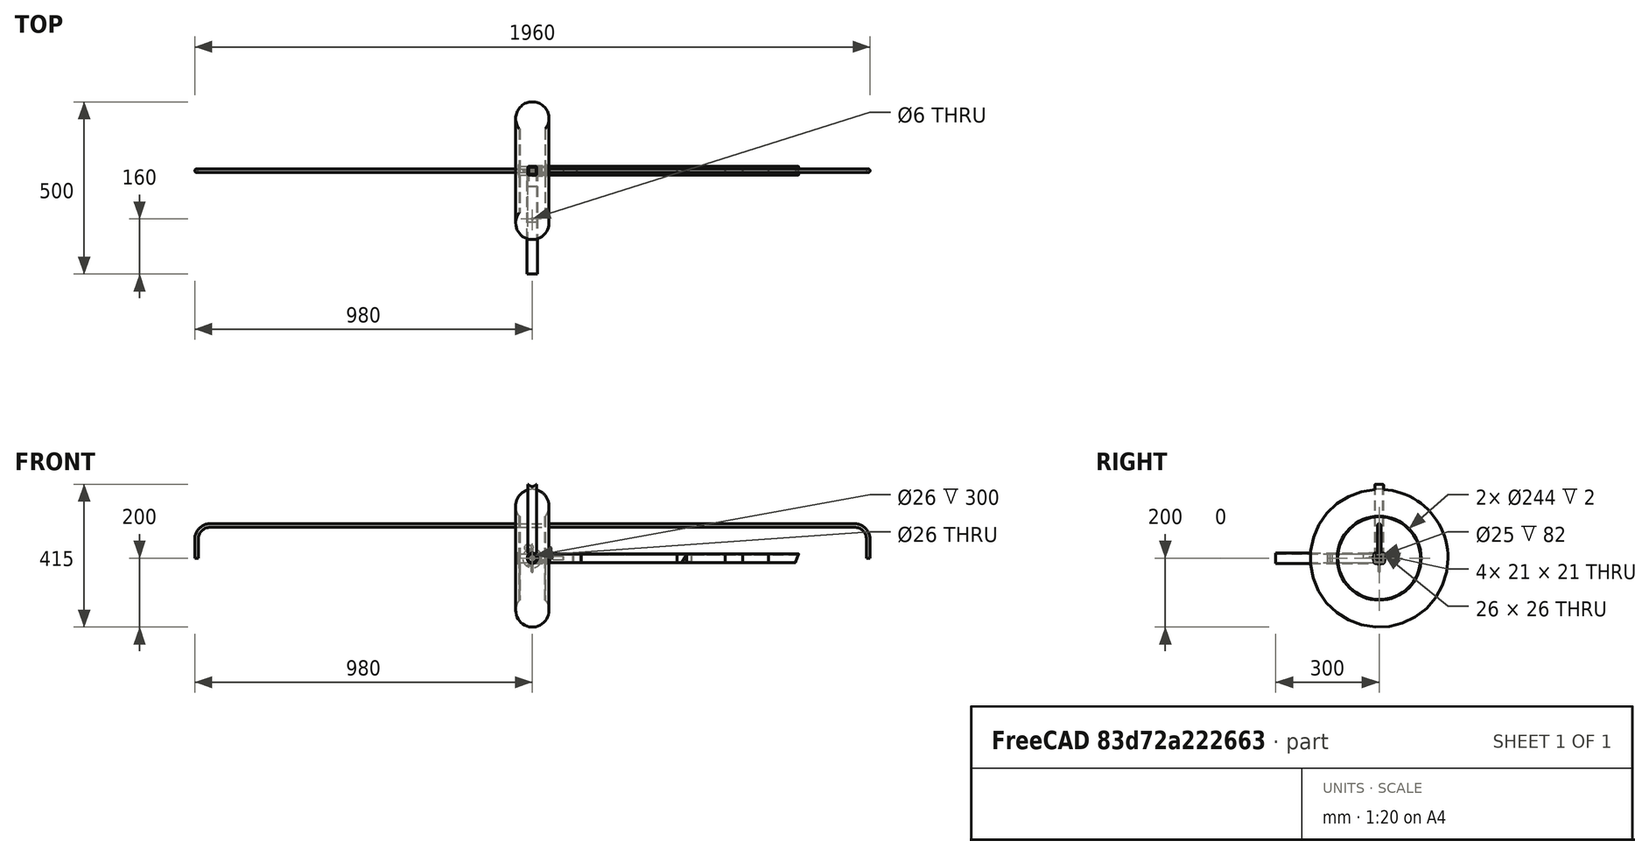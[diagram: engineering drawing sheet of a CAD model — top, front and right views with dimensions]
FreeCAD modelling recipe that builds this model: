
FCSTD DOCUMENT  (FreeCAD 1.0R39109 (Git))
Label: brouetteas4
License: Creative Commons Attribution-NonCommercial-ShareAlike
LicenseURL: http://creativecommons.org/licenses/by-nc-sa/4.0/
objects: PartDesign::CoordinateSystem×62, App::Link×60, Sketcher::SketchObject×37, TechDraw::DrawViewDimension×27, App::Part×25, PartDesign::Body×24, TechDraw::DrawViewBalloon×23, PartDesign::Pad×20, TechDraw::DrawProjGroupItem×15, PartDesign::Groove×8, TechDraw::DrawSVGTemplate×7, TechDraw::DrawPage×7, PartDesign::Plane×6, TechDraw::DrawProjGroup×3, TechDraw::DrawViewDimExtent×3, App::DocumentObjectGroup×2, PartDesign::AdditivePipe×2, Spreadsheet::Sheet×2, PartDesign::Revolution×2, App::FeaturePython×1, +5 more types
note: 320 computed .brp shape members not serialized (recipe doc carries the construction recipe); baked Part::Feature solids carry a one-line shape summary decoded from their .brp

FEATURE [PartDesign::CoordinateSystem] LCS_Origin
  AttacherType = Attacher::AttachEngine3D
  AttachmentSupport = -> [X_Axis]
  MapMode = 2
FEATURE [App::DocumentObjectGroup] Constraints
FEATURE [App::FeaturePython] Variables  # WARN: FeaturePython — macro-defined, semantics opaque (R4)
FEATURE [Sketcher::SketchObject] Sketch
  ArcFitTolerance = 0
  FullyConstrained = true
  MakeInternals = false
  MapMode = 5
  Placement = pos=(0,0,0) rot=(0.57735,0.57735,0.57735;2.0944rad)
  expr: Constraints[15] = .Constraints.hauteur * 0.1
  expr: Constraints[27] = .Constraints.epaisseur
  sketch-geometry (12):
    g0: LineSegment StartX=-10 StartY=12.5 StartZ=0 EndX=10 EndY=12.5 EndZ=0
    g1: LineSegment StartX=12.5 StartY=10 StartZ=0 EndX=12.5 EndY=-10 EndZ=0
    g2: LineSegment StartX=10 StartY=-12.5 StartZ=0 EndX=-10 EndY=-12.5 EndZ=0
    g3: LineSegment StartX=-12.5 StartY=-10 StartZ=0 EndX=-12.5 EndY=10 EndZ=0
    g4: ArcOfCircle CenterX=-10 CenterY=10 CenterZ=0 NormalX=0 NormalY=0 NormalZ=1 AngleXU=0 Radius=2.5 StartAngle=1.5708 EndAngle=3.14159
    g5: ArcOfCircle CenterX=10 CenterY=10 CenterZ=0 NormalX=0 NormalY=0 NormalZ=1 AngleXU=0 Radius=2.5 StartAngle=2e-16 EndAngle=1.5708
    g6: ArcOfCircle CenterX=10 CenterY=-10 CenterZ=0 NormalX=0 NormalY=0 NormalZ=1 AngleXU=0 Radius=2.5 StartAngle=4.71239 EndAngle=6.28319
    g7: ArcOfCircle CenterX=-10 CenterY=-10 CenterZ=0 NormalX=0 NormalY=0 NormalZ=1 AngleXU=0 Radius=2.5 StartAngle=3.14159 EndAngle=4.71239
    g8: LineSegment StartX=-10.5 StartY=10.5 StartZ=0 EndX=10.5 EndY=10.5 EndZ=0
    g9: LineSegment StartX=10.5 StartY=10.5 StartZ=0 EndX=10.5 EndY=-10.5 EndZ=0
    g10: LineSegment StartX=10.5 StartY=-10.5 StartZ=0 EndX=-10.5 EndY=-10.5 EndZ=0
    g11: LineSegment StartX=-10.5 StartY=-10.5 StartZ=0 EndX=-10.5 EndY=10.5 EndZ=0
  constraints (28):
    c: Horizontal(g2)
    c: Vertical(g3)
    c: Tangent(g0,g4) = 1.5708
    c: Tangent(g3,g4) = 1.5708
    c: Tangent(g0,g5) = 1.5708
    c: Tangent(g1,g5) = 1.5708
    c: Tangent(g1,g6) = 1.5708
    c: Tangent(g2,g6) = 1.5708
    c: Tangent(g2,g7) = 1.5708
    c: Tangent(g3,g7) = 1.5708
    c: Equal(g4,g5)
    c: DistanceY(g2,g0) = 25  'hauteur'
    c: DistanceX(g3,g1) = 25  'largeur'
    c: Equal(g5,g6)
    c: Equal(g6,g7)
    c: Radius(g7) = 2.5
    c: Symmetric(g1,g1,g-1)
    c: Symmetric(g0,g0,g-2)
    c: Coincident(g8,g9)
    c: Coincident(g9,g10)
    c: Coincident(g10,g11)
    c: Coincident(g11,g8)
    c: Horizontal(g10)
    c: Vertical(g11)
    c: Symmetric(g8,g9,g-1)
    c: Symmetric(g8,g8,g-2)
    c: DistanceX(g3,g8) = 2  'epaisseur'
    c: DistanceY(g2,g9) = 2
FEATURE [PartDesign::Pad] Pad
  Direction = (1,1e-16,-1e-16)
  Length = 2285
  Length2 = 100
  Placement = pos=(0,0,0) rot=(0.57735,0.57735,0.57735;2.0944rad)
  Profile = -> Sketch
  Suppressed = false
  Type = 0
  expr: Length = Spreadsheet.B4 - Spreadsheet.B2 + 300
FEATURE [PartDesign::CoordinateSystem] LCS_0  label="cote1"
  AttacherType = Attacher::AttachEngine3D
  AttachmentSupport = -> [X_Axis002]
  MapMode = 2
FEATURE [PartDesign::CoordinateSystem] LCS_0001  label="cote1A2"
  AttacherType = Attacher::AttachEngine3D
  AttachmentSupport = -> [X_Axis003]
  MapMode = 2
FEATURE [Sketcher::SketchObject] Sketch001
  ArcFitTolerance = 0
  FullyConstrained = true
  MakeInternals = false
  MapMode = 5
  Placement = pos=(0,0,0) rot=(0.57735,0.57735,0.57735;2.0944rad)
  expr: Constraints[15] = .Constraints.hauteur * 0.1
  expr: Constraints[27] = .Constraints.epaisseur
  sketch-geometry (12):
    g0: LineSegment StartX=-10 StartY=12.5 StartZ=0 EndX=10 EndY=12.5 EndZ=0
    g1: LineSegment StartX=12.5 StartY=10 StartZ=0 EndX=12.5 EndY=-10 EndZ=0
    g2: LineSegment StartX=10 StartY=-12.5 StartZ=0 EndX=-10 EndY=-12.5 EndZ=0
    g3: LineSegment StartX=-12.5 StartY=-10 StartZ=0 EndX=-12.5 EndY=10 EndZ=0
    g4: ArcOfCircle CenterX=-10 CenterY=10 CenterZ=0 NormalX=0 NormalY=0 NormalZ=1 AngleXU=0 Radius=2.5 StartAngle=1.5708 EndAngle=3.14159
    g5: ArcOfCircle CenterX=10 CenterY=10 CenterZ=0 NormalX=0 NormalY=0 NormalZ=1 AngleXU=0 Radius=2.5 StartAngle=2e-16 EndAngle=1.5708
    g6: ArcOfCircle CenterX=10 CenterY=-10 CenterZ=0 NormalX=0 NormalY=0 NormalZ=1 AngleXU=0 Radius=2.5 StartAngle=4.71239 EndAngle=6.28319
    g7: ArcOfCircle CenterX=-10 CenterY=-10 CenterZ=0 NormalX=0 NormalY=0 NormalZ=1 AngleXU=0 Radius=2.5 StartAngle=3.14159 EndAngle=4.71239
    g8: LineSegment StartX=-10.5 StartY=10.5 StartZ=0 EndX=10.5 EndY=10.5 EndZ=0
    g9: LineSegment StartX=10.5 StartY=10.5 StartZ=0 EndX=10.5 EndY=-10.5 EndZ=0
    g10: LineSegment StartX=10.5 StartY=-10.5 StartZ=0 EndX=-10.5 EndY=-10.5 EndZ=0
    g11: LineSegment StartX=-10.5 StartY=-10.5 StartZ=0 EndX=-10.5 EndY=10.5 EndZ=0
  constraints (28):
    c: Horizontal(g2)
    c: Vertical(g3)
    c: Tangent(g0,g4) = 1.5708
    c: Tangent(g3,g4) = 1.5708
    c: Tangent(g0,g5) = 1.5708
    c: Tangent(g1,g5) = 1.5708
    c: Tangent(g1,g6) = 1.5708
    c: Tangent(g2,g6) = 1.5708
    c: Tangent(g2,g7) = 1.5708
    c: Tangent(g3,g7) = 1.5708
    c: Equal(g4,g5)
    c: DistanceY(g2,g0) = 25  'hauteur'
    c: DistanceX(g3,g1) = 25  'largeur'
    c: Equal(g5,g6)
    c: Equal(g6,g7)
    c: Radius(g7) = 2.5
    c: Symmetric(g1,g1,g-1)
    c: Symmetric(g0,g0,g-2)
    c: Coincident(g8,g9)
    c: Coincident(g9,g10)
    c: Coincident(g10,g11)
    c: Coincident(g11,g8)
    c: Horizontal(g10)
    c: Vertical(g11)
    c: Symmetric(g8,g9,g-1)
    c: Symmetric(g8,g8,g-2)
    c: DistanceX(g3,g8) = 2  'epaisseur'
    c: DistanceY(g2,g9) = 2
FEATURE [PartDesign::Body] Body001
  AllowCompound = false
  Origin = -> Origin004
FEATURE [PartDesign::Pad] Pad001
  Direction = (1,1e-16,-1e-16)
  Length = 610
  Length2 = 100
  Placement = pos=(0,0,0) rot=(0.57735,0.57735,0.57735;2.0944rad)
  Profile = -> Sketch001
  Suppressed = false
  Type = 0
FEATURE [PartDesign::CoordinateSystem] LCS_0002
  AttacherType = Attacher::AttachEngine3D
  AttachmentOffset = pos=(0,5,0) rot=(0,0,1;0rad)
  AttachmentSupport = -> [X_Axis005]
  MapMode = 2
  Placement = pos=(0,5,0) rot=(0,0,1;0rad)
FEATURE [PartDesign::CoordinateSystem] LCS_0003
  AttacherType = Attacher::AttachEngine3D
  AttachmentOffset = pos=(0,5,0) rot=(0,0,1;0rad)
  AttachmentSupport = -> [X_Axis006]
  MapMode = 2
  Placement = pos=(0,5,0) rot=(0,0,1;0rad)
FEATURE [Sketcher::SketchObject] Sketch002
  ArcFitTolerance = 0
  AttachmentSupport = -> [XZ_Plane007]
  FullyConstrained = true
  MakeInternals = false
  MapMode = 5
  Placement = pos=(0,0,0) rot=(1,0,0;1.5708rad)
  expr: .Constraints.longueur = Spreadsheet.B4 - Spreadsheet.B2 * 2 - 10
  expr: Constraints[4] = Spreadsheet.B2
  sketch-geometry (7):
    g0: LineSegment StartX=-975 StartY=0 StartZ=0 EndX=-975 EndY=25 EndZ=0
    g1: LineSegment StartX=975 StartY=8e-16 StartZ=0 EndX=975 EndY=25 EndZ=0
    g2: LineSegment StartX=-975 StartY=25 StartZ=0 EndX=-975 EndY=55 EndZ=0
    g3: LineSegment StartX=-935 StartY=95 StartZ=0 EndX=935 EndY=95 EndZ=0
    g4: LineSegment StartX=975 StartY=55 StartZ=0 EndX=975 EndY=25 EndZ=0
    g5: ArcOfCircle CenterX=935 CenterY=55 CenterZ=0 NormalX=0 NormalY=0 NormalZ=1 AngleXU=0 Radius=40 StartAngle=0 EndAngle=1.5708
    g6: ArcOfCircle CenterX=-935 CenterY=55 CenterZ=0 NormalX=0 NormalY=0 NormalZ=1 AngleXU=0 Radius=40 StartAngle=1.5708 EndAngle=3.14159
  constraints (19):
    c: PointOnObject(g0,g-1)
    c: Vertical(g0)
    c: Vertical(g1)
    c: Symmetric(g0,g1,g-2)
    c: DistanceY(g0,g0) = 25
    c: DistanceX(g0,g1) = 1950  'longueur'
    c: Equal(g1,g0)
    c: Coincident(g0,g2)
    c: Vertical(g2)
    c: Horizontal(g3)
    c: Coincident(g4,g1)
    c: Vertical(g4)
    c: Tangent(g3,g5) = 1.5708
    c: Tangent(g4,g5) = 1.5708
    c: Tangent(g2,g6) = 1.5708
    c: Tangent(g3,g6) = 1.5708
    c: Equal(g6,g5)
    c: DistanceY(g0,g3) = 70
    c: Radius(g6) = 40
FEATURE [Sketcher::SketchObject] Sketch003
  ArcFitTolerance = 0
  AttachmentSupport = -> [XY_Plane007]
  ExternalGeometry = -> [Sketch002]
  FullyConstrained = true
  MakeInternals = false
  MapMode = 5
  sketch-geometry (1):
    g0: Circle CenterX=-975 CenterY=0 CenterZ=0 NormalX=0 NormalY=0 NormalZ=1 AngleXU=0 Radius=5
  constraints (2):
    c: Coincident(g0,g-3)
    c: Diameter(g0) = 10
FEATURE [PartDesign::AdditivePipe] AdditivePipe
  AuxilleryCurvelinear = true
  AuxillerySpineTangent = false
  Binormal = (0,0,0)
  Mode = 0
  Profile = -> Sketch003
  Spine = -> Sketch002
  SpineTangent = false
  Suppressed = false
  Transformation = 0
  Transition = 0
FEATURE [PartDesign::Body] Body002
  AllowCompound = false
  Group = -> [Sketch002,Sketch003,AdditivePipe]
  Origin = -> Origin007
  Tip = -> AdditivePipe
FEATURE [App::Part] A3
  Group = -> [LCS_0002,Body002]
  Nom_de_la_piece = A3
  Origin = -> Origin005
  Reference_AP = fer rond Ø10
  longueur = 2140
FEATURE [Sketcher::SketchObject] Sketch004
  ArcFitTolerance = 0
  AttachmentSupport = -> [YZ_Plane008]
  FullyConstrained = true
  MakeInternals = false
  MapMode = 5
  Placement = pos=(0,0,0) rot=(0.57735,0.57735,0.57735;2.0944rad)
  sketch-geometry (1):
    g0: Circle CenterX=0 CenterY=0 CenterZ=0 NormalX=0 NormalY=0 NormalZ=1 AngleXU=0 Radius=5
  constraints (2):
    c: Coincident(g0,g-1)
    c: Diameter(g0) = 10  'diametre'
FEATURE [PartDesign::Pad] Pad002
  Direction = (1,0,0)
  Length = 90
  Length2 = 100
  Placement = pos=(0,0,0) rot=(0.57735,0.57735,0.57735;2.0944rad)
  Profile = -> Sketch004
  Suppressed = false
  Type = 0
FEATURE [PartDesign::Body] Body003
  AllowCompound = false
  Group = -> [Sketch004,Pad002]
  Origin = -> Origin008
  Tip = -> Pad002
FEATURE [App::Part] A4
  Group = -> [LCS_0003,Body003]
  Nom_de_la_piece = 'A4
  Origin = -> Origin006
  Reference_AP = fer rond Ø10
  longueur = 90
FEATURE [PartDesign::CoordinateSystem] cote2A2
  AttacherType = Attacher::AttachEngine3D
  AttachmentSupport = -> [Pad001]
  MapMode = 5
  Placement = pos=(610,2.684e-13,0) rot=(0.57735,0.57735,0.57735;2.0944rad)
FEATURE [Spreadsheet::Sheet] Spreadsheet
  cells = A1='profile; A2='tube carré; B2=25; C2='mm; A4='taille utile du plateau; B4=2010; C4='X; D4=610; A5='hauteur plateau; B5=500; A6='hauteur de la roue; B6=400; A7='axe; B7=25; A8='epaisseur upn axe; B8=4; A9='espace des roues; B9=95; A10='ecart au sol; B10=75; A11='hauteur des mains; B11==D11 * 0.45; C11='taille de la personne; D11=1700; A12='hauteur du panneau finale; B12=610; A13='tube poigné; B13=30
FEATURE [PartDesign::CoordinateSystem] face1A2
  AttacherType = Attacher::AttachEngine3D
  AttachmentOffset = pos=(0,12.5,0) rot=(0,0,1;0rad)
  AttachmentSupport = -> [Pad001]
  MapMode = 5
  Placement = pos=(12.5,12.5,2.1e-15) rot=(0.57735,0.57735,0.57735;4.18879rad)
  expr: .AttachmentOffset.Base.y = Spreadsheet.B2 / 2
FEATURE [PartDesign::CoordinateSystem] face4A2
  AttacherType = Attacher::AttachEngine3D
  AttachmentOffset = pos=(0,597.5,0) rot=(0,0,1;0rad)
  AttachmentSupport = -> [Pad001]
  MapMode = 5
  Placement = pos=(597.5,12.5,2.1e-15) rot=(0.57735,0.57735,0.57735;4.18879rad)
  expr: .AttachmentOffset.Base.y = Spreadsheet.D4 - Spreadsheet.B2 / 2
FEATURE [PartDesign::CoordinateSystem] face2  label="face2A2"
  AttacherType = Attacher::AttachEngine3D
  AttachmentOffset = pos=(0,207.5,0) rot=(0,0,1;0rad)
  AttachmentSupport = -> [Pad001]
  MapMode = 5
  Placement = pos=(207.5,12.5,2.1e-15) rot=(0.57735,0.57735,0.57735;4.18879rad)
  expr: .AttachmentOffset.Base.y = (Spreadsheet.D4 - Spreadsheet.B2) * 1 / 3 + Spreadsheet.B2 / 2
FEATURE [PartDesign::CoordinateSystem] face3A2
  AttacherType = Attacher::AttachEngine3D
  AttachmentOffset = pos=(0,402.5,0) rot=(0,0,1;0rad)
  AttachmentSupport = -> [Pad001]
  MapMode = 5
  Placement = pos=(402.5,12.5,2.1e-15) rot=(0.57735,0.57735,0.57735;4.18879rad)
  expr: .AttachmentOffset.Base.y = (Spreadsheet.D4 - Spreadsheet.B2) * 2 / 3 + Spreadsheet.B2 / 2
FEATURE [PartDesign::CoordinateSystem] attach
  AttacherType = Attacher::AttachEngine3D
  AttachmentOffset = pos=(0,305,0) rot=(0,0,1;0rad)
  AttachmentSupport = -> [Pad001]
  MapMode = 5
  Placement = pos=(305,-12.5,-2.1e-15) rot=(0.57735,0.57735,-0.57735;2.0944rad)
  expr: .AttachmentOffset.Base.y = Spreadsheet.D4 / 2
FEATURE [App::Link] A2001
  AssemblyType = Asm4EE
  AttachedBy = #attach
  AttachedTo = Parent Assembly#LCS_Origin
  AttachmentOffset = pos=(0,0,0) rot=(0,-1,0;1.5708rad)
  LinkPlacement = pos=(12.5,-305,-2.84e-14) rot=(-0.707107,-0.707107,0;3.14159rad)
  LinkedObject = -> A2
  Placement = pos=(12.5,-305,-2.84e-14) rot=(-0.707107,-0.707107,0;3.14159rad)
  expr: Placement = LCS_Origin.Placement * AttachmentOffset * attach.Placement ^ -1
FEATURE [App::Link] A1001
  AssemblyType = Asm4EE
  AttachedBy = #LCS_0
  AttachedTo = A2001#face1A2
  AttachmentOffset = pos=(0,0,0) rot=(0,-1,0;1.5708rad)
  LinkPlacement = pos=(25,-292.5,-3.05e-14) rot=(0,0,1;0rad)
  LinkedObject = -> A1
  Placement = pos=(25,-292.5,-3.05e-14) rot=(0,0,1;0rad)
  expr: Placement = A2001.Placement * face1A2.Placement * AttachmentOffset * LCS_0.Placement ^ -1
FEATURE [App::Link] A1004
  AssemblyType = Asm4EE
  AttachedBy = #LCS_0
  AttachedTo = A2001#face4A2
  AttachmentOffset = pos=(0,0,0) rot=(0,-1,0;1.5708rad)
  LinkPlacement = pos=(25,292.5,1.54e-14) rot=(0,0,1;0rad)
  LinkedObject = -> A1
  Placement = pos=(25,292.5,1.54e-14) rot=(0,0,1;0rad)
  expr: Placement = A2001.Placement * face4A2.Placement * AttachmentOffset * LCS_0.Placement ^ -1
FEATURE [App::Link] A3001
  AssemblyType = Asm4EE
  AttachedBy = #LCS_0002
  AttachedTo = A1001#faceA1
  AttachmentOffset = pos=(0,0,0) rot=(0.57735,0.57735,-0.57735;4.18879rad)
  LinkPlacement = pos=(1005,-310,-12.5) rot=(0,0,1;0rad)
  LinkedObject = -> A3
  Placement = pos=(1005,-310,-12.5) rot=(0,0,1;0rad)
  expr: Placement = A1001.Placement * faceA1.Placement * AttachmentOffset * LCS_0002.Placement ^ -1
FEATURE [App::Link] A3002
  AssemblyType = Asm4EE
  AttachedBy = #LCS_0002
  AttachedTo = A1004#face2A1
  AttachmentOffset = pos=(0,0,0) rot=(-0.57735,0.57735,-0.57735;2.0944rad)
  LinkPlacement = pos=(1005,310,-12.5) rot=(0,0,1;3.14159rad)
  LinkedObject = -> A3
  Placement = pos=(1005,310,-12.5) rot=(0,0,1;3.14159rad)
  expr: Placement = A1004.Placement * face2A1.Placement * AttachmentOffset * LCS_0002.Placement ^ -1
FEATURE [App::Link] A4001
  AssemblyType = Asm4EE
  AttachedBy = #LCS_0003
  AttachedTo = A1001#faceA1
  AttachmentOffset = pos=(0,0,0) rot=(0,-0.707107,0.707107;3.14159rad)
  LinkPlacement = pos=(1005,-310,-12.5) rot=(0,-1,0;1.5708rad)
  LinkedObject = -> A4
  Placement = pos=(1005,-310,-12.5) rot=(0,-1,0;1.5708rad)
  expr: Placement = A1001.Placement * faceA1.Placement * AttachmentOffset * LCS_0003.Placement ^ -1
FEATURE [App::Link] A4002
  AssemblyType = Asm4EE
  AttachedBy = #LCS_0003
  AttachedTo = A1004#face2A1
  AttachmentOffset = pos=(0,0,0) rot=(1,0,0;4.71239rad)
  LinkPlacement = pos=(1005,310,-12.5) rot=(-0.707107,0,-0.707107;3.14159rad)
  LinkedObject = -> A4
  Placement = pos=(1005,310,-12.5) rot=(-0.707107,0,-0.707107;3.14159rad)
  expr: Placement = A1004.Placement * face2A1.Placement * AttachmentOffset * LCS_0003.Placement ^ -1
FEATURE [PartDesign::CoordinateSystem] basbord
  AttacherType = Attacher::AttachEngine3D
  AttachmentOffset = pos=(0,-12.5,0) rot=(0,0,1;0rad)
  AttachmentSupport = -> [Pad001]
  MapMode = 5
  Placement = pos=(610,2.684e-13,-12.5) rot=(0.57735,0.57735,0.57735;2.0944rad)
  expr: .AttachmentOffset.Base.y = -Spreadsheet.B2 / 2
FEATURE [App::Link] A2003
  AssemblyType = Asm4EE
  AttachedBy = #basbord
  AttachedTo = A1004#face2A1
  AttachmentOffset = pos=(0,0,0) rot=(0,0,1;1.5708rad)
  LinkPlacement = pos=(1005,-305,-25) rot=(0.707107,0.707107,0;3.14159rad)
  LinkedObject = -> A2
  Placement = pos=(1005,-305,-25) rot=(0.707107,0.707107,0;3.14159rad)
  expr: Placement = A1004.Placement * face2A1.Placement * AttachmentOffset * basbord.Placement ^ -1
FEATURE [PartDesign::CoordinateSystem] LCS_0004
  AttacherType = Attacher::AttachEngine3D
  AttachmentOffset = pos=(100,-12.5,0) rot=(0,0,1;0rad)
  AttachmentSupport = -> [X_Axis009]
  MapMode = 2
  Placement = pos=(100,-12.5,0) rot=(0,0,1;0rad)
FEATURE [Sketcher::SketchObject] Sketch005
  ArcFitTolerance = 0
  AttachmentSupport = -> [XY_Plane010]
  FullyConstrained = true
  MakeInternals = false
  MapMode = 5
  sketch-geometry (16):
    g0: LineSegment StartX=-41 StartY=12.5 StartZ=0 EndX=41 EndY=12.5 EndZ=0
    g1: LineSegment StartX=-41 StartY=12.5 StartZ=0 EndX=-41 EndY=17.5 EndZ=0
    g2: LineSegment StartX=-41 StartY=17.5 StartZ=0 EndX=-38 EndY=17.5 EndZ=0
    g3: LineSegment StartX=-38 StartY=17.5 StartZ=0 EndX=-38 EndY=120 EndZ=0
    g4: LineSegment StartX=-38 StartY=120 StartZ=0 EndX=-36 EndY=120 EndZ=0
    g5: LineSegment StartX=-36 StartY=120 StartZ=0 EndX=-36 EndY=122 EndZ=0
    g6: LineSegment StartX=-36 StartY=122 StartZ=0 EndX=-38 EndY=122 EndZ=0
    g7: LineSegment StartX=41 StartY=12.5 StartZ=0 EndX=41 EndY=17.5 EndZ=0
    g8: LineSegment StartX=41 StartY=17.5 StartZ=0 EndX=38 EndY=17.5 EndZ=0
    g9: LineSegment StartX=38 StartY=17.5 StartZ=0 EndX=38 EndY=120 EndZ=0
    g10: LineSegment StartX=38 StartY=120 StartZ=0 EndX=36 EndY=120 EndZ=0
    g11: LineSegment StartX=36 StartY=120 StartZ=0 EndX=36 EndY=122 EndZ=0
    g12: LineSegment StartX=36 StartY=122 StartZ=0 EndX=38 EndY=122 EndZ=0
    g13: GeomPoint [constr] X=-1e-15 Y=151.744 Z=0
    g14: GeomPoint [constr] X=0 Y=200 Z=0
    g15: ArcOfCircle CenterX=-1e-15 CenterY=151.744 CenterZ=0 NormalX=0 NormalY=0 NormalZ=1 AngleXU=0 Radius=48.2564 StartAngle=5.61907 EndAngle=10.0889
  constraints (42):
    c: Symmetric(g0,g0,g-2)
    c: Coincident(g0,g1)
    c: Vertical(g1)
    c: Coincident(g1,g2)
    c: Horizontal(g2)
    c: Coincident(g2,g3)
    c: Vertical(g3)
    c: Coincident(g3,g4)
    c: Horizontal(g4)
    c: Coincident(g4,g5)
    c: Coincident(g5,g6)
    c: Horizontal(g6)
    c: Vertical(g5)
    c: PointOnObject(g6,g3)
    c: DistanceX(g2,g2) = 3
    c: DistanceX(g4,g4) = 2
    c: DistanceY(g5,g5) = 2
    c: Vertical(g7)
    c: Coincident(g7,g8)
    c: Horizontal(g8)
    c: Coincident(g8,g9)
    c: Coincident(g9,g10)
    c: Horizontal(g10)
    c: Coincident(g10,g11)
    c: Coincident(g11,g12)
    c: Horizontal(g12)
    c: Vertical(g11)
    c: PointOnObject(g12,g9)
    c: Symmetric(g9,g3,g-2)
    c: Symmetric(g5,g11,g-2)
    c: DistanceX(g2,g8) = 76
    c: Coincident(g0,g7)
    c: DistanceY(g-1,g0) = 12.5
    c: DistanceY(g7,g7) = 5
    c: Symmetric(g2,g8,g-2)
    c: PointOnObject(g14,g-2)
    c: DistanceY(g-1,g9) = 120
    c: DistanceY(g-1,g14) = 200
    c: Coincident(g15,g13)
    c: Coincident(g15,g6)
    c: Coincident(g15,g12)
    c: PointOnObject(g14,g15)
FEATURE [PartDesign::Revolution] Revolution
  Angle = 360
  Angle2 = 60
  Axis = (1,0,0)
  Base = (0,0,0)
  Profile = -> Sketch005
  ReferenceAxis = -> Sketch005 [H_Axis]
  Suppressed = false
  Type = 0
FEATURE [PartDesign::Body] Body004
  AllowCompound = false
  Group = -> [Sketch005,Revolution]
  Origin = -> Origin010
  Tip = -> Revolution
FEATURE [App::Part] Roue_increvable___389___axe25_L_82
  Group = -> [LCS_0004,Body004]
  Nom_de_la_piece = roue
  Origin = -> Origin009
  Reference_AP = Roue increvable Ø389 Øaxe25 L 82
FEATURE [PartDesign::CoordinateSystem] LCS_0005
  AttacherType = Attacher::AttachEngine3D
  AttachmentSupport = -> [X_Axis011]
  MapMode = 2
FEATURE [PartDesign::Body] Body005
  AllowCompound = false
  Origin = -> Origin012
FEATURE [Sketcher::SketchObject] Sketch007
  ArcFitTolerance = 0
  FullyConstrained = true
  MakeInternals = false
  MapMode = 2
  Placement = pos=(0,0,0) rot=(0.57735,0.57735,0.57735;2.0944rad)
  expr: Constraints[15] = .Constraints.hauteur * 0.1
  expr: Constraints[27] = .Constraints.epaisseur
  sketch-geometry (12):
    g0: LineSegment StartX=-10 StartY=12.5 StartZ=0 EndX=10 EndY=12.5 EndZ=0
    g1: LineSegment StartX=12.5 StartY=10 StartZ=0 EndX=12.5 EndY=-10 EndZ=0
    g2: LineSegment StartX=10 StartY=-12.5 StartZ=0 EndX=-10 EndY=-12.5 EndZ=0
    g3: LineSegment StartX=-12.5 StartY=-10 StartZ=0 EndX=-12.5 EndY=10 EndZ=0
    g4: ArcOfCircle CenterX=-10 CenterY=10 CenterZ=0 NormalX=0 NormalY=0 NormalZ=1 AngleXU=0 Radius=2.5 StartAngle=1.5708 EndAngle=3.14159
    g5: ArcOfCircle CenterX=10 CenterY=10 CenterZ=0 NormalX=0 NormalY=0 NormalZ=1 AngleXU=0 Radius=2.5 StartAngle=2e-16 EndAngle=1.5708
    g6: ArcOfCircle CenterX=10 CenterY=-10 CenterZ=0 NormalX=0 NormalY=0 NormalZ=1 AngleXU=0 Radius=2.5 StartAngle=4.71239 EndAngle=6.28319
    g7: ArcOfCircle CenterX=-10 CenterY=-10 CenterZ=0 NormalX=0 NormalY=0 NormalZ=1 AngleXU=0 Radius=2.5 StartAngle=3.14159 EndAngle=4.71239
    g8: LineSegment StartX=-10.5 StartY=10.5 StartZ=0 EndX=10.5 EndY=10.5 EndZ=0
    g9: LineSegment StartX=10.5 StartY=10.5 StartZ=0 EndX=10.5 EndY=-10.5 EndZ=0
    g10: LineSegment StartX=10.5 StartY=-10.5 StartZ=0 EndX=-10.5 EndY=-10.5 EndZ=0
    g11: LineSegment StartX=-10.5 StartY=-10.5 StartZ=0 EndX=-10.5 EndY=10.5 EndZ=0
  constraints (28):
    c: Horizontal(g2)
    c: Vertical(g3)
    c: Tangent(g0,g4) = 1.5708
    c: Tangent(g3,g4) = 1.5708
    c: Tangent(g0,g5) = 1.5708
    c: Tangent(g1,g5) = 1.5708
    c: Tangent(g1,g6) = 1.5708
    c: Tangent(g2,g6) = 1.5708
    c: Tangent(g2,g7) = 1.5708
    c: Tangent(g3,g7) = 1.5708
    c: Equal(g4,g5)
    c: DistanceY(g2,g0) = 25  'hauteur'
    c: DistanceX(g3,g1) = 25  'largeur'
    c: Equal(g5,g6)
    c: Equal(g6,g7)
    c: Radius(g7) = 2.5
    c: Symmetric(g1,g1,g-1)
    c: Symmetric(g0,g0,g-2)
    c: Coincident(g8,g9)
    c: Coincident(g9,g10)
    c: Coincident(g10,g11)
    c: Coincident(g11,g8)
    c: Horizontal(g10)
    c: Vertical(g11)
    c: Symmetric(g8,g9,g-1)
    c: Symmetric(g8,g8,g-2)
    c: DistanceX(g3,g8) = 2  'epaisseur'
    c: DistanceY(g2,g9) = 2
FEATURE [PartDesign::Pad] Pad003
  Direction = (1,1e-16,-1e-16)
  Length = 258.5
  Length2 = 100
  Placement = pos=(0,0,0) rot=(0.57735,0.57735,0.57735;2.0944rad)
  Profile = -> Sketch007
  Suppressed = false
  Type = 0
  expr: Length = Spreadsheet.B5 - Spreadsheet.B6 / 2 - Spreadsheet.B7 / 2 - Spreadsheet.B8 - Spreadsheet.B2
FEATURE [PartDesign::CoordinateSystem] roue1
  AttacherType = Attacher::AttachEngine3D
  AttachmentOffset = pos=(0,82.5,0) rot=(0,0,1;0rad)
  AttachmentSupport = -> [Pad001]
  MapMode = 5
  Placement = pos=(82.5,1.56e-14,12.5) rot=(0,0,-1;1.5708rad)
  expr: .AttachmentOffset.Base.y = Spreadsheet.B9 - Spreadsheet.B2 / 2
FEATURE [PartDesign::CoordinateSystem] roue2
  AttacherType = Attacher::AttachEngine3D
  AttachmentOffset = pos=(0,527.5,0) rot=(0,0,1;0rad)
  AttachmentSupport = -> [Pad001]
  MapMode = 5
  Placement = pos=(527.5,1.144e-13,12.5) rot=(0,0,-1;1.5708rad)
  expr: .AttachmentOffset.Base.y = Spreadsheet.D4 - (Spreadsheet.B9 - Spreadsheet.B2 / 2)
FEATURE [App::Part] A2
  Group = -> [LCS_0001,Body001,Sketch001,Pad001,cote2A2,face1A2,face4A2,face2,face3A2,attach,basbord,roue1,roue2]
  Nom_de_la_piece = 'A2
  Origin = -> Origin003
  Reference_AP = Tube carré 25 x 2
  longueur = 610
FEATURE [App::Link] A5001
  AssemblyType = Asm4EE
  AttachedBy = #LCS_0005
  AttachedTo = A2003#roue1
  AttachmentOffset = pos=(0,0,0) rot=(-0.57735,-0.57735,-0.57735;2.0944rad)
  LinkPlacement = pos=(1005,-222.5,-37.5) rot=(-0.57735,0.57735,0.57735;2.0944rad)
  LinkedObject = -> A5
  Placement = pos=(1005,-222.5,-37.5) rot=(-0.57735,0.57735,0.57735;2.0944rad)
  expr: Placement = A2003.Placement * roue1.Placement * AttachmentOffset * LCS_0005.Placement ^ -1
FEATURE [App::Link] A5002
  AssemblyType = Asm4EE
  AttachedBy = #LCS_0005
  AttachedTo = A2003#roue2
  AttachmentOffset = pos=(0,0,0) rot=(0,1,0;4.71239rad)
  LinkPlacement = pos=(1005,222.5,-37.5) rot=(0,-1,0;4.71239rad)
  LinkedObject = -> A5
  Placement = pos=(1005,222.5,-37.5) rot=(0,-1,0;4.71239rad)
  expr: Placement = A2003.Placement * roue2.Placement * AttachmentOffset * LCS_0005.Placement ^ -1
FEATURE [PartDesign::CoordinateSystem] renfort
  AttacherType = Attacher::AttachEngine3D
  AttachmentOffset = pos=(0,246,0) rot=(0,0,1;0rad)
  AttachmentSupport = -> [Pad003]
  MapMode = 5
  Placement = pos=(246,5.19e-14,12.5) rot=(0,0,-1;1.5708rad)
  expr: .AttachmentOffset.Base.y = Pad003.Length - Spreadsheet.B2 * 1 mm / 2
FEATURE [PartDesign::CoordinateSystem] LCS_0006
  AttacherType = Attacher::AttachEngine3D
  AttachmentSupport = -> [X_Axis013]
  MapMode = 2
FEATURE [Sketcher::SketchObject] Sketch008
  ArcFitTolerance = 0
  FullyConstrained = true
  MakeInternals = false
  MapMode = 2
  Placement = pos=(0,0,0) rot=(0.57735,0.57735,0.57735;2.0944rad)
  expr: Constraints[15] = .Constraints.hauteur * 0.1
  expr: Constraints[27] = .Constraints.epaisseur
  sketch-geometry (12):
    g0: LineSegment StartX=-10 StartY=12.5 StartZ=0 EndX=10 EndY=12.5 EndZ=0
    g1: LineSegment StartX=12.5 StartY=10 StartZ=0 EndX=12.5 EndY=-10 EndZ=0
    g2: LineSegment StartX=10 StartY=-12.5 StartZ=0 EndX=-10 EndY=-12.5 EndZ=0
    g3: LineSegment StartX=-12.5 StartY=-10 StartZ=0 EndX=-12.5 EndY=10 EndZ=0
    g4: ArcOfCircle CenterX=-10 CenterY=10 CenterZ=0 NormalX=0 NormalY=0 NormalZ=1 AngleXU=0 Radius=2.5 StartAngle=1.5708 EndAngle=3.14159
    g5: ArcOfCircle CenterX=10 CenterY=10 CenterZ=0 NormalX=0 NormalY=0 NormalZ=1 AngleXU=0 Radius=2.5 StartAngle=2e-16 EndAngle=1.5708
    g6: ArcOfCircle CenterX=10 CenterY=-10 CenterZ=0 NormalX=0 NormalY=0 NormalZ=1 AngleXU=0 Radius=2.5 StartAngle=4.71239 EndAngle=6.28319
    g7: ArcOfCircle CenterX=-10 CenterY=-10 CenterZ=0 NormalX=0 NormalY=0 NormalZ=1 AngleXU=0 Radius=2.5 StartAngle=3.14159 EndAngle=4.71239
    g8: LineSegment StartX=-10.5 StartY=10.5 StartZ=0 EndX=10.5 EndY=10.5 EndZ=0
    g9: LineSegment StartX=10.5 StartY=10.5 StartZ=0 EndX=10.5 EndY=-10.5 EndZ=0
    g10: LineSegment StartX=10.5 StartY=-10.5 StartZ=0 EndX=-10.5 EndY=-10.5 EndZ=0
    g11: LineSegment StartX=-10.5 StartY=-10.5 StartZ=0 EndX=-10.5 EndY=10.5 EndZ=0
  constraints (28):
    c: Horizontal(g2)
    c: Vertical(g3)
    c: Tangent(g0,g4) = 1.5708
    c: Tangent(g3,g4) = 1.5708
    c: Tangent(g0,g5) = 1.5708
    c: Tangent(g1,g5) = 1.5708
    c: Tangent(g1,g6) = 1.5708
    c: Tangent(g2,g6) = 1.5708
    c: Tangent(g2,g7) = 1.5708
    c: Tangent(g3,g7) = 1.5708
    c: Equal(g4,g5)
    c: DistanceY(g2,g0) = 25  'hauteur'
    c: DistanceX(g3,g1) = 25  'largeur'
    c: Equal(g5,g6)
    c: Equal(g6,g7)
    c: Radius(g7) = 2.5
    c: Symmetric(g1,g1,g-1)
    c: Symmetric(g0,g0,g-2)
    c: Coincident(g8,g9)
    c: Coincident(g9,g10)
    c: Coincident(g10,g11)
    c: Coincident(g11,g8)
    c: Horizontal(g10)
    c: Vertical(g11)
    c: Symmetric(g8,g9,g-1)
    c: Symmetric(g8,g8,g-2)
    c: DistanceX(g3,g8) = 2  'epaisseur'
    c: DistanceY(g2,g9) = 2
FEATURE [PartDesign::Pad] Pad004
  Direction = (1,1e-16,-1e-16)
  Length = 420
  Length2 = 100
  Placement = pos=(0,0,0) rot=(0.57735,0.57735,0.57735;2.0944rad)
  Profile = -> Sketch008
  Suppressed = false
  Type = 0
  expr: Length = Spreadsheet.D4 - Spreadsheet.B9 * 2
FEATURE [PartDesign::Body] Body006
  AllowCompound = false
  Group = -> [Sketch008,Pad004]
  Origin = -> Origin014
  Tip = -> Pad004
FEATURE [App::Part] A6
  Group = -> [LCS_0006,Body006]
  Nom_de_la_piece = 'A6
  Origin = -> Origin013
  Reference_AP = Tube carré 25 x 2
  longueur = 420
FEATURE [App::Link] A6001
  AssemblyType = Asm4EE
  AttachedBy = #LCS_0006
  AttachedTo = A5001#renfort
  AttachmentOffset = pos=(0,0,0) rot=(0,1,0;4.71239rad)
  LinkPlacement = pos=(1005,-210,-283.5) rot=(0.57735,0.57735,-0.57735;4.18879rad)
  LinkedObject = -> A6
  Placement = pos=(1005,-210,-283.5) rot=(0.57735,0.57735,-0.57735;4.18879rad)
  expr: Placement = A5001.Placement * renfort.Placement * AttachmentOffset * LCS_0006.Placement ^ -1
FEATURE [PartDesign::Body] A1005
  AllowCompound = false
  Origin = -> Origin015
FEATURE [PartDesign::CoordinateSystem] LCS_0007
  AttacherType = Attacher::AttachEngine3D
  AttachmentSupport = -> [X_Axis002]
  MapMode = 2
FEATURE [PartDesign::CoordinateSystem] cote2
  AttacherType = Attacher::AttachEngine3D
  AttachmentSupport = -> [Pad]
  MapMode = 5
  Placement = pos=(2285,1.0054e-12,0) rot=(0.57735,0.57735,0.57735;2.0944rad)
FEATURE [PartDesign::CoordinateSystem] faceA1
  AttacherType = Attacher::AttachEngine3D
  AttachmentOffset = pos=(12.5,980,0) rot=(0,0,1;0rad)
  AttachmentSupport = -> [Pad]
  MapMode = 5
  Placement = pos=(980,-12.5,-12.5) rot=(0.57735,0.57735,-0.57735;2.0944rad)
  expr: .AttachmentOffset.Base.x = Spreadsheet.B2 / 2
  expr: .AttachmentOffset.Base.y = (Spreadsheet.B4 - Spreadsheet.B2 * 2) / 2
FEATURE [PartDesign::CoordinateSystem] face2A1
  AttacherType = Attacher::AttachEngine3D
  AttachmentOffset = pos=(-12.5,980,0) rot=(0,0,1;0rad)
  AttachmentSupport = -> [Pad]
  MapMode = 5
  Placement = pos=(980,12.5,-12.5) rot=(0.57735,0.57735,0.57735;4.18879rad)
  expr: .AttachmentOffset.Base.x = -Spreadsheet.B2 / 2
  expr: .AttachmentOffset.Base.y = (Spreadsheet.B4 - Spreadsheet.B2 * 2) / 2
FEATURE [App::Part] A1
  Group = -> [A1005,LCS_0007,faceA1,face2A1,Pad,Sketch,cote2,LCS_0]
  Nom_de_la_piece = 'A1
  Origin = -> Origin002
  Reference_AP = Tube carré 25 x 2
  longueur = 2285
FEATURE [PartDesign::CoordinateSystem] LCS_0008
  AttacherType = Attacher::AttachEngine3D
  AttachmentSupport = -> [X_Axis016]
  MapMode = 2
FEATURE [PartDesign::CoordinateSystem] LCS_0010
  AttacherType = Attacher::AttachEngine3D
  AttachmentSupport = -> [X_Axis018]
  MapMode = 2
FEATURE [PartDesign::Body] A7002
  AllowCompound = false
FEATURE [PartDesign::CoordinateSystem] LCS_0011  label="cote004"
  AttacherType = Attacher::AttachEngine3D
  AttachmentSupport = -> [X_Axis018]
  MapMode = 2
FEATURE [Sketcher::SketchObject] Sketch009
  ArcFitTolerance = 0
  FullyConstrained = true
  MakeInternals = false
  MapMode = 5
  Placement = pos=(0,0,0) rot=(0.57735,0.57735,0.57735;2.0944rad)
  expr: Constraints[15] = .Constraints.hauteur * 0.1
  expr: Constraints[27] = .Constraints.epaisseur
  sketch-geometry (12):
    g0: LineSegment StartX=-10 StartY=12.5 StartZ=0 EndX=10 EndY=12.5 EndZ=0
    g1: LineSegment StartX=12.5 StartY=10 StartZ=0 EndX=12.5 EndY=-10 EndZ=0
    g2: LineSegment StartX=10 StartY=-12.5 StartZ=0 EndX=-10 EndY=-12.5 EndZ=0
    g3: LineSegment StartX=-12.5 StartY=-10 StartZ=0 EndX=-12.5 EndY=10 EndZ=0
    g4: ArcOfCircle CenterX=-10 CenterY=10 CenterZ=0 NormalX=0 NormalY=0 NormalZ=1 AngleXU=0 Radius=2.5 StartAngle=1.5708 EndAngle=3.14159
    g5: ArcOfCircle CenterX=10 CenterY=10 CenterZ=0 NormalX=0 NormalY=0 NormalZ=1 AngleXU=0 Radius=2.5 StartAngle=2e-16 EndAngle=1.5708
    g6: ArcOfCircle CenterX=10 CenterY=-10 CenterZ=0 NormalX=0 NormalY=0 NormalZ=1 AngleXU=0 Radius=2.5 StartAngle=4.71239 EndAngle=6.28319
    g7: ArcOfCircle CenterX=-10 CenterY=-10 CenterZ=0 NormalX=0 NormalY=0 NormalZ=1 AngleXU=0 Radius=2.5 StartAngle=3.14159 EndAngle=4.71239
    g8: LineSegment StartX=-10.5 StartY=10.5 StartZ=0 EndX=10.5 EndY=10.5 EndZ=0
    g9: LineSegment StartX=10.5 StartY=10.5 StartZ=0 EndX=10.5 EndY=-10.5 EndZ=0
    g10: LineSegment StartX=10.5 StartY=-10.5 StartZ=0 EndX=-10.5 EndY=-10.5 EndZ=0
    g11: LineSegment StartX=-10.5 StartY=-10.5 StartZ=0 EndX=-10.5 EndY=10.5 EndZ=0
  constraints (28):
    c: Horizontal(g2)
    c: Vertical(g3)
    c: Tangent(g0,g4) = 1.5708
    c: Tangent(g3,g4) = 1.5708
    c: Tangent(g0,g5) = 1.5708
    c: Tangent(g1,g5) = 1.5708
    c: Tangent(g1,g6) = 1.5708
    c: Tangent(g2,g6) = 1.5708
    c: Tangent(g2,g7) = 1.5708
    c: Tangent(g3,g7) = 1.5708
    c: Equal(g4,g5)
    c: DistanceY(g2,g0) = 25  'hauteur'
    c: DistanceX(g3,g1) = 25  'largeur'
    c: Equal(g5,g6)
    c: Equal(g6,g7)
    c: Radius(g7) = 2.5
    c: Symmetric(g1,g1,g-1)
    c: Symmetric(g0,g0,g-2)
    c: Coincident(g8,g9)
    c: Coincident(g9,g10)
    c: Coincident(g10,g11)
    c: Coincident(g11,g8)
    c: Horizontal(g10)
    c: Vertical(g11)
    c: Symmetric(g8,g9,g-1)
    c: Symmetric(g8,g8,g-2)
    c: DistanceX(g3,g8) = 2  'epaisseur'
    c: DistanceY(g2,g9) = 2
FEATURE [PartDesign::Pad] Pad005
  Direction = (1,1e-16,-1e-16)
  Length = 1960
  Length2 = 100
  Placement = pos=(0,0,0) rot=(0.57735,0.57735,0.57735;2.0944rad)
  Profile = -> Sketch009
  Suppressed = false
  Type = 0
  expr: Length = Spreadsheet.B4 - Spreadsheet.B2 * 2
FEATURE [PartDesign::CoordinateSystem] cote003
  AttacherType = Attacher::AttachEngine3D
  AttachmentSupport = -> [Pad005]
  MapMode = 5
  Placement = pos=(1960,8.624e-13,0) rot=(0.57735,0.57735,0.57735;2.0944rad)
FEATURE [PartDesign::CoordinateSystem] faceA002
  AttacherType = Attacher::AttachEngine3D
  AttachmentOffset = pos=(12.5,980,0) rot=(0,0,1;0rad)
  AttachmentSupport = -> [Pad005]
  MapMode = 5
  Placement = pos=(980,-12.5,-12.5) rot=(0.57735,0.57735,-0.57735;2.0944rad)
  expr: .AttachmentOffset.Base.x = Spreadsheet.B2 / 2
  expr: .AttachmentOffset.Base.y = (Spreadsheet.B4 - Spreadsheet.B2 * 2) / 2
FEATURE [PartDesign::CoordinateSystem] face2A002
  AttacherType = Attacher::AttachEngine3D
  AttachmentOffset = pos=(-12.5,980,0) rot=(0,0,1;0rad)
  AttachmentSupport = -> [Pad005]
  MapMode = 5
  Placement = pos=(980,12.5,-12.5) rot=(0.57735,0.57735,0.57735;4.18879rad)
  expr: .AttachmentOffset.Base.x = -Spreadsheet.B2 / 2
  expr: .AttachmentOffset.Base.y = (Spreadsheet.B4 - Spreadsheet.B2 * 2) / 2
FEATURE [App::Part] A7
  Group = -> [LCS_0008,A7002,LCS_0011,LCS_0010,X_Axis018,faceA002,face2A002,Pad005,Sketch009,cote003]
  Nom_de_la_piece = 'A7
  Origin = -> Origin016
  Reference_AP = Tube carré 25 x 2
  longueur = 1960
FEATURE [App::Link] A7003
  AssemblyType = Asm4EE
  AttachedBy = #LCS_0011
  AttachedTo = A2001#face2
  AttachmentOffset = pos=(0,0,0) rot=(0,1,0;4.71239rad)
  LinkPlacement = pos=(25,-97.5,-1.52e-14) rot=(0,0,1;0rad)
  LinkedObject = -> A7
  Placement = pos=(25,-97.5,-1.52e-14) rot=(0,0,1;0rad)
  expr: Placement = A2001.Placement * face2.Placement * AttachmentOffset * LCS_0011.Placement ^ -1
FEATURE [App::Link] A7004
  AssemblyType = Asm4EE
  AttachedBy = #LCS_0011
  AttachedTo = A2001#face3A2
  AttachmentOffset = pos=(0,0,0) rot=(0,1,0;4.71239rad)
  LinkPlacement = pos=(25,97.5,1e-16) rot=(0,0,1;0rad)
  LinkedObject = -> A7
  Placement = pos=(25,97.5,1e-16) rot=(0,0,1;0rad)
  expr: Placement = A2001.Placement * face3A2.Placement * AttachmentOffset * LCS_0011.Placement ^ -1
FEATURE [PartDesign::CoordinateSystem] LCS_0012
  AttacherType = Attacher::AttachEngine3D
  AttachmentSupport = -> [X_Axis019]
  MapMode = 2
FEATURE [PartDesign::CoordinateSystem] LCS_0013
  AttacherType = Attacher::AttachEngine3D
  AttachmentSupport = -> [X_Axis020]
  MapMode = 2
FEATURE [PartDesign::Body] A8001
  AllowCompound = false
  Group = -> [LCS_0013]
  Origin = -> Origin018
FEATURE [Sketcher::SketchObject] Sketch010
  ArcFitTolerance = 0
  FullyConstrained = true
  MakeInternals = false
  MapMode = 5
  expr: Constraints[15] = .Constraints.hauteur * 0.1
  expr: Constraints[27] = .Constraints.epaisseur
  sketch-geometry (12):
    g0: LineSegment StartX=-10 StartY=12.5 StartZ=0 EndX=10 EndY=12.5 EndZ=0
    g1: LineSegment StartX=12.5 StartY=10 StartZ=0 EndX=12.5 EndY=-10 EndZ=0
    g2: LineSegment StartX=10 StartY=-12.5 StartZ=0 EndX=-10 EndY=-12.5 EndZ=0
    g3: LineSegment StartX=-12.5 StartY=-10 StartZ=0 EndX=-12.5 EndY=10 EndZ=0
    g4: ArcOfCircle CenterX=-10 CenterY=10 CenterZ=0 NormalX=0 NormalY=0 NormalZ=1 AngleXU=0 Radius=2.5 StartAngle=1.5708 EndAngle=3.14159
    g5: ArcOfCircle CenterX=10 CenterY=10 CenterZ=0 NormalX=0 NormalY=0 NormalZ=1 AngleXU=0 Radius=2.5 StartAngle=2e-16 EndAngle=1.5708
    g6: ArcOfCircle CenterX=10 CenterY=-10 CenterZ=0 NormalX=0 NormalY=0 NormalZ=1 AngleXU=0 Radius=2.5 StartAngle=4.71239 EndAngle=6.28319
    g7: ArcOfCircle CenterX=-10 CenterY=-10 CenterZ=0 NormalX=0 NormalY=0 NormalZ=1 AngleXU=0 Radius=2.5 StartAngle=3.14159 EndAngle=4.71239
    g8: LineSegment StartX=-10.5 StartY=10.5 StartZ=0 EndX=10.5 EndY=10.5 EndZ=0
    g9: LineSegment StartX=10.5 StartY=10.5 StartZ=0 EndX=10.5 EndY=-10.5 EndZ=0
    g10: LineSegment StartX=10.5 StartY=-10.5 StartZ=0 EndX=-10.5 EndY=-10.5 EndZ=0
    g11: LineSegment StartX=-10.5 StartY=-10.5 StartZ=0 EndX=-10.5 EndY=10.5 EndZ=0
  constraints (28):
    c: Horizontal(g2)
    c: Vertical(g3)
    c: Tangent(g0,g4) = 1.5708
    c: Tangent(g3,g4) = 1.5708
    c: Tangent(g0,g5) = 1.5708
    c: Tangent(g1,g5) = 1.5708
    c: Tangent(g1,g6) = 1.5708
    c: Tangent(g2,g6) = 1.5708
    c: Tangent(g2,g7) = 1.5708
    c: Tangent(g3,g7) = 1.5708
    c: Equal(g4,g5)
    c: DistanceY(g2,g0) = 25  'hauteur'
    c: DistanceX(g3,g1) = 25  'largeur'
    c: Equal(g5,g6)
    c: Equal(g6,g7)
    c: Radius(g7) = 2.5
    c: Symmetric(g1,g1,g-1)
    c: Symmetric(g0,g0,g-2)
    c: Coincident(g8,g9)
    c: Coincident(g9,g10)
    c: Coincident(g10,g11)
    c: Coincident(g11,g8)
    c: Horizontal(g10)
    c: Vertical(g11)
    c: Symmetric(g8,g9,g-1)
    c: Symmetric(g8,g8,g-2)
    c: DistanceX(g3,g8) = 2  'epaisseur'
    c: DistanceY(g2,g9) = 2
FEATURE [PartDesign::Pad] Pad006
  Direction = (0,0,1)
  Length = 560
  Length2 = 100
  Profile = -> Sketch010
  Suppressed = false
  Type = 0
  expr: Length = Spreadsheet.D4 - Spreadsheet.B2 * 2
FEATURE [PartDesign::CoordinateSystem] face2A8
  AttacherType = Attacher::AttachEngine3D
  AttachmentOffset = pos=(0,182.5,0) rot=(0,0,1;0rad)
  AttachmentSupport = -> [Pad006]
  MapMode = 5
  Placement = pos=(12.5,0,182.5) rot=(0.57735,0.57735,0.57735;2.0944rad)
  expr: .AttachmentOffset.Base.y = (Spreadsheet.D4 - Spreadsheet.B2) * 1 / 3 - Spreadsheet.B2 / 2
FEATURE [App::Link] A8002
  AssemblyType = Asm4EE
  AttachedBy = #face2A8
  AttachedTo = A7003#cote003
  AttachmentOffset = pos=(0,0,0) rot=(-0.707107,-0.707107,0;3.14159rad)
  LinkPlacement = pos=(1997.5,-280,4.322e-13) rot=(0,0.707107,0.707107;3.14159rad)
  LinkedObject = -> A8
  Placement = pos=(1997.5,-280,4.322e-13) rot=(0,0.707107,0.707107;3.14159rad)
  expr: Placement = A7003.Placement * cote003.Placement * AttachmentOffset * face2A8.Placement ^ -1
FEATURE [Sketcher::SketchObject] Sketch011
  ArcFitTolerance = 0
  FullyConstrained = true
  MakeInternals = false
  MapMode = 5
  expr: Constraints[15] = .Constraints.hauteur * 0.1
  expr: Constraints[27] = .Constraints.epaisseur
  sketch-geometry (12):
    g0: LineSegment StartX=-10 StartY=12.5 StartZ=0 EndX=10 EndY=12.5 EndZ=0
    g1: LineSegment StartX=12.5 StartY=10 StartZ=0 EndX=12.5 EndY=-10 EndZ=0
    g2: LineSegment StartX=10 StartY=-12.5 StartZ=0 EndX=-10 EndY=-12.5 EndZ=0
    g3: LineSegment StartX=-12.5 StartY=-10 StartZ=0 EndX=-12.5 EndY=10 EndZ=0
    g4: ArcOfCircle CenterX=-10 CenterY=10 CenterZ=0 NormalX=0 NormalY=0 NormalZ=1 AngleXU=0 Radius=2.5 StartAngle=1.5708 EndAngle=3.14159
    g5: ArcOfCircle CenterX=10 CenterY=10 CenterZ=0 NormalX=0 NormalY=0 NormalZ=1 AngleXU=0 Radius=2.5 StartAngle=2e-16 EndAngle=1.5708
    g6: ArcOfCircle CenterX=10 CenterY=-10 CenterZ=0 NormalX=0 NormalY=0 NormalZ=1 AngleXU=0 Radius=2.5 StartAngle=4.71239 EndAngle=6.28319
    g7: ArcOfCircle CenterX=-10 CenterY=-10 CenterZ=0 NormalX=0 NormalY=0 NormalZ=1 AngleXU=0 Radius=2.5 StartAngle=3.14159 EndAngle=4.71239
    g8: LineSegment StartX=-10.5 StartY=10.5 StartZ=0 EndX=10.5 EndY=10.5 EndZ=0
    g9: LineSegment StartX=10.5 StartY=10.5 StartZ=0 EndX=10.5 EndY=-10.5 EndZ=0
    g10: LineSegment StartX=10.5 StartY=-10.5 StartZ=0 EndX=-10.5 EndY=-10.5 EndZ=0
    g11: LineSegment StartX=-10.5 StartY=-10.5 StartZ=0 EndX=-10.5 EndY=10.5 EndZ=0
  constraints (28):
    c: Horizontal(g2)
    c: Vertical(g3)
    c: Tangent(g0,g4) = 1.5708
    c: Tangent(g3,g4) = 1.5708
    c: Tangent(g0,g5) = 1.5708
    c: Tangent(g1,g5) = 1.5708
    c: Tangent(g1,g6) = 1.5708
    c: Tangent(g2,g6) = 1.5708
    c: Tangent(g2,g7) = 1.5708
    c: Tangent(g3,g7) = 1.5708
    c: Equal(g4,g5)
    c: DistanceY(g2,g0) = 25  'hauteur'
    c: DistanceX(g3,g1) = 25  'largeur'
    c: Equal(g5,g6)
    c: Equal(g6,g7)
    c: Radius(g7) = 2.5
    c: Symmetric(g1,g1,g-1)
    c: Symmetric(g0,g0,g-2)
    c: Coincident(g8,g9)
    c: Coincident(g9,g10)
    c: Coincident(g10,g11)
    c: Coincident(g11,g8)
    c: Horizontal(g10)
    c: Vertical(g11)
    c: Symmetric(g8,g9,g-1)
    c: Symmetric(g8,g8,g-2)
    c: DistanceX(g3,g8) = 2  'epaisseur'
    c: DistanceY(g2,g9) = 2
FEATURE [PartDesign::Pad] Pad007
  Direction = (0,0,1)
  Length = 215
  Length2 = 100
  Profile = -> Sketch011
  Suppressed = false
  Type = 0
  expr: Length = Spreadsheet.B11 - Spreadsheet.B5 - Spreadsheet.B2 * 2
FEATURE [PartDesign::CoordinateSystem] LCS_0014
  AttacherType = Attacher::AttachEngine3D
  AttachmentSupport = -> [X_Axis021]
  MapMode = 2
FEATURE [PartDesign::CoordinateSystem] LCS_0015
  AttacherType = Attacher::AttachEngine3D
  AttachmentOffset = pos=(0,-12.5,0) rot=(0,0,1;0rad)
  AttachmentSupport = -> [X_Axis022]
  MapMode = 2
  Placement = pos=(0,-12.5,0) rot=(0,0,1;0rad)
  expr: .AttachmentOffset.Base.y = -Spreadsheet.B2 / 2
FEATURE [PartDesign::CoordinateSystem] cote2001
  AttacherType = Attacher::AttachEngine3D
  AttachmentOffset = pos=(0,12.5,8.29156) rot=(0,0,1;0rad)
  AttachmentSupport = -> [Pad007]
  MapMode = 5
  Placement = pos=(0,12.5,223.292) rot=(0,0,1;0rad)
  expr: .AttachmentOffset.Base.y = Spreadsheet.B2 / 2
  expr: .AttachmentOffset.Base.z = Sketch023.Constraints.deport
FEATURE [App::Link] A9  label="A8005"
  AssemblyType = Asm4EE
  AttachedBy = #LCS_0015
  AttachedTo = A1001#cote2
  AttachmentOffset = pos=(0,12.5,0) rot=(-1,0,0;1.5708rad)
  LinkPlacement = pos=(2297.5,-292.5,12.5) rot=(0,0,1;1.5708rad)
  LinkedObject = -> A8003
  Placement = pos=(2297.5,-292.5,12.5) rot=(0,0,1;1.5708rad)
  expr: .AttachmentOffset.Base.y = Spreadsheet.B2 / 2
  expr: Placement = A1001.Placement * cote2.Placement * AttachmentOffset * LCS_0015.Placement ^ -1
FEATURE [App::Link] A9001
  AssemblyType = Asm4EE
  AttachedBy = #LCS_0015
  AttachedTo = A1004#cote2
  AttachmentOffset = pos=(0,12.5,0) rot=(-1,0,0;1.5708rad)
  LinkPlacement = pos=(2297.5,292.5,12.5) rot=(0,0,1;1.5708rad)
  LinkedObject = -> A8003
  Placement = pos=(2297.5,292.5,12.5) rot=(0,0,1;1.5708rad)
  expr: .AttachmentOffset.Base.y = Spreadsheet.B2 / 2
  expr: Placement = A1004.Placement * cote2.Placement * AttachmentOffset * LCS_0015.Placement ^ -1
FEATURE [Sketcher::SketchObject] Sketch012
  ArcFitTolerance = 0
  AttachmentSupport = -> [XZ_Plane022]
  FullyConstrained = true
  MakeInternals = false
  MapMode = 5
  Placement = pos=(0,0,0) rot=(1,0,0;1.5708rad)
  sketch-geometry (1):
    g0: Circle CenterX=0 CenterY=0 CenterZ=0 NormalX=0 NormalY=0 NormalZ=1 AngleXU=0 Radius=12.5
  constraints (2):
    c: Coincident(g0,g-1)
    c: Diameter(g0) = 25  'diametre'
FEATURE [PartDesign::Pad] Pad008
  Direction = (0,-1,2e-16)
  Length = 150
  Length2 = 100
  Placement = pos=(0,0,0) rot=(1,0,0;1.5708rad)
  Profile = -> Sketch012
  Suppressed = false
  Type = 0
FEATURE [Sketcher::SketchObject] Sketch013
  ArcFitTolerance = 0
  AttachmentSupport = -> [XZ_Plane024]
  FullyConstrained = true
  MakeInternals = false
  MapMode = 5
  Placement = pos=(0,0,0) rot=(1,0,0;1.5708rad)
  expr: Constraints[22] = .Constraints.epaisseur
  expr: Constraints[24] = .Constraints.largeur * 20 / 100
  sketch-geometry (10):
    g0: LineSegment StartX=-15 StartY=15 StartZ=0 EndX=-15 EndY=0 EndZ=0
    g1: LineSegment StartX=-15 StartY=0 StartZ=0 EndX=15 EndY=0 EndZ=0
    g2: LineSegment StartX=15 StartY=0 StartZ=0 EndX=15 EndY=15 EndZ=0
    g3: LineSegment StartX=15 StartY=15 StartZ=0 EndX=14 EndY=15 EndZ=0
    g4: LineSegment StartX=11 StartY=12 StartZ=0 EndX=11 EndY=4 EndZ=0
    g5: LineSegment StartX=11 StartY=4 StartZ=0 EndX=-11 EndY=4 EndZ=0
    g6: LineSegment StartX=-11 StartY=4 StartZ=0 EndX=-11 EndY=12 EndZ=0
    g7: LineSegment StartX=-14 StartY=15 StartZ=0 EndX=-15 EndY=15 EndZ=0
    g8: ArcOfCircle CenterX=-14 CenterY=12 CenterZ=0 NormalX=0 NormalY=0 NormalZ=1 AngleXU=0 Radius=3 StartAngle=0 EndAngle=1.5708
    g9: ArcOfCircle CenterX=14 CenterY=12 CenterZ=0 NormalX=0 NormalY=0 NormalZ=1 AngleXU=0 Radius=3 StartAngle=1.5708 EndAngle=3.14159
  constraints (25):
    c: PointOnObject(g0,g-1)
    c: Vertical(g0)
    c: Coincident(g0,g1)
    c: Coincident(g1,g2)
    c: Coincident(g2,g3)
    c: Horizontal(g3)
    c: Vertical(g4)
    c: Coincident(g4,g5)
    c: Coincident(g5,g6)
    c: Coincident(g7,g0)
    c: Horizontal(g7)
    c: Symmetric(g1,g0,g-2)
    c: Symmetric(g5,g4,g-2)
    c: Tangent(g6,g8) = -1.5708
    c: Tangent(g7,g8) = -1.5708
    c: Tangent(g3,g9) = -1.5708
    c: Tangent(g4,g9) = -1.5708
    c: Equal(g8,g9)
    c: Symmetric(g0,g2,g-2)
    c: Vertical(g6)
    c: DistanceX(g1,g1) = 30  'largeur'
    c: DistanceY(g2,g2) = 15  'hauteur'
    c: DistanceY(g1,g4) = 4
    c: DistanceX(g4,g1) = 4  'epaisseur'
    c: Diameter(g8) = 6
FEATURE [PartDesign::Pad] Pad009
  Direction = (0,-1,2e-16)
  Length = 46
  Length2 = 100
  Placement = pos=(0,0,0) rot=(1,0,0;1.5708rad)
  Profile = -> Sketch013
  Suppressed = false
  Type = 0
FEATURE [PartDesign::Body] Body007
  AllowCompound = false
  Group = -> [Sketch013,Pad009]
  Origin = -> Origin024
  Tip = -> Pad009
FEATURE [Sketcher::SketchObject] Sketch014
  ArcFitTolerance = 0
  FullyConstrained = false
  MakeInternals = false
  Placement = pos=(0,-305,0) rot=(1,0,0;1.5708rad)
  expr: .Constraints.hpied = Spreadsheet.B5 - 100
  expr: Constraints[12] = .Constraints.lar / 2
  expr: Constraints[15] = Spreadsheet.B2
  expr: Constraints[33] = Pad003.Length
  expr: Constraints[5] = Spreadsheet.B2 / 2
  expr: Constraints[7] = Spreadsheet.B2
  sketch-geometry (14):
    g0: LineSegment StartX=25 StartY=-12.5 StartZ=0 EndX=25 EndY=-412.5 EndZ=0
    g1: LineSegment StartX=25 StartY=-412.5 StartZ=0 EndX=273.106 EndY=-37.5 EndZ=0
    g2: LineSegment StartX=1736.89 StartY=-37.5 StartZ=0 EndX=1985 EndY=-412.5 EndZ=0
    g3: LineSegment StartX=1985 StartY=-412.5 StartZ=0 EndX=1985 EndY=-12.5 EndZ=0
    g4: LineSegment [constr] StartX=-267.829 StartY=-37.5 StartZ=0 EndX=2303.14 EndY=-37.5 EndZ=0
    g5: LineSegment [constr] StartX=1005 StartY=302.788 StartZ=0 EndX=1005 EndY=-538.691 EndZ=0
    g6: LineSegment StartX=1017.5 StartY=-269.453 StartZ=0 EndX=1736.89 EndY=-12.5 EndZ=0
    g7: LineSegment StartX=992.5 StartY=-269.453 StartZ=0 EndX=273.106 EndY=-12.5 EndZ=0
    g8: LineSegment StartX=1985 StartY=-412.5 StartZ=0 EndX=2216.18 EndY=-12.5 EndZ=0
    g9: LineSegment [constr] StartX=1736.89 StartY=-37.5 StartZ=0 EndX=1736.89 EndY=33.5143 EndZ=0
    g10: LineSegment [constr] StartX=1017.5 StartY=-296 StartZ=0 EndX=1200.58 EndY=-230.607 EndZ=0
    g11: LineSegment [constr] StartX=1017.5 StartY=-269.453 StartZ=0 EndX=1017.5 EndY=-296 EndZ=0
    g12: GeomPoint [constr] X=248.106 Y=-12.5 Z=0
    g13: LineSegment [constr] StartX=1017.5 StartY=-269.453 StartZ=0 EndX=1025.91 EndY=-292.996 EndZ=0
  constraints (40):
    c: Vertical(g0)
    c: Coincident(g0,g1)
    c: Coincident(g2,g3)
    c: Vertical(g3)
    c: Equal(g0,g3)
    c: DistanceY(g0,g-1) = 12.5
    c: DistanceX(g0,g2) = 1960  'lar'
    c: DistanceX(g-1,g0) = 25
    c: DistanceY(g0,g0) = 400  'hpied'
    c: Horizontal(g4)
    c: PointOnObject(g1,g4)
    c: PointOnObject(g2,g4)
    c: DistanceX(g0,g5) = 980
    c: Symmetric(g1,g2,g5)
    c: Symmetric(g7,g6,g5)
    c: DistanceX(g7,g6) = 25
    c: Distance(g1) = 449.646  'lpied'
    c: Distance(g6) = 763.906  'ldiag'
    c: Angle(g3,g2) = 0.584499  'angle'
    c: Angle(g5,g7) = 1.22774  'anglerou'
    c: DistanceX(g-1,g2) = 1736.89  'b2'
    c: Coincident(g8,g2)
    c: Angle(g8,g3) = 0.524048  'angle2'
    c: Distance(g8) = 462  'l2pied'
    c: Symmetric(g7,g6,g5)
    c: Vertical(g9)
    c: PointOnObject(g6,g9)
    c: Coincident(g9,g2)
    c: Parallel(g6,g10)
    c: Distance(g10,g6) = 25
    c: Coincident(g11,g6)
    c: Coincident(g11,g10)
    c: Vertical(g11)
    c: Distance(g10,g4) = 258.5
    c: Distance(g12,g7) = 25
    c: Distance(g12,g-2) = 248.106  'b1'
    c: Coincident(g13,g6)
    c: PointOnObject(g13,g10)
    c: Perpendicular(g13,g10)
    c: Distance(g10,g13) = 8.92951  'rajoueroue'
FEATURE [PartDesign::Body] Body008
  AllowCompound = false
  Origin = -> Origin028
FEATURE [Sketcher::SketchObject] Sketch015
  ArcFitTolerance = 0
  FullyConstrained = true
  MakeInternals = false
  MapMode = 5
  Placement = pos=(0,0,0) rot=(0.57735,0.57735,0.57735;2.0944rad)
  expr: Constraints[15] = .Constraints.hauteur * 0.1
  expr: Constraints[27] = .Constraints.epaisseur
  sketch-geometry (12):
    g0: LineSegment StartX=-10 StartY=12.5 StartZ=0 EndX=10 EndY=12.5 EndZ=0
    g1: LineSegment StartX=12.5 StartY=10 StartZ=0 EndX=12.5 EndY=-10 EndZ=0
    g2: LineSegment StartX=10 StartY=-12.5 StartZ=0 EndX=-10 EndY=-12.5 EndZ=0
    g3: LineSegment StartX=-12.5 StartY=-10 StartZ=0 EndX=-12.5 EndY=10 EndZ=0
    g4: ArcOfCircle CenterX=-10 CenterY=10 CenterZ=0 NormalX=0 NormalY=0 NormalZ=1 AngleXU=0 Radius=2.5 StartAngle=1.5708 EndAngle=3.14159
    g5: ArcOfCircle CenterX=10 CenterY=10 CenterZ=0 NormalX=0 NormalY=0 NormalZ=1 AngleXU=0 Radius=2.5 StartAngle=2e-16 EndAngle=1.5708
    g6: ArcOfCircle CenterX=10 CenterY=-10 CenterZ=0 NormalX=0 NormalY=0 NormalZ=1 AngleXU=0 Radius=2.5 StartAngle=4.71239 EndAngle=6.28319
    g7: ArcOfCircle CenterX=-10 CenterY=-10 CenterZ=0 NormalX=0 NormalY=0 NormalZ=1 AngleXU=0 Radius=2.5 StartAngle=3.14159 EndAngle=4.71239
    g8: LineSegment StartX=-10.5 StartY=10.5 StartZ=0 EndX=10.5 EndY=10.5 EndZ=0
    g9: LineSegment StartX=10.5 StartY=10.5 StartZ=0 EndX=10.5 EndY=-10.5 EndZ=0
    g10: LineSegment StartX=10.5 StartY=-10.5 StartZ=0 EndX=-10.5 EndY=-10.5 EndZ=0
    g11: LineSegment StartX=-10.5 StartY=-10.5 StartZ=0 EndX=-10.5 EndY=10.5 EndZ=0
  constraints (28):
    c: Horizontal(g2)
    c: Vertical(g3)
    c: Tangent(g0,g4) = 1.5708
    c: Tangent(g3,g4) = 1.5708
    c: Tangent(g0,g5) = 1.5708
    c: Tangent(g1,g5) = 1.5708
    c: Tangent(g1,g6) = 1.5708
    c: Tangent(g2,g6) = 1.5708
    c: Tangent(g2,g7) = 1.5708
    c: Tangent(g3,g7) = 1.5708
    c: Equal(g4,g5)
    c: DistanceY(g2,g0) = 25  'hauteur'
    c: DistanceX(g3,g1) = 25  'largeur'
    c: Equal(g5,g6)
    c: Equal(g6,g7)
    c: Radius(g7) = 2.5
    c: Symmetric(g1,g1,g-1)
    c: Symmetric(g0,g0,g-2)
    c: Coincident(g8,g9)
    c: Coincident(g9,g10)
    c: Coincident(g10,g11)
    c: Coincident(g11,g8)
    c: Horizontal(g10)
    c: Vertical(g11)
    c: Symmetric(g8,g9,g-1)
    c: Symmetric(g8,g8,g-2)
    c: DistanceX(g3,g8) = 2  'epaisseur'
    c: DistanceY(g2,g9) = 2
FEATURE [PartDesign::Pad] Pad010
  Direction = (1,1e-16,-1e-16)
  Length = 400
  Length2 = 100
  Placement = pos=(0,0,0) rot=(0.57735,0.57735,0.57735;2.0944rad)
  Profile = -> Sketch015
  Suppressed = false
  Type = 0
  expr: Length = Sketch014.Constraints.hpied
FEATURE [Sketcher::SketchObject] Sketch016
  ArcFitTolerance = 0
  FullyConstrained = true
  MakeInternals = false
  MapMode = 5
  Placement = pos=(0,0,0) rot=(0.57735,0.57735,0.57735;2.0944rad)
  expr: Constraints[15] = .Constraints.hauteur * 0.1
  expr: Constraints[27] = .Constraints.epaisseur
  sketch-geometry (12):
    g0: LineSegment StartX=-10 StartY=12.5 StartZ=0 EndX=10 EndY=12.5 EndZ=0
    g1: LineSegment StartX=12.5 StartY=10 StartZ=0 EndX=12.5 EndY=-10 EndZ=0
    g2: LineSegment StartX=10 StartY=-12.5 StartZ=0 EndX=-10 EndY=-12.5 EndZ=0
    g3: LineSegment StartX=-12.5 StartY=-10 StartZ=0 EndX=-12.5 EndY=10 EndZ=0
    g4: ArcOfCircle CenterX=-10 CenterY=10 CenterZ=0 NormalX=0 NormalY=0 NormalZ=1 AngleXU=0 Radius=2.5 StartAngle=1.5708 EndAngle=3.14159
    g5: ArcOfCircle CenterX=10 CenterY=10 CenterZ=0 NormalX=0 NormalY=0 NormalZ=1 AngleXU=0 Radius=2.5 StartAngle=2e-16 EndAngle=1.5708
    g6: ArcOfCircle CenterX=10 CenterY=-10 CenterZ=0 NormalX=0 NormalY=0 NormalZ=1 AngleXU=0 Radius=2.5 StartAngle=4.71239 EndAngle=6.28319
    g7: ArcOfCircle CenterX=-10 CenterY=-10 CenterZ=0 NormalX=0 NormalY=0 NormalZ=1 AngleXU=0 Radius=2.5 StartAngle=3.14159 EndAngle=4.71239
    g8: LineSegment StartX=-10.5 StartY=10.5 StartZ=0 EndX=10.5 EndY=10.5 EndZ=0
    g9: LineSegment StartX=10.5 StartY=10.5 StartZ=0 EndX=10.5 EndY=-10.5 EndZ=0
    g10: LineSegment StartX=10.5 StartY=-10.5 StartZ=0 EndX=-10.5 EndY=-10.5 EndZ=0
    g11: LineSegment StartX=-10.5 StartY=-10.5 StartZ=0 EndX=-10.5 EndY=10.5 EndZ=0
  constraints (28):
    c: Horizontal(g2)
    c: Vertical(g3)
    c: Tangent(g0,g4) = 1.5708
    c: Tangent(g3,g4) = 1.5708
    c: Tangent(g0,g5) = 1.5708
    c: Tangent(g1,g5) = 1.5708
    c: Tangent(g1,g6) = 1.5708
    c: Tangent(g2,g6) = 1.5708
    c: Tangent(g2,g7) = 1.5708
    c: Tangent(g3,g7) = 1.5708
    c: Equal(g4,g5)
    c: DistanceY(g2,g0) = 25  'hauteur'
    c: DistanceX(g3,g1) = 25  'largeur'
    c: Equal(g5,g6)
    c: Equal(g6,g7)
    c: Radius(g7) = 2.5
    c: Symmetric(g1,g1,g-1)
    c: Symmetric(g0,g0,g-2)
    c: Coincident(g8,g9)
    c: Coincident(g9,g10)
    c: Coincident(g10,g11)
    c: Coincident(g11,g8)
    c: Horizontal(g10)
    c: Vertical(g11)
    c: Symmetric(g8,g9,g-1)
    c: Symmetric(g8,g8,g-2)
    c: DistanceX(g3,g8) = 2  'epaisseur'
    c: DistanceY(g2,g9) = 2
FEATURE [PartDesign::Pad] Pad011
  Direction = (1,1e-16,-1e-16)
  Length = 449.646
  Length2 = 100
  Placement = pos=(0,0,0) rot=(0.57735,0.57735,0.57735;2.0944rad)
  Profile = -> Sketch016
  Suppressed = false
  Type = 0
  expr: Length = Sketch014.Constraints.lpied
FEATURE [Sketcher::SketchObject] Sketch017
  ArcFitTolerance = 0
  FullyConstrained = true
  MakeInternals = false
  MapMode = 5
  Placement = pos=(0,0,0) rot=(0.57735,0.57735,0.57735;2.0944rad)
  expr: Constraints[15] = .Constraints.hauteur * 0.1
  expr: Constraints[27] = .Constraints.epaisseur
  sketch-geometry (12):
    g0: LineSegment StartX=-10 StartY=12.5 StartZ=0 EndX=10 EndY=12.5 EndZ=0
    g1: LineSegment StartX=12.5 StartY=10 StartZ=0 EndX=12.5 EndY=-10 EndZ=0
    g2: LineSegment StartX=10 StartY=-12.5 StartZ=0 EndX=-10 EndY=-12.5 EndZ=0
    g3: LineSegment StartX=-12.5 StartY=-10 StartZ=0 EndX=-12.5 EndY=10 EndZ=0
    g4: ArcOfCircle CenterX=-10 CenterY=10 CenterZ=0 NormalX=0 NormalY=0 NormalZ=1 AngleXU=0 Radius=2.5 StartAngle=1.5708 EndAngle=3.14159
    g5: ArcOfCircle CenterX=10 CenterY=10 CenterZ=0 NormalX=0 NormalY=0 NormalZ=1 AngleXU=0 Radius=2.5 StartAngle=2e-16 EndAngle=1.5708
    g6: ArcOfCircle CenterX=10 CenterY=-10 CenterZ=0 NormalX=0 NormalY=0 NormalZ=1 AngleXU=0 Radius=2.5 StartAngle=4.71239 EndAngle=6.28319
    g7: ArcOfCircle CenterX=-10 CenterY=-10 CenterZ=0 NormalX=0 NormalY=0 NormalZ=1 AngleXU=0 Radius=2.5 StartAngle=3.14159 EndAngle=4.71239
    g8: LineSegment StartX=-10.5 StartY=10.5 StartZ=0 EndX=10.5 EndY=10.5 EndZ=0
    g9: LineSegment StartX=10.5 StartY=10.5 StartZ=0 EndX=10.5 EndY=-10.5 EndZ=0
    g10: LineSegment StartX=10.5 StartY=-10.5 StartZ=0 EndX=-10.5 EndY=-10.5 EndZ=0
    g11: LineSegment StartX=-10.5 StartY=-10.5 StartZ=0 EndX=-10.5 EndY=10.5 EndZ=0
  constraints (28):
    c: Horizontal(g2)
    c: Vertical(g3)
    c: Tangent(g0,g4) = 1.5708
    c: Tangent(g3,g4) = 1.5708
    c: Tangent(g0,g5) = 1.5708
    c: Tangent(g1,g5) = 1.5708
    c: Tangent(g1,g6) = 1.5708
    c: Tangent(g2,g6) = 1.5708
    c: Tangent(g2,g7) = 1.5708
    c: Tangent(g3,g7) = 1.5708
    c: Equal(g4,g5)
    c: DistanceY(g2,g0) = 25  'hauteur'
    c: DistanceX(g3,g1) = 25  'largeur'
    c: Equal(g5,g6)
    c: Equal(g6,g7)
    c: Radius(g7) = 2.5
    c: Symmetric(g1,g1,g-1)
    c: Symmetric(g0,g0,g-2)
    c: Coincident(g8,g9)
    c: Coincident(g9,g10)
    c: Coincident(g10,g11)
    c: Coincident(g11,g8)
    c: Horizontal(g10)
    c: Vertical(g11)
    c: Symmetric(g8,g9,g-1)
    c: Symmetric(g8,g8,g-2)
    c: DistanceX(g3,g8) = 2  'epaisseur'
    c: DistanceY(g2,g9) = 2
FEATURE [PartDesign::Pad] Pad012
  Direction = (1,1e-16,-1e-16)
  Length = 772.835
  Length2 = 100
  Placement = pos=(0,0,0) rot=(0.57735,0.57735,0.57735;2.0944rad)
  Profile = -> Sketch017
  ReferenceAxis = -> Sketch017 [N_Axis]
  Suppressed = false
  Type = 0
  expr: Length = Sketch014.Constraints.ldiag + Sketch014.Constraints.rajoueroue
FEATURE [PartDesign::CoordinateSystem] B1
  AttacherType = Attacher::AttachEngine3D
  AttachmentSupport = -> [Pad010]
  MapMode = 5
  Placement = pos=(400,1.76e-13,0) rot=(0.57735,0.57735,0.57735;2.0944rad)
FEATURE [PartDesign::CoordinateSystem] B2
  AttacherType = Attacher::AttachEngine3D
  AttachmentSupport = -> [Pad010]
  MapMode = 5
  Placement = pos=(0,0,0) rot=(0.57735,0.57735,-0.57735;4.18879rad)
FEATURE [PartDesign::CoordinateSystem] B1001
  AttacherType = Attacher::AttachEngine3D
  AttachmentOffset = pos=(0,-12.5,0) rot=(0,0,1;0rad)
  AttachmentSupport = -> [Pad011]
  MapMode = 5
  Placement = pos=(0,0,12.5) rot=(0.57735,0.57735,-0.57735;4.18879rad)
  expr: .AttachmentOffset.Base.y = -12.5
FEATURE [PartDesign::CoordinateSystem] B2001
  AttacherType = Attacher::AttachEngine3D
  AttachmentOffset = pos=(0,12.5,0) rot=(0,0,1;0rad)
  AttachmentSupport = -> [Pad011]
  MapMode = 5
  Placement = pos=(449.646,1.978e-13,12.5) rot=(0.57735,0.57735,0.57735;2.0944rad)
FEATURE [PartDesign::CoordinateSystem] B1002
  AttacherType = Attacher::AttachEngine3D
  AttachmentSupport = -> [Pad012]
  MapMode = 5
  Placement = pos=(0,0,0) rot=(0.57735,0.57735,-0.57735;4.18879rad)
FEATURE [PartDesign::CoordinateSystem] B2002
  AttacherType = Attacher::AttachEngine3D
  AttachmentSupport = -> [Pad012]
  MapMode = 5
  Placement = pos=(772.835,3.4e-13,0) rot=(0.57735,0.57735,0.57735;2.0944rad)
FEATURE [App::Link] A12  label="A9002"
  AssemblyType = Asm4EE
  AttachedBy = #B1
  AttachedTo = A2001#LCS_0001
  AttachmentOffset = pos=(12.5,0,12.5) rot=(0,1,0;3.14159rad)
  LinkPlacement = pos=(12.5,-292.5,-412.5) rot=(-0.707107,0,-0.707107;3.14159rad)
  LinkedObject = -> Part002
  Placement = pos=(12.5,-292.5,-412.5) rot=(-0.707107,0,-0.707107;3.14159rad)
  expr: .AttachmentOffset.Base.x = Spreadsheet.B2 / 2
  expr: .AttachmentOffset.Base.z = Spreadsheet.B2 / 2
  expr: Placement = A2001.Placement * LCS_0001.Placement * AttachmentOffset * B1.Placement ^ -1
FEATURE [App::Link] A12001
  AssemblyType = Asm4EE
  AttachedBy = #B1
  AttachedTo = A2001#cote2A2
  AttachmentOffset = pos=(0,12.5,-12.5) rot=(-0.57735,-0.57735,0.57735;4.18879rad)
  LinkPlacement = pos=(12.5,292.5,-412.5) rot=(0.707107,0,0.707107;3.14159rad)
  LinkedObject = -> Part002
  Placement = pos=(12.5,292.5,-412.5) rot=(0.707107,0,0.707107;3.14159rad)
  expr: .AttachmentOffset.Base.y = Spreadsheet.B2 / 2
  expr: .AttachmentOffset.Base.z = -Spreadsheet.B2 / 2
  expr: Placement = A2001.Placement * cote2A2.Placement * AttachmentOffset * B1.Placement ^ -1
FEATURE [App::Link] A12002  label="A12004"
  AssemblyType = Asm4EE
  AttachedBy = #B1
  AttachedTo = A8002#LCS_0012
  AttachmentOffset = pos=(0,-12.5,-12.5) rot=(-1,0,0;1.5708rad)
  LinkPlacement = pos=(1997.5,-292.5,-412.5) rot=(0.57735,-0.57735,0.57735;2.0944rad)
  LinkedObject = -> Part002
  Placement = pos=(1997.5,-292.5,-412.5) rot=(0.57735,-0.57735,0.57735;2.0944rad)
  expr: .AttachmentOffset.Base.y = -Spreadsheet.B2 / 2
  expr: .AttachmentOffset.Base.z = -Spreadsheet.B2 / 2
  expr: Placement = A8002.Placement * LCS_0012.Placement * AttachmentOffset * B1.Placement ^ -1
FEATURE [PartDesign::CoordinateSystem] cote2002
  AttacherType = Attacher::AttachEngine3D
  AttachmentSupport = -> [Pad006]
  MapMode = 5
  Placement = pos=(0,0,560) rot=(0,0,1;0rad)
FEATURE [App::Part] A8
  Group = -> [LCS_0012,A8001,Pad006,cote2002,Sketch010,face2A8]
  Nom_de_la_piece = 'A8
  Origin = -> Origin017
  Reference_AP = Tube carré 25 x 2
  longueur = 560
FEATURE [App::Link] A12003  label="A12005"
  AssemblyType = Asm4EE
  AttachedBy = #B1
  AttachedTo = A8002#cote2002
  AttachmentOffset = pos=(0,-12.5,12.5) rot=(-1,0,0;1.5708rad)
  LinkPlacement = pos=(1997.5,292.5,-412.5) rot=(0.57735,-0.57735,0.57735;2.0944rad)
  LinkedObject = -> Part002
  Placement = pos=(1997.5,292.5,-412.5) rot=(0.57735,-0.57735,0.57735;2.0944rad)
  expr: .AttachmentOffset.Base.y = -Spreadsheet.B2 / 2
  expr: .AttachmentOffset.Base.z = Spreadsheet.B2 / 2
  expr: Placement = A8002.Placement * cote2002.Placement * AttachmentOffset * B1.Placement ^ -1
FEATURE [App::Link] A13001
  AssemblyType = Asm4EE
  AttachedBy = #B1001
  AttachedTo = A12002#B2
  AttachmentOffset = pos=(12.5,0,0) rot=(-0.276846,-0.276846,0.92017;1.6539rad)
  LinkPlacement = pos=(1995.42,-292.5,-405.603) rot=(0,1,0;4.12789rad)
  LinkedObject = -> Part003
  Placement = pos=(1995.42,-292.5,-405.603) rot=(0,1,0;4.12789rad)
  expr: .AttachmentOffset.Rotation.Roll = -Sketch014.Constraints.angle
  expr: Placement = A12002.Placement * B2.Placement * AttachmentOffset * B1001.Placement ^ -1
FEATURE [App::Link] A14001
  AssemblyType = Asm4EE
  AttachedBy = #B1002
  AttachedTo = A6001#LCS_0006
  AttachmentOffset = pos=(-12.5,0.72,-8.3) rot=(-1,0,0;0.343057rad)
  LinkPlacement = pos=(1013.3,-222.5,-284.22) rot=(0,1,0;5.94013rad)
  LinkedObject = -> Part004
  Placement = pos=(1013.3,-222.5,-284.22) rot=(0,1,0;5.94013rad)
  expr: .AttachmentOffset.Base.x = -Spreadsheet.B2 / 2
  expr: .AttachmentOffset.Rotation.Roll = -(90 ° - Sketch014.Constraints.anglerou)
  expr: Placement = A6001.Placement * LCS_0006.Placement * AttachmentOffset * B1002.Placement ^ -1
FEATURE [App::Link] A2004
  AssemblyType = Asm4EE
  AttachedBy = #LCS_0001
  AttachedTo = A1001#LCS_0
  AttachmentOffset = pos=(235.606,-12.5,-25) rot=(0,0,1;1.5708rad)
  LinkPlacement = pos=(260.606,-305,-25) rot=(0,0,1;1.5708rad)
  LinkedObject = -> A2
  Placement = pos=(260.606,-305,-25) rot=(0,0,1;1.5708rad)
  expr: .AttachmentOffset.Base.x = Sketch014.Constraints.b1 - 1 mm * Spreadsheet.B2 / 2
  expr: .AttachmentOffset.Base.y = -Spreadsheet.B2 / 2
  expr: .AttachmentOffset.Base.z = -Spreadsheet.B2
  expr: Placement = A1001.Placement * LCS_0.Placement * AttachmentOffset * LCS_0001.Placement ^ -1
FEATURE [App::Link] A2005
  AssemblyType = Asm4EE
  AttachedBy = #LCS_0001
  AttachedTo = A2001#LCS_0001
  AttachmentOffset = pos=(0,1736.89,25) rot=(0,0,1;0rad)
  LinkPlacement = pos=(1749.39,-305,-25) rot=(-0.707107,-0.707107,0;3.14159rad)
  LinkedObject = -> A2
  Placement = pos=(1749.39,-305,-25) rot=(-0.707107,-0.707107,0;3.14159rad)
  expr: .AttachmentOffset.Base.y = Sketch014.Constraints.b2
  expr: .AttachmentOffset.Base.z = Spreadsheet.B2
  expr: Placement = A2001.Placement * LCS_0001.Placement * AttachmentOffset * LCS_0001.Placement ^ -1
FEATURE [PartDesign::CoordinateSystem] cote2003
  AttacherType = Attacher::AttachEngine3D
  AttachmentSupport = -> [Pad003]
  MapMode = 5
  Placement = pos=(258.5,1.137e-13,0) rot=(0.57735,0.57735,0.57735;2.0944rad)
FEATURE [App::Part] A5
  Group = -> [LCS_0005,Body005,renfort,Pad003,Sketch007,cote2003]
  Nom_de_la_piece = 'A5
  Origin = -> Origin011
  Reference_AP = Tube carré 25 x 2
  longueur = 258.5
FEATURE [App::Link] A14002  label="A14003"
  AssemblyType = Asm4EE
  AttachedBy = #B1002
  AttachedTo = A5001#cote2003
  AttachmentOffset = pos=(8.295,0,-11.77) rot=(0.499145,-0.499145,-0.708314;1.90902rad)
  LinkPlacement = pos=(996.705,-222.5,-284.23) rot=(-0.170689,0,-0.985325;3.14159rad)
  LinkedObject = -> Part004
  Placement = pos=(996.705,-222.5,-284.23) rot=(-0.170689,0,-0.985325;3.14159rad)
  expr: .AttachmentOffset.Rotation.Roll = Sketch014.Constraints.anglerou
  expr: Placement = A5001.Placement * cote2003.Placement * AttachmentOffset * B1002.Placement ^ -1
FEATURE [App::Link] A14003  label="A14004"
  AssemblyType = Asm4EE
  AttachedBy = #B1002
  AttachedTo = A5002#cote2003
  AttachmentOffset = pos=(0,8.29,-11.77) rot=(1,0,0;1.22774rad)
  LinkPlacement = pos=(1013.29,222.5,-284.23) rot=(0,-1,0;0.343057rad)
  LinkedObject = -> Part004
  Placement = pos=(1013.29,222.5,-284.23) rot=(0,-1,0;0.343057rad)
  expr: .AttachmentOffset.Rotation.Roll = Sketch014.Constraints.anglerou
  expr: Placement = A5002.Placement * cote2003.Placement * AttachmentOffset * B1002.Placement ^ -1
FEATURE [App::Link] A14004  label="A14005"
  AssemblyType = Asm4EE
  AttachedBy = #B2002
  AttachedTo = A5002#cote2003
  AttachmentOffset = pos=(0,-8.3,-11.77) rot=(0,0.576035,0.817425;3.14159rad)
  LinkPlacement = pos=(268.897,222.5,-24.2733) rot=(-0.985325,0,0.170689;3.14159rad)
  LinkedObject = -> Part004
  Placement = pos=(268.897,222.5,-24.2733) rot=(-0.985325,0,0.170689;3.14159rad)
  expr: .AttachmentOffset.Rotation.Roll = Sketch014.Constraints.anglerou
  expr: Placement = A5002.Placement * cote2003.Placement * AttachmentOffset * B2002.Placement ^ -1
FEATURE [PartDesign::CoordinateSystem] dessus
  AttacherType = Attacher::AttachEngine3D
  AttachmentOffset = pos=(0,-11,0) rot=(0,0,1;0rad)
  AttachmentSupport = -> [Pad009]
  MapMode = 45
  Placement = pos=(-3e-16,-34,1.01e-14) rot=(0,1,0;3.14159rad)
FEATURE [PartDesign::CoordinateSystem] dessous
  AttacherType = Attacher::AttachEngine3D
  AttachmentSupport = -> [Pad009]
  MapMode = 5
  Placement = pos=(0,1.8e-15,4) rot=(0,0,1;3.14159rad)
FEATURE [App::Part] Part001  label="A11"
  Group = -> [Body007,dessus,dessous]
  Nom_de_la_piece = 'A11
  Origin = -> Origin023
  Reference_AP = fer U 30 x 15 x 4
  longueur = 46
FEATURE [PartDesign::CoordinateSystem] axe
  AttacherType = Attacher::AttachEngine3D
  AttachmentOffset = pos=(0,-12.5,0) rot=(0,0,1;0rad)
  AttachmentSupport = -> [Pad008]
  MapMode = 5
  Placement = pos=(0,-2.8e-15,12.5) rot=(0,0.707107,-0.707107;3.14159rad)
FEATURE [App::Link] A11  label="A14006"
  AssemblyType = Asm4EE
  AttachedBy = #dessus
  AttachedTo = A5002#cote2003
  AttachmentOffset = pos=(0,0,0) rot=(0.707107,-0.707107,0;3.14159rad)
  LinkPlacement = pos=(1005,188.5,-296) rot=(1,0,0;3.14159rad)
  LinkedObject = -> Part001
  Placement = pos=(1005,188.5,-296) rot=(1,0,0;3.14159rad)
  expr: Placement = A5002.Placement * cote2003.Placement * AttachmentOffset * dessus.Placement ^ -1
FEATURE [App::Link] A11001
  AssemblyType = Asm4EE
  AttachedBy = #dessus
  AttachedTo = A5001#cote2003
  AttachmentOffset = pos=(0,0,0) rot=(0,-1,0;3.14159rad)
  LinkPlacement = pos=(1005,-188.5,-296) rot=(0,-1,0;3.14159rad)
  LinkedObject = -> Part001
  Placement = pos=(1005,-188.5,-296) rot=(0,-1,0;3.14159rad)
  expr: Placement = A5001.Placement * cote2003.Placement * AttachmentOffset * dessus.Placement ^ -1
FEATURE [App::Link] A10  label="A14007"
  AssemblyType = Asm4EE
  AttachedBy = #axe
  AttachedTo = A11001#dessous
  AttachmentOffset = pos=(0,5,0) rot=(0,0.707107,0.707107;3.14159rad)
  LinkPlacement = pos=(1005,-193.5,-312.5) rot=(0,0,1;0rad)
  LinkedObject = -> Part
  Placement = pos=(1005,-193.5,-312.5) rot=(0,0,1;0rad)
  expr: Placement = A11001.Placement * dessous.Placement * AttachmentOffset * axe.Placement ^ -1
FEATURE [App::Link] A10006
  AssemblyType = Asm4EE
  AttachedBy = #axe
  AttachedTo = A11#dessous
  AttachmentOffset = pos=(0,5,0) rot=(0,0.707107,0.707107;3.14159rad)
  LinkPlacement = pos=(1005,193.5,-312.5) rot=(0,0,1;3.14159rad)
  LinkedObject = -> Part
  Placement = pos=(1005,193.5,-312.5) rot=(0,0,1;3.14159rad)
  expr: Placement = A11.Placement * dessous.Placement * AttachmentOffset * axe.Placement ^ -1
FEATURE [App::Link] Roue_increvable___389___axe25_L_82001
  AssemblyType = Asm4EE
  AttachedBy = #LCS_0004
  AttachedTo = A10006#axe
  AttachmentOffset = pos=(0,0,-6) rot=(0,1,0;1.5708rad)
  LinkPlacement = pos=(1005,287.5,-312.5) rot=(-0.57735,0.57735,-0.57735;2.0944rad)
  LinkedObject = -> Roue_increvable___389___axe25_L_82
  Placement = pos=(1005,287.5,-312.5) rot=(-0.57735,0.57735,-0.57735;2.0944rad)
  expr: Placement = A10006.Placement * axe.Placement * AttachmentOffset * LCS_0004.Placement ^ -1
FEATURE [App::Link] Roue_increvable___389___axe25_L_82002
  AssemblyType = Asm4EE
  AttachedBy = #LCS_0004
  AttachedTo = A10#axe
  AttachmentOffset = pos=(0,0,-6) rot=(0,-1,0;4.71239rad)
  LinkPlacement = pos=(1005,-287.5,-312.5) rot=(-0.57735,-0.57735,0.57735;2.0944rad)
  LinkedObject = -> Roue_increvable___389___axe25_L_82
  Placement = pos=(1005,-287.5,-312.5) rot=(-0.57735,-0.57735,0.57735;2.0944rad)
  expr: Placement = A10.Placement * axe.Placement * AttachmentOffset * LCS_0004.Placement ^ -1
FEATURE [Sketcher::SketchObject] Sketch018
  ArcFitTolerance = 0
  FullyConstrained = true
  MakeInternals = false
  MapMode = 5
  Placement = pos=(0,0,0) rot=(0.57735,0.57735,0.57735;2.0944rad)
  expr: Constraints[15] = .Constraints.hauteur * 0.1
  expr: Constraints[27] = .Constraints.epaisseur
  sketch-geometry (12):
    g0: LineSegment StartX=-10 StartY=12.5 StartZ=0 EndX=10 EndY=12.5 EndZ=0
    g1: LineSegment StartX=12.5 StartY=10 StartZ=0 EndX=12.5 EndY=-10 EndZ=0
    g2: LineSegment StartX=10 StartY=-12.5 StartZ=0 EndX=-10 EndY=-12.5 EndZ=0
    g3: LineSegment StartX=-12.5 StartY=-10 StartZ=0 EndX=-12.5 EndY=10 EndZ=0
    g4: ArcOfCircle CenterX=-10 CenterY=10 CenterZ=0 NormalX=0 NormalY=0 NormalZ=1 AngleXU=0 Radius=2.5 StartAngle=1.5708 EndAngle=3.14159
    g5: ArcOfCircle CenterX=10 CenterY=10 CenterZ=0 NormalX=0 NormalY=0 NormalZ=1 AngleXU=0 Radius=2.5 StartAngle=2e-16 EndAngle=1.5708
    g6: ArcOfCircle CenterX=10 CenterY=-10 CenterZ=0 NormalX=0 NormalY=0 NormalZ=1 AngleXU=0 Radius=2.5 StartAngle=4.71239 EndAngle=6.28319
    g7: ArcOfCircle CenterX=-10 CenterY=-10 CenterZ=0 NormalX=0 NormalY=0 NormalZ=1 AngleXU=0 Radius=2.5 StartAngle=3.14159 EndAngle=4.71239
    g8: LineSegment StartX=-10.5 StartY=10.5 StartZ=0 EndX=10.5 EndY=10.5 EndZ=0
    g9: LineSegment StartX=10.5 StartY=10.5 StartZ=0 EndX=10.5 EndY=-10.5 EndZ=0
    g10: LineSegment StartX=10.5 StartY=-10.5 StartZ=0 EndX=-10.5 EndY=-10.5 EndZ=0
    g11: LineSegment StartX=-10.5 StartY=-10.5 StartZ=0 EndX=-10.5 EndY=10.5 EndZ=0
  constraints (28):
    c: Horizontal(g2)
    c: Vertical(g3)
    c: Tangent(g0,g4) = 1.5708
    c: Tangent(g3,g4) = 1.5708
    c: Tangent(g0,g5) = 1.5708
    c: Tangent(g1,g5) = 1.5708
    c: Tangent(g1,g6) = 1.5708
    c: Tangent(g2,g6) = 1.5708
    c: Tangent(g2,g7) = 1.5708
    c: Tangent(g3,g7) = 1.5708
    c: Equal(g4,g5)
    c: DistanceY(g2,g0) = 25  'hauteur'
    c: DistanceX(g3,g1) = 25  'largeur'
    c: Equal(g5,g6)
    c: Equal(g6,g7)
    c: Radius(g7) = 2.5
    c: Symmetric(g1,g1,g-1)
    c: Symmetric(g0,g0,g-2)
    c: Coincident(g8,g9)
    c: Coincident(g9,g10)
    c: Coincident(g10,g11)
    c: Coincident(g11,g8)
    c: Horizontal(g10)
    c: Vertical(g11)
    c: Symmetric(g8,g9,g-1)
    c: Symmetric(g8,g8,g-2)
    c: DistanceX(g3,g8) = 2  'epaisseur'
    c: DistanceY(g2,g9) = 2
FEATURE [PartDesign::Pad] Pad013
  Direction = (1,1e-16,-1e-16)
  Length = 462
  Length2 = 100
  Placement = pos=(0,0,0) rot=(0.57735,0.57735,0.57735;2.0944rad)
  Profile = -> Sketch018
  Suppressed = false
  Type = 0
  expr: Length = Sketch014.Constraints.l2pied
FEATURE [PartDesign::CoordinateSystem] cote1  label="cote2004"
  AttacherType = Attacher::AttachEngine3D
  AttachmentSupport = -> [Pad013]
  MapMode = 5
  Placement = pos=(0,0,0) rot=(0.57735,0.57735,-0.57735;4.18879rad)
FEATURE [App::Link] A15  label="A14008"
  AssemblyType = Asm4EE
  AttachedBy = #cote1
  AttachedTo = A12001#B2
  AttachmentOffset = pos=(1.67796,0,-6.25567) rot=(0,-1,0;0.524048rad)
  LinkPlacement = pos=(12.5,290.822,-406.244) rot=(-0.694725,0.186318,-0.694725;2.77318rad)
  LinkedObject = -> Part005
  Placement = pos=(12.5,290.822,-406.244) rot=(-0.694725,0.186318,-0.694725;2.77318rad)
  expr: .AttachmentOffset.Rotation.Pitch = -Sketch014.Constraints.angle2
  expr: Placement = A12001.Placement * B2.Placement * AttachmentOffset * cote1.Placement ^ -1
FEATURE [App::Link] A14008  label="A14009"
  AssemblyType = Asm4EE
  AttachedBy = #cote1
  AttachedTo = A12#B2
  AttachmentOffset = pos=(-1.68,0,-6.25) rot=(0.259036,0,0.965868;3.14159rad)
  LinkPlacement = pos=(12.5,-290.82,-406.25) rot=(-0.250759,-0.935008,0.250759;1.63795rad)
  LinkedObject = -> Part005
  Placement = pos=(12.5,-290.82,-406.25) rot=(-0.250759,-0.935008,0.250759;1.63795rad)
  expr: .AttachmentOffset.Rotation.Pitch = -Sketch014.Constraints.angle2
  expr: Placement = A12.Placement * B2.Placement * AttachmentOffset * cote1.Placement ^ -1
FEATURE [App::Link] A15001
  AssemblyType = Asm4EE
  AttachedBy = #cote1
  AttachedTo = A12002#B2
  AttachmentOffset = pos=(0,1.68,-6.25) rot=(0.250759,-0.250759,0.935008;1.63795rad)
  LinkPlacement = pos=(1997.5,-290.82,-406.25) rot=(0.250759,0.935008,-0.250759;4.64524rad)
  LinkedObject = -> Part005
  Placement = pos=(1997.5,-290.82,-406.25) rot=(0.250759,0.935008,-0.250759;4.64524rad)
  expr: .AttachmentOffset.Rotation.Pitch = -Sketch014.Constraints.angle2
  expr: Placement = A12002.Placement * B2.Placement * AttachmentOffset * cote1.Placement ^ -1
FEATURE [App::Link] A15002
  AssemblyType = Asm4EE
  AttachedBy = #cote1
  AttachedTo = A12003#B2
  AttachmentOffset = pos=(0,-1.68,-6.25) rot=(-0.250759,-0.250759,-0.935008;1.63795rad)
  LinkPlacement = pos=(1997.5,290.82,-406.25) rot=(-0.694725,0.186318,-0.694725;2.77318rad)
  LinkedObject = -> Part005
  Placement = pos=(1997.5,290.82,-406.25) rot=(-0.694725,0.186318,-0.694725;2.77318rad)
  expr: .AttachmentOffset.Rotation.Pitch = -Sketch014.Constraints.angle2
  expr: Placement = A12003.Placement * B2.Placement * AttachmentOffset * cote1.Placement ^ -1
FEATURE [Sketcher::SketchObject] Sketch019
  ArcFitTolerance = 0
  FullyConstrained = true
  MakeInternals = false
  MapMode = 5
  Placement = pos=(0,0,0) rot=(0.57735,0.57735,0.57735;2.0944rad)
  expr: Constraints[15] = .Constraints.hauteur * 0.1
  expr: Constraints[27] = .Constraints.epaisseur
  sketch-geometry (12):
    g0: LineSegment StartX=-10 StartY=12.5 StartZ=0 EndX=10 EndY=12.5 EndZ=0
    g1: LineSegment StartX=12.5 StartY=10 StartZ=0 EndX=12.5 EndY=-10 EndZ=0
    g2: LineSegment StartX=10 StartY=-12.5 StartZ=0 EndX=-10 EndY=-12.5 EndZ=0
    g3: LineSegment StartX=-12.5 StartY=-10 StartZ=0 EndX=-12.5 EndY=10 EndZ=0
    g4: ArcOfCircle CenterX=-10 CenterY=10 CenterZ=0 NormalX=0 NormalY=0 NormalZ=1 AngleXU=0 Radius=2.5 StartAngle=1.5708 EndAngle=3.14159
    g5: ArcOfCircle CenterX=10 CenterY=10 CenterZ=0 NormalX=0 NormalY=0 NormalZ=1 AngleXU=0 Radius=2.5 StartAngle=2e-16 EndAngle=1.5708
    g6: ArcOfCircle CenterX=10 CenterY=-10 CenterZ=0 NormalX=0 NormalY=0 NormalZ=1 AngleXU=0 Radius=2.5 StartAngle=4.71239 EndAngle=6.28319
    g7: ArcOfCircle CenterX=-10 CenterY=-10 CenterZ=0 NormalX=0 NormalY=0 NormalZ=1 AngleXU=0 Radius=2.5 StartAngle=3.14159 EndAngle=4.71239
    g8: LineSegment StartX=-10.5 StartY=10.5 StartZ=0 EndX=10.5 EndY=10.5 EndZ=0
    g9: LineSegment StartX=10.5 StartY=10.5 StartZ=0 EndX=10.5 EndY=-10.5 EndZ=0
    g10: LineSegment StartX=10.5 StartY=-10.5 StartZ=0 EndX=-10.5 EndY=-10.5 EndZ=0
    g11: LineSegment StartX=-10.5 StartY=-10.5 StartZ=0 EndX=-10.5 EndY=10.5 EndZ=0
  constraints (28):
    c: Horizontal(g2)
    c: Vertical(g3)
    c: Tangent(g0,g4) = 1.5708
    c: Tangent(g3,g4) = 1.5708
    c: Tangent(g0,g5) = 1.5708
    c: Tangent(g1,g5) = 1.5708
    c: Tangent(g1,g6) = 1.5708
    c: Tangent(g2,g6) = 1.5708
    c: Tangent(g2,g7) = 1.5708
    c: Tangent(g3,g7) = 1.5708
    c: Equal(g4,g5)
    c: DistanceY(g2,g0) = 25  'hauteur'
    c: DistanceX(g3,g1) = 25  'largeur'
    c: Equal(g5,g6)
    c: Equal(g6,g7)
    c: Radius(g7) = 2.5
    c: Symmetric(g1,g1,g-1)
    c: Symmetric(g0,g0,g-2)
    c: Coincident(g8,g9)
    c: Coincident(g9,g10)
    c: Coincident(g10,g11)
    c: Coincident(g11,g8)
    c: Horizontal(g10)
    c: Vertical(g11)
    c: Symmetric(g8,g9,g-1)
    c: Symmetric(g8,g8,g-2)
    c: DistanceX(g3,g8) = 2  'epaisseur'
    c: DistanceY(g2,g9) = 2
FEATURE [PartDesign::Pad] Pad014
  Direction = (1,1e-16,-1e-16)
  Length = 685
  Length2 = 100
  Placement = pos=(0,0,0) rot=(0.57735,0.57735,0.57735;2.0944rad)
  Profile = -> Sketch019
  Suppressed = false
  Type = 0
  expr: Length = Spreadsheet.B12 + Spreadsheet.B2 * 3
FEATURE [PartDesign::Body] Body012
  AllowCompound = false
  Group = -> [Sketch019,Pad014]
  Origin = -> Origin034
  Tip = -> Pad014
FEATURE [Sketcher::SketchObject] Sketch020
  ArcFitTolerance = 0
  FullyConstrained = true
  MakeInternals = false
  MapMode = 5
  Placement = pos=(0,0,0) rot=(0.57735,0.57735,0.57735;2.0944rad)
  expr: Constraints[15] = .Constraints.hauteur * 0.1
  expr: Constraints[27] = .Constraints.epaisseur
  sketch-geometry (12):
    g0: LineSegment StartX=-10 StartY=12.5 StartZ=0 EndX=10 EndY=12.5 EndZ=0
    g1: LineSegment StartX=12.5 StartY=10 StartZ=0 EndX=12.5 EndY=-10 EndZ=0
    g2: LineSegment StartX=10 StartY=-12.5 StartZ=0 EndX=-10 EndY=-12.5 EndZ=0
    g3: LineSegment StartX=-12.5 StartY=-10 StartZ=0 EndX=-12.5 EndY=10 EndZ=0
    g4: ArcOfCircle CenterX=-10 CenterY=10 CenterZ=0 NormalX=0 NormalY=0 NormalZ=1 AngleXU=0 Radius=2.5 StartAngle=1.5708 EndAngle=3.14159
    g5: ArcOfCircle CenterX=10 CenterY=10 CenterZ=0 NormalX=0 NormalY=0 NormalZ=1 AngleXU=0 Radius=2.5 StartAngle=2e-16 EndAngle=1.5708
    g6: ArcOfCircle CenterX=10 CenterY=-10 CenterZ=0 NormalX=0 NormalY=0 NormalZ=1 AngleXU=0 Radius=2.5 StartAngle=4.71239 EndAngle=6.28319
    g7: ArcOfCircle CenterX=-10 CenterY=-10 CenterZ=0 NormalX=0 NormalY=0 NormalZ=1 AngleXU=0 Radius=2.5 StartAngle=3.14159 EndAngle=4.71239
    g8: LineSegment StartX=-10.5 StartY=10.5 StartZ=0 EndX=10.5 EndY=10.5 EndZ=0
    g9: LineSegment StartX=10.5 StartY=10.5 StartZ=0 EndX=10.5 EndY=-10.5 EndZ=0
    g10: LineSegment StartX=10.5 StartY=-10.5 StartZ=0 EndX=-10.5 EndY=-10.5 EndZ=0
    g11: LineSegment StartX=-10.5 StartY=-10.5 StartZ=0 EndX=-10.5 EndY=10.5 EndZ=0
  constraints (28):
    c: Horizontal(g2)
    c: Vertical(g3)
    c: Tangent(g0,g4) = 1.5708
    c: Tangent(g3,g4) = 1.5708
    c: Tangent(g0,g5) = 1.5708
    c: Tangent(g1,g5) = 1.5708
    c: Tangent(g1,g6) = 1.5708
    c: Tangent(g2,g6) = 1.5708
    c: Tangent(g2,g7) = 1.5708
    c: Tangent(g3,g7) = 1.5708
    c: Equal(g4,g5)
    c: DistanceY(g2,g0) = 25  'hauteur'
    c: DistanceX(g3,g1) = 25  'largeur'
    c: Equal(g5,g6)
    c: Equal(g6,g7)
    c: Radius(g7) = 2.5
    c: Symmetric(g1,g1,g-1)
    c: Symmetric(g0,g0,g-2)
    c: Coincident(g8,g9)
    c: Coincident(g9,g10)
    c: Coincident(g10,g11)
    c: Coincident(g11,g8)
    c: Horizontal(g10)
    c: Vertical(g11)
    c: Symmetric(g8,g9,g-1)
    c: Symmetric(g8,g8,g-2)
    c: DistanceX(g3,g8) = 2  'epaisseur'
    c: DistanceY(g2,g9) = 2
FEATURE [PartDesign::Pad] Pad015
  Direction = (1,1e-16,-1e-16)
  Length = 560
  Length2 = 100
  Placement = pos=(0,0,0) rot=(0.57735,0.57735,0.57735;2.0944rad)
  Profile = -> Sketch020
  Suppressed = false
  Type = 0
  expr: Length = Spreadsheet.B12 - Spreadsheet.B2 * 2
FEATURE [PartDesign::Body] Body013
  AllowCompound = false
  Group = -> [Sketch020,Pad015]
  Origin = -> Origin036
  Tip = -> Pad015
FEATURE [Sketcher::SketchObject] Sketch021
  ArcFitTolerance = 0
  FullyConstrained = true
  MakeInternals = false
  MapMode = 5
  Placement = pos=(0,0,0) rot=(0.57735,0.57735,0.57735;2.0944rad)
  expr: Constraints[15] = .Constraints.hauteur * 0.1
  expr: Constraints[27] = .Constraints.epaisseur
  sketch-geometry (12):
    g0: LineSegment StartX=-10 StartY=12.5 StartZ=0 EndX=10 EndY=12.5 EndZ=0
    g1: LineSegment StartX=12.5 StartY=10 StartZ=0 EndX=12.5 EndY=-10 EndZ=0
    g2: LineSegment StartX=10 StartY=-12.5 StartZ=0 EndX=-10 EndY=-12.5 EndZ=0
    g3: LineSegment StartX=-12.5 StartY=-10 StartZ=0 EndX=-12.5 EndY=10 EndZ=0
    g4: ArcOfCircle CenterX=-10 CenterY=10 CenterZ=0 NormalX=0 NormalY=0 NormalZ=1 AngleXU=0 Radius=2.5 StartAngle=1.5708 EndAngle=3.14159
    g5: ArcOfCircle CenterX=10 CenterY=10 CenterZ=0 NormalX=0 NormalY=0 NormalZ=1 AngleXU=0 Radius=2.5 StartAngle=2e-16 EndAngle=1.5708
    g6: ArcOfCircle CenterX=10 CenterY=-10 CenterZ=0 NormalX=0 NormalY=0 NormalZ=1 AngleXU=0 Radius=2.5 StartAngle=4.71239 EndAngle=6.28319
    g7: ArcOfCircle CenterX=-10 CenterY=-10 CenterZ=0 NormalX=0 NormalY=0 NormalZ=1 AngleXU=0 Radius=2.5 StartAngle=3.14159 EndAngle=4.71239
    g8: LineSegment StartX=-10.5 StartY=10.5 StartZ=0 EndX=10.5 EndY=10.5 EndZ=0
    g9: LineSegment StartX=10.5 StartY=10.5 StartZ=0 EndX=10.5 EndY=-10.5 EndZ=0
    g10: LineSegment StartX=10.5 StartY=-10.5 StartZ=0 EndX=-10.5 EndY=-10.5 EndZ=0
    g11: LineSegment StartX=-10.5 StartY=-10.5 StartZ=0 EndX=-10.5 EndY=10.5 EndZ=0
  constraints (28):
    c: Horizontal(g2)
    c: Vertical(g3)
    c: Tangent(g0,g4) = 1.5708
    c: Tangent(g3,g4) = 1.5708
    c: Tangent(g0,g5) = 1.5708
    c: Tangent(g1,g5) = 1.5708
    c: Tangent(g1,g6) = 1.5708
    c: Tangent(g2,g6) = 1.5708
    c: Tangent(g2,g7) = 1.5708
    c: Tangent(g3,g7) = 1.5708
    c: Equal(g4,g5)
    c: DistanceY(g2,g0) = 25  'hauteur'
    c: DistanceX(g3,g1) = 25  'largeur'
    c: Equal(g5,g6)
    c: Equal(g6,g7)
    c: Radius(g7) = 2.5
    c: Symmetric(g1,g1,g-1)
    c: Symmetric(g0,g0,g-2)
    c: Coincident(g8,g9)
    c: Coincident(g9,g10)
    c: Coincident(g10,g11)
    c: Coincident(g11,g8)
    c: Horizontal(g10)
    c: Vertical(g11)
    c: Symmetric(g8,g9,g-1)
    c: Symmetric(g8,g8,g-2)
    c: DistanceX(g3,g8) = 2  'epaisseur'
    c: DistanceY(g2,g9) = 2
FEATURE [PartDesign::Pad] Pad016
  Direction = (1,1e-16,-1e-16)
  Length = 610
  Length2 = 100
  Placement = pos=(0,0,0) rot=(0.57735,0.57735,0.57735;2.0944rad)
  Profile = -> Sketch021
  Suppressed = false
  Type = 0
  expr: Length = Spreadsheet.D4
FEATURE [PartDesign::Body] Body014
  AllowCompound = false
  Group = -> [Sketch021,Pad016]
  Origin = -> Origin038
  Tip = -> Pad016
FEATURE [Sketcher::SketchObject] Sketch022
  ArcFitTolerance = 0
  FullyConstrained = true
  MakeInternals = false
  MapMode = 5
  Placement = pos=(0,0,0) rot=(0.57735,0.57735,0.57735;2.0944rad)
  expr: Constraints[15] = .Constraints.hauteur * 0.1
  expr: Constraints[27] = .Constraints.epaisseur
  sketch-geometry (12):
    g0: LineSegment StartX=-12 StartY=15 StartZ=0 EndX=12 EndY=15 EndZ=0
    g1: LineSegment StartX=15 StartY=12 StartZ=0 EndX=15 EndY=-12 EndZ=0
    g2: LineSegment StartX=12 StartY=-15 StartZ=0 EndX=-12 EndY=-15 EndZ=0
    g3: LineSegment StartX=-15 StartY=-12 StartZ=0 EndX=-15 EndY=12 EndZ=0
    g4: ArcOfCircle CenterX=-12 CenterY=12 CenterZ=0 NormalX=0 NormalY=0 NormalZ=1 AngleXU=0 Radius=3 StartAngle=1.5708 EndAngle=3.14159
    g5: ArcOfCircle CenterX=12 CenterY=12 CenterZ=0 NormalX=0 NormalY=0 NormalZ=1 AngleXU=0 Radius=3 StartAngle=1e-16 EndAngle=1.5708
    g6: ArcOfCircle CenterX=12 CenterY=-12 CenterZ=0 NormalX=0 NormalY=0 NormalZ=1 AngleXU=0 Radius=3 StartAngle=4.71239 EndAngle=6.28319
    g7: ArcOfCircle CenterX=-12 CenterY=-12 CenterZ=0 NormalX=0 NormalY=0 NormalZ=1 AngleXU=0 Radius=3 StartAngle=3.14159 EndAngle=4.71239
    g8: LineSegment StartX=-13 StartY=13 StartZ=0 EndX=13 EndY=13 EndZ=0
    g9: LineSegment StartX=13 StartY=13 StartZ=0 EndX=13 EndY=-13 EndZ=0
    g10: LineSegment StartX=13 StartY=-13 StartZ=0 EndX=-13 EndY=-13 EndZ=0
    g11: LineSegment StartX=-13 StartY=-13 StartZ=0 EndX=-13 EndY=13 EndZ=0
  constraints (28):
    c: Horizontal(g2)
    c: Vertical(g3)
    c: Tangent(g0,g4) = 1.5708
    c: Tangent(g3,g4) = 1.5708
    c: Tangent(g0,g5) = 1.5708
    c: Tangent(g1,g5) = 1.5708
    c: Tangent(g1,g6) = 1.5708
    c: Tangent(g2,g6) = 1.5708
    c: Tangent(g2,g7) = 1.5708
    c: Tangent(g3,g7) = 1.5708
    c: Equal(g4,g5)
    c: DistanceY(g2,g0) = 30  'hauteur'
    c: DistanceX(g3,g1) = 30  'largeur'
    c: Equal(g5,g6)
    c: Equal(g6,g7)
    c: Radius(g7) = 3
    c: Symmetric(g1,g1,g-1)
    c: Symmetric(g0,g0,g-2)
    c: Coincident(g8,g9)
    c: Coincident(g9,g10)
    c: Coincident(g10,g11)
    c: Coincident(g11,g8)
    c: Horizontal(g10)
    c: Vertical(g11)
    c: Symmetric(g8,g9,g-1)
    c: Symmetric(g8,g8,g-2)
    c: DistanceX(g3,g8) = 2  'epaisseur'
    c: DistanceY(g2,g9) = 2
FEATURE [PartDesign::Pad] Pad017
  Direction = (1,1e-16,-1e-16)
  Length = 50
  Length2 = 100
  Placement = pos=(0,0,0) rot=(0.57735,0.57735,0.57735;2.0944rad)
  Profile = -> Sketch022
  Suppressed = false
  Type = 0
  expr: Length = 2 * Spreadsheet.B2
FEATURE [PartDesign::Body] Body015
  AllowCompound = false
  Group = -> [Sketch022,Pad017]
  Origin = -> Origin040
  Tip = -> Pad017
FEATURE [PartDesign::CoordinateSystem] face1
  AttacherType = Attacher::AttachEngine3D
  AttachmentSupport = -> [Pad017]
  MapMode = 5
  Placement = pos=(-1.7e-15,15,-9e-16) rot=(0.57735,0.57735,0.57735;4.18879rad)
FEATURE [PartDesign::CoordinateSystem] cote2004  label="cote2005"
  AttacherType = Attacher::AttachEngine3D
  AttachmentSupport = -> [Pad015]
  MapMode = 5
  Placement = pos=(560,2.464e-13,0) rot=(0.57735,0.57735,0.57735;2.0944rad)
FEATURE [PartDesign::CoordinateSystem] cote1001
  AttacherType = Attacher::AttachEngine3D
  AttachmentSupport = -> [Pad015]
  MapMode = 5
  Placement = pos=(0,0,0) rot=(0.57735,0.57735,-0.57735;4.18879rad)
FEATURE [App::Part] Part007  label="BB2"
  Group = -> [Body013,cote2004,cote1001]
  Nom_de_la_piece = 'BB2
  Origin = -> Origin035
  Reference_AP = Tube carré 25 x 2
  longueur = 560
FEATURE [PartDesign::CoordinateSystem] cote1002
  AttacherType = Attacher::AttachEngine3D
  AttachmentSupport = -> [Pad014]
  MapMode = 5
  Placement = pos=(0,0,0) rot=(0.57735,0.57735,-0.57735;4.18879rad)
FEATURE [PartDesign::CoordinateSystem] cote2005  label="cote2006"
  AttacherType = Attacher::AttachEngine3D
  AttachmentSupport = -> [Pad014]
  MapMode = 5
  Placement = pos=(685,3.014e-13,0) rot=(0.57735,0.57735,0.57735;2.0944rad)
FEATURE [App::Part] Part006  label="BB1"
  Group = -> [Body012,cote1002,cote2005]
  Nom_de_la_piece = 'BB1
  Origin = -> Origin033
  Reference_AP = Tube carré 25 x 2
  longueur = 685
FEATURE [PartDesign::CoordinateSystem] cote1003
  AttacherType = Attacher::AttachEngine3D
  AttachmentSupport = -> [Pad016]
  MapMode = 5
  Placement = pos=(610,2.684e-13,0) rot=(0.57735,0.57735,0.57735;2.0944rad)
FEATURE [PartDesign::CoordinateSystem] cote2006  label="cote2007"
  AttacherType = Attacher::AttachEngine3D
  AttachmentSupport = -> [Pad016]
  MapMode = 5
  Placement = pos=(0,0,0) rot=(0.57735,0.57735,-0.57735;4.18879rad)
FEATURE [App::Part] Part008  label="BB3"
  Group = -> [Body014,cote1003,cote2006]
  Nom_de_la_piece = 'BB3
  Origin = -> Origin037
  Reference_AP = Tube carré 25 x 2
  longueur = 610
FEATURE [PartDesign::CoordinateSystem] centre
  AttacherType = Attacher::AttachEngine3D
  AttachmentSupport = -> [Pad017]
  MapMode = 5
  Placement = pos=(0,0,0) rot=(0.57735,0.57735,-0.57735;4.18879rad)
FEATURE [App::Part] Part009  label="A16"
  Group = -> [Body015,face1,centre]
  Nom_de_la_piece = 'A16
  Origin = -> Origin039
  Reference_AP = Tube carré 30 x 2
  longueur = 50
FEATURE [App::Link] A16  label="A15003"
  AssemblyType = Asm4EE
  AttachedBy = #face1
  AttachedTo = A2001#cote2A2
  AttachmentOffset = pos=(-12.5,-12.5,-12.5) rot=(0,1,0;1.5708rad)
  LinkPlacement = pos=(-15,292.5,12.5) rot=(0.57735,0.57735,-0.57735;2.0944rad)
  LinkedObject = -> Part009
  Placement = pos=(-15,292.5,12.5) rot=(0.57735,0.57735,-0.57735;2.0944rad)
  expr: .AttachmentOffset.Base.x = -Spreadsheet.B2 / 2
  expr: .AttachmentOffset.Base.y = -Spreadsheet.B2 / 2
  expr: .AttachmentOffset.Base.z = -Spreadsheet.B2 / 2
  expr: Placement = A2001.Placement * cote2A2.Placement * AttachmentOffset * face1.Placement ^ -1
FEATURE [App::Link] A16001
  AssemblyType = Asm4EE
  AttachedBy = #face1
  AttachedTo = A2001#LCS_0001
  AttachmentOffset = pos=(12.5,-12.5,-12.5) rot=(0,-0.707107,-0.707107;3.14159rad)
  LinkPlacement = pos=(-15,-292.5,12.5) rot=(-0.57735,-0.57735,0.57735;4.18879rad)
  LinkedObject = -> Part009
  Placement = pos=(-15,-292.5,12.5) rot=(-0.57735,-0.57735,0.57735;4.18879rad)
  expr: .AttachmentOffset.Base.x = Spreadsheet.B2 / 2
  expr: .AttachmentOffset.Base.y = -Spreadsheet.B2 / 2
  expr: .AttachmentOffset.Base.z = -Spreadsheet.B2 / 2
  expr: Placement = A2001.Placement * LCS_0001.Placement * AttachmentOffset * face1.Placement ^ -1
FEATURE [App::Link] BB1  label="BB004"
  AssemblyType = Asm4EE
  AttachedBy = #cote1002
  AttachedTo = A16001#centre
  AttachmentOffset = pos=(0,0,-75) rot=(0,1,0;3.14159rad)
  LinkPlacement = pos=(-15,-292.5,-62.5) rot=(-0.57735,0.57735,-0.57735;4.18879rad)
  LinkedObject = -> Part006
  Placement = pos=(-15,-292.5,-62.5) rot=(-0.57735,0.57735,-0.57735;4.18879rad)
  expr: .AttachmentOffset.Base.z = -Spreadsheet.B2 * 3
  expr: Placement = A16001.Placement * centre.Placement * AttachmentOffset * cote1002.Placement ^ -1
FEATURE [App::Link] BB1001
  AssemblyType = Asm4EE
  AttachedBy = #cote1002
  AttachedTo = A16#centre
  AttachmentOffset = pos=(0,0,-75) rot=(1,0,0;3.14159rad)
  LinkPlacement = pos=(-15,292.5,-62.5) rot=(-0.57735,-0.57735,-0.57735;2.0944rad)
  LinkedObject = -> Part006
  Placement = pos=(-15,292.5,-62.5) rot=(-0.57735,-0.57735,-0.57735;2.0944rad)
  expr: .AttachmentOffset.Base.z = -Spreadsheet.B2 * 3
  expr: Placement = A16.Placement * centre.Placement * AttachmentOffset * cote1002.Placement ^ -1
FEATURE [App::Link] BB3  label="BB1002"
  AssemblyType = Asm4EE
  AttachedBy = #cote1003
  AttachedTo = BB1001#cote2005
  AttachmentOffset = pos=(0,37.5,-12.5) rot=(-1,0,0;1.5708rad)
  LinkPlacement = pos=(-15,-280,610) rot=(-0.707107,-0.707107,0;3.14159rad)
  LinkedObject = -> Part007
  Placement = pos=(-15,-280,610) rot=(-0.707107,-0.707107,0;3.14159rad)
  expr: .AttachmentOffset.Base.y = Spreadsheet.B2 * 1.5
  expr: .AttachmentOffset.Base.z = -Spreadsheet.B2 / 2
  expr: Placement = BB1001.Placement * cote2005.Placement * AttachmentOffset * cote1003.Placement ^ -1
FEATURE [App::Link] BB2  label="BB1003"
  AssemblyType = Asm4EE
  AttachedBy = #cote1001
  AttachedTo = BB1001#cote1002
  AttachmentOffset = pos=(0,12.5,-87.5) rot=(1,0,0;1.5708rad)
  LinkPlacement = pos=(-15,280,25) rot=(0,0,1;4.71239rad)
  LinkedObject = -> Part007
  Placement = pos=(-15,280,25) rot=(0,0,1;4.71239rad)
  expr: .AttachmentOffset.Base.y = Spreadsheet.B2 / 2
  expr: .AttachmentOffset.Base.z = -Spreadsheet.B2 * 3.5
  expr: Placement = BB1001.Placement * cote1002.Placement * AttachmentOffset * cote1001.Placement ^ -1
FEATURE [App::Link] BB1003  label="BB1004"
  AssemblyType = Asm4EE
  AttachedBy = #cote2004
  AttachedTo = BB3#cote1003
  AttachmentOffset = pos=(0,12.5,-232.5) rot=(1,0,0;1.5708rad)
  LinkPlacement = pos=(-15,97.5,37.5) rot=(-0.57735,-0.57735,-0.57735;2.0944rad)
  LinkedObject = -> Part007
  Placement = pos=(-15,97.5,37.5) rot=(-0.57735,-0.57735,-0.57735;2.0944rad)
  expr: .AttachmentOffset.Base.y = Spreadsheet.B2 / 2
  expr: .AttachmentOffset.Base.z = -(Spreadsheet.D4 - Spreadsheet.B2) / 3 - Spreadsheet.B2 * 1.5
  expr: Placement = BB3.Placement * cote1003.Placement * AttachmentOffset * cote2004.Placement ^ -1
FEATURE [App::Link] BB1004  label="BB1005"
  AssemblyType = Asm4EE
  AttachedBy = #cote1001
  AttachedTo = BB3#cote2006
  AttachmentOffset = pos=(0,-12.5,-182.5) rot=(-1,0,0;1.5708rad)
  LinkPlacement = pos=(-15,-97.5,597.5) rot=(0.57735,0.57735,-0.57735;2.0944rad)
  LinkedObject = -> Part007
  Placement = pos=(-15,-97.5,597.5) rot=(0.57735,0.57735,-0.57735;2.0944rad)
  expr: .AttachmentOffset.Base.y = -Spreadsheet.B2 / 2
  expr: .AttachmentOffset.Base.z = -(Spreadsheet.D4 - Spreadsheet.B2) / 3 + Spreadsheet.B2 / 2
  expr: Placement = BB3.Placement * cote2006.Placement * AttachmentOffset * cote1001.Placement ^ -1
FEATURE [Sketcher::SketchObject] Sketch023
  ArcFitTolerance = 0
  AttachmentSupport = -> [Pad007]
  ExternalGeometry = -> [Pad007]
  FullyConstrained = true
  MakeInternals = false
  MapMode = 5
  Placement = pos=(0,-12.5,0) rot=(1,0,0;1.5708rad)
  expr: Constraints[0] = Spreadsheet.B13
  sketch-geometry (1):
    g0: Circle CenterX=0 CenterY=223.292 CenterZ=0 NormalX=0 NormalY=0 NormalZ=1 AngleXU=0 Radius=15
  constraints (4):
    c: Diameter(g0) = 30
    c: PointOnObject(g0,g-2)
    c: PointOnObject(g-4,g0)
    c: DistanceY(g-4,g0) = 8.29156  'deport'
FEATURE [PartDesign::Pocket] Pocket
  BaseFeature = -> Pad007
  Direction = (0,1,-2e-16)
  Length = 5
  Length2 = 100
  Profile = -> Sketch023
  Suppressed = false
  Type = 1
FEATURE [PartDesign::Body] A8004
  AllowCompound = false
  Group = -> [LCS_0014,Pad007,Sketch011,Sketch023,Pocket]
  Origin = -> Origin020
  Tip = -> Pocket
FEATURE [Sketcher::SketchObject] Sketch024
  ArcFitTolerance = 0
  AttachmentSupport = -> [XZ_Plane042]
  FullyConstrained = true
  MakeInternals = false
  MapMode = 5
  Placement = pos=(0,0,0) rot=(1,0,0;1.5708rad)
  expr: .Constraints.diametre = Spreadsheet.B13
  sketch-geometry (4):
    g0: Circle CenterX=0 CenterY=0 CenterZ=0 NormalX=0 NormalY=0 NormalZ=1 AngleXU=0 Radius=13
    g1: Circle CenterX=0 CenterY=0 CenterZ=0 NormalX=0 NormalY=0 NormalZ=1 AngleXU=0 Radius=15
    g2: GeomPoint [constr] X=-15 Y=0 Z=0
    g3: GeomPoint [constr] X=-13 Y=0 Z=0
  constraints (8):
    c: Coincident(g1,g0)
    c: PointOnObject(g2,g1)
    c: PointOnObject(g3,g0)
    c: Coincident(g0,g-1)
    c: PointOnObject(g3,g-1)
    c: PointOnObject(g2,g-1)
    c: DistanceX(g2,g3) = 2  'epaisseur'
    c: Diameter(g1) = 30  'diametre'
FEATURE [PartDesign::Pad] Pad018
  Direction = (0,-1,2e-16)
  Length = 300
  Length2 = 100
  Placement = pos=(0,0,0) rot=(1,0,0;1.5708rad)
  Profile = -> Sketch024
  Suppressed = false
  Type = 0
FEATURE [PartDesign::Body] Body016
  AllowCompound = false
  Group = -> [Sketch024,Pad018]
  Origin = -> Origin042
  Tip = -> Pad018
FEATURE [PartDesign::CoordinateSystem] centre001
  AttacherType = Attacher::AttachEngine3D
  AttachmentSupport = -> [Pad018]
  MapMode = 5
  Placement = pos=(0,-300,0) rot=(1,0,0;1.5708rad)
FEATURE [App::Part] Part010  label="A17"
  Group = -> [Body016,centre001]
  Nom_de_la_piece = 'A17
  Origin = -> Origin041
  Reference_AP = Tube rond 30 x 2
  longueur = 300
FEATURE [App::Link] A17  label="A16002"
  AssemblyType = Asm4EE
  AttachedBy = #centre001
  AttachedTo = A9#cote2001
  AttachmentOffset = pos=(0,0,0) rot=(1,0,0;4.71239rad)
  LinkPlacement = pos=(2585,-292.5,235.792) rot=(0.707107,0.707107,0;3.14159rad)
  LinkedObject = -> Part010
  Placement = pos=(2585,-292.5,235.792) rot=(0.707107,0.707107,0;3.14159rad)
  expr: Placement = A9.Placement * cote2001.Placement * AttachmentOffset * centre001.Placement ^ -1
FEATURE [App::Link] A17001
  AssemblyType = Asm4EE
  AttachedBy = #centre001
  AttachedTo = A9001#cote2001
  AttachmentOffset = pos=(0,0,0) rot=(1,0,0;4.71239rad)
  LinkPlacement = pos=(2585,292.5,235.792) rot=(0.707107,0.707107,0;3.14159rad)
  LinkedObject = -> Part010
  Placement = pos=(2585,292.5,235.792) rot=(0.707107,0.707107,0;3.14159rad)
  expr: Placement = A9001.Placement * cote2001.Placement * AttachmentOffset * centre001.Placement ^ -1
FEATURE [Sketcher::SketchObject] Sketch025
  ArcFitTolerance = 0
  FullyConstrained = true
  MakeInternals = false
  MapMode = 5
  Placement = pos=(0,0,0) rot=(0.57735,0.57735,0.57735;2.0944rad)
  expr: Constraints[15] = .Constraints.hauteur * 0.1
  expr: Constraints[27] = .Constraints.epaisseur
  sketch-geometry (12):
    g0: LineSegment StartX=-10 StartY=12.5 StartZ=0 EndX=10 EndY=12.5 EndZ=0
    g1: LineSegment StartX=12.5 StartY=10 StartZ=0 EndX=12.5 EndY=-10 EndZ=0
    g2: LineSegment StartX=10 StartY=-12.5 StartZ=0 EndX=-10 EndY=-12.5 EndZ=0
    g3: LineSegment StartX=-12.5 StartY=-10 StartZ=0 EndX=-12.5 EndY=10 EndZ=0
    g4: ArcOfCircle CenterX=-10 CenterY=10 CenterZ=0 NormalX=0 NormalY=0 NormalZ=1 AngleXU=0 Radius=2.5 StartAngle=1.5708 EndAngle=3.14159
    g5: ArcOfCircle CenterX=10 CenterY=10 CenterZ=0 NormalX=0 NormalY=0 NormalZ=1 AngleXU=0 Radius=2.5 StartAngle=2e-16 EndAngle=1.5708
    g6: ArcOfCircle CenterX=10 CenterY=-10 CenterZ=0 NormalX=0 NormalY=0 NormalZ=1 AngleXU=0 Radius=2.5 StartAngle=4.71239 EndAngle=6.28319
    g7: ArcOfCircle CenterX=-10 CenterY=-10 CenterZ=0 NormalX=0 NormalY=0 NormalZ=1 AngleXU=0 Radius=2.5 StartAngle=3.14159 EndAngle=4.71239
    g8: LineSegment StartX=-10.5 StartY=10.5 StartZ=0 EndX=10.5 EndY=10.5 EndZ=0
    g9: LineSegment StartX=10.5 StartY=10.5 StartZ=0 EndX=10.5 EndY=-10.5 EndZ=0
    g10: LineSegment StartX=10.5 StartY=-10.5 StartZ=0 EndX=-10.5 EndY=-10.5 EndZ=0
    g11: LineSegment StartX=-10.5 StartY=-10.5 StartZ=0 EndX=-10.5 EndY=10.5 EndZ=0
  constraints (28):
    c: Horizontal(g2)
    c: Vertical(g3)
    c: Tangent(g0,g4) = 1.5708
    c: Tangent(g3,g4) = 1.5708
    c: Tangent(g0,g5) = 1.5708
    c: Tangent(g1,g5) = 1.5708
    c: Tangent(g1,g6) = 1.5708
    c: Tangent(g2,g6) = 1.5708
    c: Tangent(g2,g7) = 1.5708
    c: Tangent(g3,g7) = 1.5708
    c: Equal(g4,g5)
    c: DistanceY(g2,g0) = 25  'hauteur'
    c: DistanceX(g3,g1) = 25  'largeur'
    c: Equal(g5,g6)
    c: Equal(g6,g7)
    c: Radius(g7) = 2.5
    c: Symmetric(g1,g1,g-1)
    c: Symmetric(g0,g0,g-2)
    c: Coincident(g8,g9)
    c: Coincident(g9,g10)
    c: Coincident(g10,g11)
    c: Coincident(g11,g8)
    c: Horizontal(g10)
    c: Vertical(g11)
    c: Symmetric(g8,g9,g-1)
    c: Symmetric(g8,g8,g-2)
    c: DistanceX(g3,g8) = 2  'epaisseur'
    c: DistanceY(g2,g9) = 2
FEATURE [PartDesign::Pad] Pad019
  Direction = (1,1e-16,-1e-16)
  Length = 142
  Length2 = 100
  Placement = pos=(0,0,0) rot=(0.57735,0.57735,0.57735;2.0944rad)
  Profile = -> Sketch025
  Suppressed = false
  Type = 0
FEATURE [PartDesign::CoordinateSystem] b1
  AttacherType = Attacher::AttachEngine3D
  AttachmentSupport = -> [Pad019]
  MapMode = 5
  Placement = pos=(1.4e-15,-12.5,-2.1e-15) rot=(0.57735,0.57735,-0.57735;2.0944rad)
FEATURE [PartDesign::CoordinateSystem] renf
  AttacherType = Attacher::AttachEngine3D
  AttachmentOffset = pos=(0,100.409,-25) rot=(0,0,1;0rad)
  AttachmentSupport = -> [Pocket]
  MapMode = 5
  Placement = pos=(0,12.5,100.409) rot=(1,0,0;1.5708rad)
  expr: .AttachmentOffset.Base.y = 142 / sqrt(2)
  expr: .AttachmentOffset.Base.z = -Spreadsheet.B2
FEATURE [App::Part] A8003  label="A9"
  Group = -> [LCS_0015,A8004,cote2001,renf]
  Nom_de_la_piece = 'A9
  Origin = -> Origin019
  Reference_AP = Tube carré 25 x 2
  longueur = 215
FEATURE [PartDesign::CoordinateSystem] renf001
  AttacherType = Attacher::AttachEngine3D
  AttachmentOffset = pos=(0,299.591,0) rot=(0,0,1;0rad)
  AttachmentSupport = -> [Pad010]
  MapMode = 5
  Placement = pos=(299.591,-12.5,-2.1e-15) rot=(0.57735,0.57735,-0.57735;2.0944rad)
  expr: .AttachmentOffset.Base.y = Pad010.Length - 142 mm / sqrt(2)
FEATURE [App::Part] Part002  label="A12"
  Group = -> [Body008,Sketch015,Pad010,B1,B2,renf001]
  Nom_de_la_piece = 'A12
  Origin = -> Origin025
  Reference_AP = Tube carré 25 x 2
  longueur = 400
FEATURE [App::Link] A18  label="A17002"
  AssemblyType = Asm4EE
  AttachedBy = #b1
  AttachedTo = A9#renf
  AttachmentOffset = pos=(0,0,0) rot=(-1,0,0;2.35619rad)
  LinkPlacement = pos=(2293.84,-292.5,104.07) rot=(-0.281085,-0.678598,0.678598;3.68962rad)
  LinkedObject = -> Part011
  Placement = pos=(2293.84,-292.5,104.07) rot=(-0.281085,-0.678598,0.678598;3.68962rad)
  expr: Placement = A9.Placement * renf.Placement * AttachmentOffset * b1.Placement ^ -1
FEATURE [App::Link] A18001
  AssemblyType = Asm4EE
  AttachedBy = #b1
  AttachedTo = A9001#renf
  AttachmentOffset = pos=(0,0,0) rot=(-1,0,0;2.35619rad)
  LinkPlacement = pos=(2293.84,292.5,104.07) rot=(-0.281085,-0.678598,0.678598;3.68962rad)
  LinkedObject = -> Part011
  Placement = pos=(2293.84,292.5,104.07) rot=(-0.281085,-0.678598,0.678598;3.68962rad)
  expr: Placement = A9001.Placement * renf.Placement * AttachmentOffset * b1.Placement ^ -1
FEATURE [App::Link] A18002
  AssemblyType = Asm4EE
  AttachedBy = #b1
  AttachedTo = A12002#renf001
  AttachmentOffset = pos=(0,0,0) rot=(1,0,0;0.785398rad)
  LinkPlacement = pos=(2001.16,-292.5,-104.07) rot=(0.862856,-0.357407,0.357407;1.71777rad)
  LinkedObject = -> Part011
  Placement = pos=(2001.16,-292.5,-104.07) rot=(0.862856,-0.357407,0.357407;1.71777rad)
  expr: Placement = A12002.Placement * renf001.Placement * AttachmentOffset * b1.Placement ^ -1
FEATURE [App::Link] A18003
  AssemblyType = Asm4EE
  AttachedBy = #b1
  AttachedTo = A12003#renf001
  AttachmentOffset = pos=(0,0,0) rot=(1,0,0;0.785398rad)
  LinkPlacement = pos=(2001.16,292.5,-104.07) rot=(0.862856,-0.357407,0.357407;1.71777rad)
  LinkedObject = -> Part011
  Placement = pos=(2001.16,292.5,-104.07) rot=(0.862856,-0.357407,0.357407;1.71777rad)
  expr: Placement = A12003.Placement * renf001.Placement * AttachmentOffset * b1.Placement ^ -1
FEATURE [Spreadsheet::Sheet] BOM
  cells = A1='Qty.; B1='Nom_de_la_piece; C1='Reference_AP; D1='Angle1; E1='Angle2; F1='percage; G1='longueur; A2=4; B2='A2; C2='Tube carré 25 x 2; G2=610; A3=2; B3='A1; C3='Tube carré 25 x 2; G3=2285; A4=2; B4='A3; C4='fer rond Ø10; G4=2140; A5=2; B5='A4; C5='fer rond Ø10; G5=90; A6=2; B6='A5; C6='Tube carré 25 x 2; G6=258.5; A7=1; B7='A6; C7='Tube carré 25 x 2; G7=420; A8=2; B8='A7; C8='Tube carré 25 x 2; G8=1960; A9=1; B9='A8; C9='Tube carré 25 x 2; G9=560; A10=2; B10='A9; C10='Tube carré 25 x 2; G10=215; A11=4; B11='A12; C11='Tube carré 25 x 2; G11=400; A12=4; B12='A13; C12='Tube carré 25 x 2; D12=33.49; E12=56.51; G12=449.646319854351; A13=4; B13='A14; C13='Tube carré 25 x 2; D13=19.66; E13=19.66; G13=772.835249419013; A14=2; B14='A11; C14='UPN 30 x 15; G14=46; A15=2; B15='A10; C15='fer rond Ø25; G15=150; A16=2; B16='roue; C16='Roue increvable Ø389 Øaxe25 L 82; A17=4; B17='A15; C17='Tube carré 25 x 2; D17=30.03; E17=59.97; G17=462; A18=2; B18='A16; C18='Tube carré 30 x 2; G18=50; A19=2; B19='BB1; C19='Tube carré 25 x 2; G19=685; A20=4; B20='BB2; C20='Tube carré 25 x 2; G20=560; A21=2; B21='A17; C21='Tube rond 30 x 2; G21=300; A22=4; B22='A18; C22='Tube carré 25 x 2; D22=45; E22=45; G22=142; A23=4; B23='rondelle 25; C23='rondelle 25; A24=2; B24='goupille elastique 5 x 80; C24='goupille elastique 5 x 80
FEATURE [TechDraw::DrawSVGTemplate] Template  label="Modèle"
  Height = 210
  Orientation = 1
  Template = C:/Program Files/FreeCAD_0.19/data/Mod/TechDraw/Templates/A4_LandscapeTDteste.svg
  Width = 297
FEATURE [TechDraw::DrawSVGTemplate] Template001  label="Modèle001"
  Height = 210
  Orientation = 1
  Template = C:/Program Files/FreeCAD_0.19/data/Mod/TechDraw/Templates/A4_LandscapeTDteste.svg
  Width = 297
FEATURE [Sketcher::SketchObject] Sketch026
  ArcFitTolerance = 1e-06
  AttachmentSupport = -> [YZ_Plane044]
  ExternalGeometry = -> [Pad019]
  FullyConstrained = false
  MakeInternals = false
  MapMode = 5
  Placement = pos=(0,0,0) rot=(0.57735,0.57735,0.57735;2.0944rad)
  sketch-geometry (5):
    g0: LineSegment [constr] StartX=-12.5 StartY=34.6544 StartZ=0 EndX=-12.5 EndY=-40.7923 EndZ=0
    g1: LineSegment StartX=-12.5 StartY=-17.5 StartZ=0 EndX=57.5 EndY=-17.5 EndZ=0
    g2: LineSegment StartX=57.5 StartY=-17.5 StartZ=0 EndX=57.5 EndY=17.5 EndZ=0
    g3: LineSegment StartX=57.5 StartY=17.5 StartZ=0 EndX=-12.5 EndY=17.5 EndZ=0
    g4: LineSegment StartX=-12.5 StartY=17.5 StartZ=0 EndX=-12.5 EndY=-17.5 EndZ=0
  constraints (13):
    c: Coincident(g1,g2)
    c: Coincident(g2,g3)
    c: Coincident(g3,g4)
    c: Coincident(g4,g1)
    c: Horizontal(g3)
    c: Vertical(g2)
    c: Distance(g2,g4) = 70
    c: Distance(g1,g3) = 35
    c: Vertical(g0)
    c: PointOnObject(g-3,g0)
    c: Symmetric(g3,g1,g-1)
    c: PointOnObject(g3,g0)
    c: Horizontal(g1)
FEATURE [PartDesign::Plane] DatumPlane
  AttachmentSupport = -> [Pad019]
  Length = 60
  MapMode = 5
  Placement = pos=(142,6.25e-14,0) rot=(0.57735,0.57735,0.57735;2.0944rad)
  ResizeMode = 0
  Width = 60
FEATURE [Sketcher::SketchObject] Sketch027
  ArcFitTolerance = 1e-06
  AttachmentSupport = -> [DatumPlane]
  ExternalGeometry = -> [Pad019]
  FullyConstrained = false
  MakeInternals = false
  MapMode = 5
  Placement = pos=(142,6.25e-14,0) rot=(0.57735,0.57735,0.57735;2.0944rad)
  sketch-geometry (5):
    g0: LineSegment [constr] StartX=-12.5 StartY=-38.9997 StartZ=0 EndX=-12.5 EndY=36.6406 EndZ=0
    g1: LineSegment StartX=-12.5 StartY=-17.5 StartZ=0 EndX=57.5 EndY=-17.5 EndZ=0
    g2: LineSegment StartX=57.5 StartY=-17.5 StartZ=0 EndX=57.5 EndY=17.5 EndZ=0
    g3: LineSegment StartX=57.5 StartY=17.5 StartZ=0 EndX=-12.5 EndY=17.5 EndZ=0
    g4: LineSegment StartX=-12.5 StartY=17.5 StartZ=0 EndX=-12.5 EndY=-17.5 EndZ=0
  constraints (13):
    c: Coincident(g1,g2)
    c: Coincident(g2,g3)
    c: Coincident(g3,g4)
    c: Coincident(g4,g1)
    c: Horizontal(g3)
    c: Vertical(g2)
    c: Distance(g2,g4) = 70
    c: Distance(g1,g3) = 35
    c: PointOnObject(g0,g-4)
    c: Vertical(g0)
    c: Symmetric(g3,g1,g-1)
    c: Horizontal(g1)
    c: PointOnObject(g1,g0)
FEATURE [PartDesign::Groove] Groove
  Angle = 45
  Angle2 = 60
  Axis = (0,0,-75.4468)
  Base = (0,-12.5,34.6544)
  BaseFeature = -> Pad019
  Placement = pos=(0,0,0) rot=(0.57735,0.57735,0.57735;2.0944rad)
  Profile = -> Sketch026
  ReferenceAxis = -> Sketch026 [Axis]
  Suppressed = false
  Type = 0
FEATURE [PartDesign::Groove] Groove001
  Angle = 45
  Angle2 = 60
  Axis = (0,0,75.6403)
  Base = (142,-12.5,-38.9997)
  BaseFeature = -> Groove
  Placement = pos=(0,0,0) rot=(0.57735,0.57735,0.57735;2.0944rad)
  Profile = -> Sketch027
  ReferenceAxis = -> Sketch027 [Axis]
  Suppressed = false
  Type = 0
FEATURE [PartDesign::Body] Body017
  AllowCompound = false
  Group = -> [Sketch025,Pad019,Sketch026,DatumPlane,Sketch027,Groove,Groove001]
  Origin = -> Origin044
  Tip = -> Groove001
FEATURE [App::Part] Part011  label="A18"
  Group = -> [Body017,b1]
  Nom_de_la_piece = 'A18
  Origin = -> Origin043
  Placement = pos=(0,0,0) rot=(1,0,0;1.5708rad)
  Reference_AP = Tube carré 25 x 2
  longueur = 142
FEATURE [Sketcher::SketchObject] Sketch028
  ArcFitTolerance = 1e-06
  AttachmentSupport = -> [YZ_Plane029]
  ExternalGeometry = -> [Pad011]
  FullyConstrained = false
  MakeInternals = false
  MapMode = 5
  Placement = pos=(0,0,0) rot=(0.57735,0.57735,0.57735;2.0944rad)
  sketch-geometry (5):
    g0: LineSegment StartX=-17.5 StartY=12.5 StartZ=0 EndX=-17.5 EndY=-57.5 EndZ=0
    g1: LineSegment StartX=-17.5 StartY=-57.5 StartZ=0 EndX=17.5 EndY=-57.5 EndZ=0
    g2: LineSegment StartX=17.5 StartY=-57.5 StartZ=0 EndX=17.5 EndY=12.5 EndZ=0
    g3: LineSegment StartX=17.5 StartY=12.5 StartZ=0 EndX=-17.5 EndY=12.5 EndZ=0
    g4: LineSegment [constr] StartX=-59.8857 StartY=12.5 StartZ=0 EndX=133.957 EndY=12.5 EndZ=0
  constraints (13):
    c: Coincident(g0,g1)
    c: Coincident(g1,g2)
    c: Coincident(g2,g3)
    c: Coincident(g3,g0)
    c: Vertical(g0)
    c: Vertical(g2)
    c: Horizontal(g1)
    c: Horizontal(g4)
    c: PointOnObject(g2,g4)
    c: DistanceX(g1,g1) = 35
    c: DistanceY(g2,g2) = 70
    c: Symmetric(g0,g2,g-2)
    c: PointOnObject(g-3,g4)
FEATURE [PartDesign::Groove] Groove002
  Angle = 56.5107
  Angle2 = 60
  Axis = (0,193.843,0)
  Base = (0,-59.8857,12.5)
  BaseFeature = -> Pad011
  Placement = pos=(0,0,0) rot=(0.57735,0.57735,0.57735;2.0944rad)
  Profile = -> Sketch028
  ReferenceAxis = -> Sketch028 [Axis]
  Reversed = true
  Suppressed = false
  Type = 0
  expr: Angle = 90 ° - Sketch014.Constraints.angle
FEATURE [PartDesign::Plane] DatumPlane001
  AttachmentSupport = -> [Groove002]
  Length = 60
  MapMode = 5
  Placement = pos=(449.646,1.978e-13,0) rot=(0.57735,0.57735,0.57735;2.0944rad)
  ResizeMode = 0
  Width = 60
FEATURE [Sketcher::SketchObject] Sketch029
  ArcFitTolerance = 1e-06
  AttachmentSupport = -> [DatumPlane001]
  ExternalGeometry = -> [Groove002]
  FullyConstrained = false
  MakeInternals = false
  MapMode = 5
  Placement = pos=(449.646,1.978e-13,0) rot=(0.57735,0.57735,0.57735;2.0944rad)
  sketch-geometry (5):
    g0: LineSegment [constr] StartX=-50.285 StartY=12.5 StartZ=0 EndX=61.7161 EndY=12.5 EndZ=0
    g1: LineSegment StartX=-17.5 StartY=12.5 StartZ=0 EndX=-17.5 EndY=-57.5 EndZ=0
    g2: LineSegment StartX=-17.5 StartY=-57.5 StartZ=0 EndX=17.5 EndY=-57.5 EndZ=0
    g3: LineSegment StartX=17.5 StartY=-57.5 StartZ=0 EndX=17.5 EndY=12.5 EndZ=0
    g4: LineSegment StartX=17.5 StartY=12.5 StartZ=0 EndX=-17.5 EndY=12.5 EndZ=0
  constraints (13):
    c: Horizontal(g0)
    c: PointOnObject(g-3,g0)
    c: Coincident(g1,g2)
    c: Coincident(g2,g3)
    c: Coincident(g3,g4)
    c: Coincident(g4,g1)
    c: Vertical(g1)
    c: Vertical(g3)
    c: Horizontal(g2)
    c: Distance(g1,g3) = 35
    c: Distance(g2,g4) = 70
    c: PointOnObject(g1,g0)
    c: Symmetric(g3,g1,g-2)
FEATURE [App::Link] A18004
  AttachedBy = #B1001
  AttachedTo = A12#B2
  AttachmentOffset = pos=(0,-12.5,0) rot=(1,0,0;-0.584499rad)
  LinkPlacement = pos=(14.5751,-292.5,-405.603) rot=(-0.880847,0,-0.473402;3.14159rad)
  LinkedObject = -> Part003
  Placement = pos=(14.5751,-292.5,-405.603) rot=(-0.880847,0,-0.473402;3.14159rad)
  SolverId = Asm4EE
  expr: .AttachmentOffset.Rotation.Angle = -Sketch014.Constraints.angle
  expr: Placement = A12.Placement * B2.Placement * AttachmentOffset * B1001.Placement ^ -1
FEATURE [App::Link] A13  label="A18005"
  AttachedBy = #B1001
  AttachedTo = A12001#B2
  AttachmentOffset = pos=(0,-12.5,0) rot=(1,0,0;-0.584499rad)
  LinkPlacement = pos=(14.5751,292.5,-405.603) rot=(0.880847,0,0.473402;3.14159rad)
  LinkedObject = -> Part003
  Placement = pos=(14.5751,292.5,-405.603) rot=(0.880847,0,0.473402;3.14159rad)
  SolverId = Asm4EE
  expr: .AttachmentOffset.Rotation.Angle = -Sketch014.Constraints.angle
  expr: Placement = A12001.Placement * B2.Placement * AttachmentOffset * B1001.Placement ^ -1
FEATURE [App::Link] A18005  label="A18006"
  AttachedBy = #B1001
  AttachedTo = A12003#B2
  AttachmentOffset = pos=(12.5,0,0) rot=(-0.276846,-0.276846,0.92017;1.6539rad)
  LinkPlacement = pos=(1995.42,292.5,-405.603) rot=(0,1,0;4.12789rad)
  LinkedObject = -> Part003
  Placement = pos=(1995.42,292.5,-405.603) rot=(0,1,0;4.12789rad)
  SolverId = Asm4EE
  expr: .AttachmentOffset.Rotation.Roll = -Sketch014.Constraints.angle
  expr: Placement = A12003.Placement * B2.Placement * AttachmentOffset * B1001.Placement ^ -1
FEATURE [PartDesign::Groove] Groove003
  Angle = 33.4893
  Angle2 = 60
  Axis = (-1.492e-13,112.001,0)
  Base = (449.646,-50.285,12.5)
  BaseFeature = -> Groove002
  Placement = pos=(0,0,0) rot=(0.57735,0.57735,0.57735;2.0944rad)
  Profile = -> Sketch029
  ReferenceAxis = -> Sketch029 [Axis]
  Suppressed = false
  Type = 0
  expr: Angle = Sketch014.Constraints.angle
FEATURE [PartDesign::Body] Body009
  AllowCompound = false
  Group = -> [Sketch016,Pad011,Sketch028,Groove002,DatumPlane001,Sketch029,Groove003]
  Origin = -> Origin029
  Tip = -> Groove003
FEATURE [App::Part] Part003  label="A13"
  Group = -> [Body009,B1001,B2001]
  Nom_de_la_piece = 'A13
  Origin = -> Origin026
  Reference_AP = Tube carré 25 x 2
  longueur = 450
FEATURE [Sketcher::SketchObject] Sketch030
  ArcFitTolerance = 1e-06
  AttachmentSupport = -> [YZ_Plane032]
  ExternalGeometry = -> [Pad013]
  FullyConstrained = false
  MakeInternals = false
  MapMode = 5
  Placement = pos=(0,0,0) rot=(0.57735,0.57735,0.57735;2.0944rad)
  sketch-geometry (5):
    g0: LineSegment StartX=12.5 StartY=17.5 StartZ=0 EndX=-57.5 EndY=17.5 EndZ=0
    g1: LineSegment StartX=-57.5 StartY=17.5 StartZ=0 EndX=-57.5 EndY=-17.5 EndZ=0
    g2: LineSegment StartX=-57.5 StartY=-17.5 StartZ=0 EndX=12.5 EndY=-17.5 EndZ=0
    g3: LineSegment StartX=12.5 StartY=-17.5 StartZ=0 EndX=12.5 EndY=17.5 EndZ=0
    g4: LineSegment [constr] StartX=12.5 StartY=37.849 StartZ=0 EndX=12.5 EndY=-63.3268 EndZ=0
  constraints (13):
    c: Coincident(g0,g1)
    c: Coincident(g1,g2)
    c: Coincident(g2,g3)
    c: Coincident(g3,g0)
    c: Horizontal(g0)
    c: Vertical(g3)
    c: Distance(g1,g3) = 70
    c: Distance(g0,g2) = 35
    c: Horizontal(g2)
    c: Symmetric(g0,g1,g-1)
    c: Vertical(g4)
    c: PointOnObject(g-3,g4)
    c: PointOnObject(g2,g4)
FEATURE [PartDesign::Groove] Groove004
  Angle = 59.9743
  Angle2 = 60
  Axis = (0,0,-101.176)
  Base = (0,12.5,37.849)
  BaseFeature = -> Pad013
  Placement = pos=(0,0,0) rot=(0.57735,0.57735,0.57735;2.0944rad)
  Profile = -> Sketch030
  ReferenceAxis = -> Sketch030 [Axis]
  Reversed = true
  Suppressed = false
  Type = 0
  expr: Angle = 90 ° - Sketch014.Constraints.angle2
FEATURE [PartDesign::Plane] DatumPlane002
  AttachmentSupport = -> [Groove004]
  Length = 60
  MapMode = 5
  Placement = pos=(462,2.033e-13,0) rot=(0.57735,0.57735,0.57735;2.0944rad)
  ResizeMode = 0
  Width = 60
FEATURE [Sketcher::SketchObject] Sketch031
  ArcFitTolerance = 1e-06
  AttachmentSupport = -> [DatumPlane002]
  ExternalGeometry = -> [Groove004]
  FullyConstrained = false
  MakeInternals = false
  MapMode = 5
  Placement = pos=(462,2.033e-13,0) rot=(0.57735,0.57735,0.57735;2.0944rad)
  sketch-geometry (5):
    g0: LineSegment [constr] StartX=12.5 StartY=67.6644 StartZ=0 EndX=12.5 EndY=-52.0571 EndZ=0
    g1: LineSegment StartX=-57.5 StartY=17.5 StartZ=0 EndX=-57.5 EndY=-17.5 EndZ=0
    g2: LineSegment StartX=-57.5 StartY=-17.5 StartZ=0 EndX=12.5 EndY=-17.5 EndZ=0
    g3: LineSegment StartX=12.5 StartY=-17.5 StartZ=0 EndX=12.5 EndY=17.5 EndZ=0
    g4: LineSegment StartX=12.5 StartY=17.5 StartZ=0 EndX=-57.5 EndY=17.5 EndZ=0
  constraints (13):
    c: Vertical(g0)
    c: Coincident(g1,g2)
    c: Coincident(g2,g3)
    c: Coincident(g3,g4)
    c: Coincident(g4,g1)
    c: Vertical(g3)
    c: Horizontal(g2)
    c: Horizontal(g4)
    c: Distance(g1,g3) = 70
    c: Distance(g2,g4) = 35
    c: PointOnObject(g3,g-3)
    c: PointOnObject(g0,g-3)
    c: Symmetric(g1,g1,g-1)
FEATURE [PartDesign::Groove] Groove005
  Angle = 30.0257
  Angle2 = 60
  Axis = (0,0,-119.722)
  Base = (462,12.5,67.6644)
  BaseFeature = -> Groove004
  Placement = pos=(0,0,0) rot=(0.57735,0.57735,0.57735;2.0944rad)
  Profile = -> Sketch031
  ReferenceAxis = -> Sketch031 [Axis]
  Suppressed = false
  Type = 0
  expr: Angle = Sketch014.Constraints.angle2
FEATURE [PartDesign::Body] Body011
  AllowCompound = false
  Group = -> [Pad013,Sketch018,Sketch030,Groove004,DatumPlane002,Sketch031,Groove005]
  Origin = -> Origin032
  Tip = -> Groove005
FEATURE [App::Part] Part005  label="A15"
  Group = -> [Body011,cote1]
  Nom_de_la_piece = 'A15
  Origin = -> Origin031
  Reference_AP = Tube carré 25 x 2
  longueur = 462
FEATURE [Sketcher::SketchObject] Sketch032
  ArcFitTolerance = 1e-06
  AttachmentSupport = -> [YZ_Plane030]
  ExternalGeometry = -> [Pad012]
  FullyConstrained = false
  MakeInternals = false
  MapMode = 5
  Placement = pos=(0,0,0) rot=(0.57735,0.57735,0.57735;2.0944rad)
  sketch-geometry (5):
    g0: LineSegment StartX=17.5 StartY=57.5 StartZ=0 EndX=-17.5 EndY=57.5 EndZ=0
    g1: LineSegment StartX=-17.5 StartY=57.5 StartZ=0 EndX=-17.5 EndY=-12.5 EndZ=0
    g2: LineSegment StartX=-17.5 StartY=-12.5 StartZ=0 EndX=17.5 EndY=-12.5 EndZ=0
    g3: LineSegment StartX=17.5 StartY=-12.5 StartZ=0 EndX=17.5 EndY=57.5 EndZ=0
    g4: LineSegment [constr] StartX=69.7742 StartY=-12.5 StartZ=0 EndX=-82.9271 EndY=-12.5 EndZ=0
  constraints (13):
    c: Coincident(g0,g1)
    c: Coincident(g1,g2)
    c: Coincident(g2,g3)
    c: Coincident(g3,g0)
    c: Horizontal(g0)
    c: Vertical(g1)
    c: Vertical(g3)
    c: Distance(g1,g3) = 35
    c: Distance(g0,g2) = 70
    c: Symmetric(g1,g2,g-2)
    c: PointOnObject(g1,g-3)
    c: Horizontal(g4)
    c: PointOnObject(g2,g4)
FEATURE [PartDesign::Groove] Groove006
  Angle = 19.6557
  Angle2 = 60
  Axis = (0,-152.701,0)
  Base = (0,69.7742,-12.5)
  BaseFeature = -> Pad012
  Placement = pos=(0,0,0) rot=(0.57735,0.57735,0.57735;2.0944rad)
  Profile = -> Sketch032
  ReferenceAxis = -> Sketch032 [Axis]
  Reversed = true
  Suppressed = false
  Type = 0
  expr: Angle = 90 ° - Sketch014.Constraints.anglerou
FEATURE [PartDesign::Plane] DatumPlane003
  AttachmentSupport = -> [Groove006]
  Length = 60
  MapMode = 5
  Placement = pos=(772.835,3.4e-13,0) rot=(0.57735,0.57735,0.57735;2.0944rad)
  ResizeMode = 0
  Width = 60
FEATURE [Sketcher::SketchObject] Sketch033
  ArcFitTolerance = 1e-06
  AttachmentSupport = -> [DatumPlane003]
  ExternalGeometry = -> [Groove006]
  FullyConstrained = false
  MakeInternals = false
  MapMode = 5
  Placement = pos=(772.835,3.4e-13,0) rot=(0.57735,0.57735,0.57735;2.0944rad)
  sketch-geometry (5):
    g0: LineSegment [constr] StartX=-118.894 StartY=12.5 StartZ=0 EndX=112.379 EndY=12.5 EndZ=0
    g1: LineSegment StartX=-17.5 StartY=12.5 StartZ=0 EndX=-17.5 EndY=-57.5 EndZ=0
    g2: LineSegment StartX=-17.5 StartY=-57.5 StartZ=0 EndX=17.5 EndY=-57.5 EndZ=0
    g3: LineSegment StartX=17.5 StartY=-57.5 StartZ=0 EndX=17.5 EndY=12.5 EndZ=0
    g4: LineSegment StartX=17.5 StartY=12.5 StartZ=0 EndX=-17.5 EndY=12.5 EndZ=0
  constraints (13):
    c: Horizontal(g0)
    c: Coincident(g1,g2)
    c: Coincident(g2,g3)
    c: Coincident(g3,g4)
    c: Coincident(g4,g1)
    c: Vertical(g1)
    c: Vertical(g3)
    c: Horizontal(g2)
    c: Distance(g1,g3) = 35
    c: Distance(g2,g4) = 70
    c: PointOnObject(g1,g0)
    c: Symmetric(g3,g1,g-2)
    c: PointOnObject(g-3,g0)
FEATURE [PartDesign::Groove] Groove007
  Angle = 19.66
  Angle2 = 60
  Axis = (-3.081e-13,231.273,0)
  Base = (772.835,-118.894,12.5)
  BaseFeature = -> Groove006
  Placement = pos=(0,0,0) rot=(0.57735,0.57735,0.57735;2.0944rad)
  Profile = -> Sketch033
  ReferenceAxis = -> Sketch033 [Axis]
  Suppressed = false
  Type = 0
FEATURE [PartDesign::Body] Body010
  AllowCompound = false
  Group = -> [Sketch017,Pad012,Sketch032,Groove006,DatumPlane003,Sketch033,Groove007]
  Origin = -> Origin030
  Tip = -> Groove007
FEATURE [App::Part] Part004  label="A14"
  Group = -> [Body010,B1002,B2002]
  Nom_de_la_piece = 'A14
  Origin = -> Origin027
  Reference_AP = Tube carré 25 x 2
  longueur = 788
FEATURE [TechDraw::DrawProjGroupItem] View003
  CoarseView = false
  Direction = (0.57735,-0.57735,0.57735)
  Focus = 100
  HardHidden = false
  IsoCount = 0
  IsoHidden = false
  IsoVisible = false
  LockPosition = false
  Perspective = false
  Rotation = 0
  RotationVector = (1,0,0)
  Scale = 0.066667
  ScaleType = 2
  ScrubCount = 1
  SeamHidden = false
  SeamVisible = false
  SmoothHidden = false
  SmoothVisible = true
  Type = 0
  X = 117.09
  XDirection = (0.707107,0.707107,0)
  XSource = -> [Roue_increvable___389___axe25_L_82002]
  Y = 35
FEATURE [TechDraw::DrawProjGroupItem] View004
  CoarseView = false
  Direction = (0.57735,-0.57735,0.57735)
  Focus = 100
  HardHidden = false
  IsoCount = 0
  IsoHidden = false
  IsoVisible = false
  LockPosition = false
  Perspective = false
  Rotation = 0
  RotationVector = (1,0,0)
  Scale = 0.066667
  ScaleType = 2
  ScrubCount = 1
  SeamHidden = false
  SeamVisible = false
  SmoothHidden = false
  SmoothVisible = true
  Type = 0
  X = 196.962
  XDirection = (0.707107,0.707107,0)
  XSource = -> [Roue_increvable___389___axe25_L_82001]
  Y = 89.7436
FEATURE [TechDraw::DrawProjGroupItem] View005
  CoarseView = false
  Direction = (0.57735,-0.57735,0.57735)
  Focus = 100
  HardHidden = false
  IsoCount = 0
  IsoHidden = false
  IsoVisible = false
  LockPosition = false
  Perspective = false
  Rotation = 0
  RotationVector = (1,0,0)
  Scale = 0.066667
  ScaleType = 2
  ScrubCount = 1
  SeamHidden = false
  SeamVisible = false
  SmoothHidden = false
  SmoothVisible = true
  Type = 0
  X = 163.308
  XDirection = (0.707107,0.707107,0)
  XSource = -> [A2001,A1001,A1004,A3001,A3002,A4001,A4002,A2003,A5001,A5002,A6001,A7003,A7004,A8002,A9,A9001,A12,A12001,A12002,A12003,A13001,A14001,A2004,A2005,A14002,A14003,A14004,A11,A11001,A10,A10006,A15,A14008,A15001,A15002,A16,A16001,A17,A17001,A18,A18001,A18002,A18003,A18004,A13,A18005,rondelle_028,rondelle_029]
  Y = 64.6154
FEATURE [TechDraw::DrawSVGTemplate] Template002  label="Modèle002"
  Height = 210
  Orientation = 1
  Template = C:/Program Files/FreeCAD_0.19/data/Mod/TechDraw/Templates/A4_LandscapeTDteste.svg
  Width = 297
FEATURE [TechDraw::DrawProjGroupItem] View006
  CoarseView = false
  Direction = (0.57735,-0.57735,0.57735)
  Focus = 100
  HardHidden = false
  IsoCount = 0
  IsoHidden = false
  IsoVisible = false
  LockPosition = false
  Perspective = false
  Rotation = 0
  RotationVector = (1,0,0)
  Scale = 0.066667
  ScaleType = 2
  ScrubCount = 1
  SeamHidden = false
  SeamVisible = false
  SmoothHidden = false
  SmoothVisible = true
  Type = 0
  X = 81.1923
  XDirection = (0.707107,0.707107,0)
  XSource = -> [BB1,BB1001,BB3,BB2,BB1003,BB1004]
  Y = 133.718
FEATURE [TechDraw::DrawSVGTemplate] Template003  label="Modèle003"
  Height = 210
  Orientation = 1
  Template = C:/Program Files/FreeCAD_0.19/data/Mod/TechDraw/Templates/A4_LandscapeTDteste.svg
  Width = 297
FEATURE [TechDraw::DrawProjGroupItem] View007  label="Front001"
  CoarseView = false
  Direction = (0,-1,0)
  Focus = 100
  HardHidden = false
  IsoCount = 0
  IsoHidden = false
  IsoVisible = false
  LockPosition = true
  Perspective = false
  Rotation = 0
  RotationVector = (1,0,0)
  Scale = 0.066667
  ScaleType = 2
  ScrubCount = 1
  SeamHidden = false
  SeamVisible = false
  SmoothHidden = false
  SmoothVisible = true
  Type = 0
  X = 0
  XDirection = (1,0,0)
  XSource = <same value as first occurrence — deduplicated (x4 in doc)>
  Y = 0
FEATURE [TechDraw::DrawProjGroupItem] ProjItem002  label="Dessous"
  CoarseView = false
  Direction = (0,0,-1)
  Focus = 100
  HardHidden = false
  IsoCount = 0
  IsoHidden = false
  IsoVisible = false
  LockPosition = true
  Perspective = false
  Rotation = 0
  RotationVector = (1,0,0)
  ScaleType = 0
  ScrubCount = 1
  SeamHidden = false
  SeamVisible = false
  SmoothHidden = false
  SmoothVisible = true
  Type = 5
  X = 0
  XDirection = (1,0,0)
  XSource = <same value as first occurrence — deduplicated (x4 in doc)>
  Y = 77.9588
FEATURE [TechDraw::DrawProjGroupItem] ProjItem003  label="Gauche"
  CoarseView = false
  Direction = (-1,-1e-16,0)
  Focus = 100
  HardHidden = false
  IsoCount = 0
  IsoHidden = false
  IsoVisible = false
  LockPosition = false
  Perspective = false
  Rotation = 0
  RotationVector = (1,0,0)
  ScaleType = 0
  ScrubCount = 1
  SeamHidden = false
  SeamVisible = false
  SmoothHidden = false
  SmoothVisible = true
  Type = 1
  X = 125.067
  XDirection = (1e-16,-1,0)
  XSource = <same value as first occurrence — deduplicated (x4 in doc)>
  Y = 0
FEATURE [TechDraw::DrawProjGroup] ProjGroup001
  Anchor = -> View007
  AutoDistribute = true
  LockPosition = false
  ProjectionType = 0
  Rotation = 0
  Scale = 0.066667
  ScaleType = 2
  Views = -> [View007,ProjItem002,ProjItem003]
  X = 119.416
  XSource = -> [A2001,A1001,A1004,A3001,A3002,A4001,A4002,A2003,A5001,A5002,A6001,A7003,A7004,A8002,A9,A9001,A12,A12001,A12002,A12003,A13001,A14001,A2004,A2005,A14002,A14003,A14004,A11,A11001,A10,A10006,A15,A14008,A15001,A15002,A16,A16001,A17,A17001,A18,A18001,A18002,A18003,A18004,A13,A18005]
  Y = 44.0069
  spacingX = 15
  spacingY = 15
FEATURE [TechDraw::DrawSVGTemplate] Template004  label="Modèle004"
  Height = 210
  Orientation = 1
  Template = C:/Program Files/FreeCAD_0.19/data/Mod/TechDraw/Templates/A4_LandscapeTDteste.svg
  Width = 297
FEATURE [TechDraw::DrawPage] Page004  label="Feuille004"
  KeepUpdated = false
  NextBalloonIndex = 1
  ProjectionType = 0
  Template = -> Template004
FEATURE [TechDraw::DrawSVGTemplate] Template005  label="Modèle005"
  Height = 210
  Orientation = 1
  Template = C:/Program Files/FreeCAD_0.19/data/Mod/TechDraw/Templates/A4_LandscapeTDteste.svg
  Width = 297
FEATURE [TechDraw::DrawPage] Page005  label="Feuille005"
  KeepUpdated = false
  NextBalloonIndex = 1
  ProjectionType = 0
  Template = -> Template005
FEATURE [TechDraw::DrawSVGTemplate] Template006  label="Modèle006"
  Height = 210
  Orientation = 1
  Template = C:/Program Files/FreeCAD_0.19/data/Mod/TechDraw/Templates/A4_LandscapeTDteste.svg
  Width = 297
FEATURE [TechDraw::DrawPage] Page006  label="Feuille006"
  KeepUpdated = false
  NextBalloonIndex = 1
  ProjectionType = 0
  Template = -> Template006
FEATURE [TechDraw::DrawProjGroupItem] View008
  CoarseView = false
  Direction = (0,-1,0)
  Focus = 100
  HardHidden = false
  IsoCount = 0
  IsoHidden = false
  IsoVisible = false
  LockPosition = false
  Perspective = false
  Rotation = 0
  RotationVector = (1,0,0)
  Scale = 0.2
  ScaleType = 2
  ScrubCount = 1
  SeamHidden = false
  SeamVisible = false
  SmoothHidden = false
  SmoothVisible = true
  Source = -> [A8004]
  Type = 0
  X = 225.36
  XDirection = (1,0,0)
  Y = 112.75
FEATURE [TechDraw::DrawViewDetail] Detail  label="Detail "
  AnchorPoint = (0,110,0)
  BaseView = -> View008
  CoarseView = false
  Direction = (0,-1,0)
  Focus = 100
  HardHidden = false
  IsoCount = 0
  IsoHidden = false
  IsoVisible = false
  LockPosition = false
  Perspective = false
  Radius = 20
  Rotation = 0
  ScaleType = 2
  ScrubCount = 1
  SeamHidden = false
  SeamVisible = false
  ShowHighlight = true
  ShowMatting = true
  SmoothHidden = false
  SmoothVisible = true
  Source = -> [A8004]
  X = 266.563
  XDirection = (1,0,0)
  Y = 112.75
FEATURE [TechDraw::DrawProjGroupItem] View009  label="Front002"
  CoarseView = false
  Direction = (0,-1,0)
  Focus = 100
  HardHidden = false
  IsoCount = 0
  IsoHidden = false
  IsoVisible = false
  LockPosition = true
  Perspective = false
  Rotation = 0
  RotationVector = (1,0,0)
  Scale = 0.2
  ScaleType = 2
  ScrubCount = 1
  SeamHidden = false
  SeamVisible = false
  SmoothHidden = false
  SmoothVisible = true
  Type = 0
  X = 0
  XDirection = (1,0,0)
  XSource = -> [BB1,BB1001,BB3,BB2,BB1003,BB1004]
  Y = 0
FEATURE [TechDraw::DrawProjGroupItem] ProjItem004  label="Gauche001"
  CoarseView = false
  Direction = (-1,-1e-16,0)
  Focus = 100
  HardHidden = false
  IsoCount = 0
  IsoHidden = false
  IsoVisible = false
  LockPosition = false
  Perspective = false
  Rotation = 0
  RotationVector = (1,0,0)
  Scale = 0.2
  ScaleType = 2
  ScrubCount = 1
  SeamHidden = false
  SeamVisible = false
  SmoothHidden = false
  SmoothVisible = true
  Type = 1
  X = 78.5
  XDirection = (1e-16,-1,0)
  XSource = -> [BB1,BB1001,BB3,BB2,BB1003,BB1004]
  Y = 0
FEATURE [TechDraw::DrawProjGroup] ProjGroup002
  Anchor = -> View009
  AutoDistribute = true
  LockPosition = false
  ProjectionType = 0
  Rotation = 0
  Scale = 0.2
  ScaleType = 2
  Views = -> [View009,ProjItem004]
  X = 34.9744
  XSource = -> [BB1,BB1001,BB3,BB2,BB1003,BB1004]
  Y = 90.1923
  spacingX = 15
  spacingY = 15
FEATURE [TechDraw::DrawViewDimension] Dimension003  label="Cote003"
  AngleOverride = false
  Arbitrary = false
  ArbitraryTolerances = false
  BoxCorners = (2) [(-61,-68.5,-1e-07),(61,68.5,1e-07)]
  EqualTolerance = true
  ExtensionAngle = 0
  FormatSpec = %.2w
  FormatSpecOverTolerance = %+.2w
  FormatSpecUnderTolerance = %+.2w
  Inverted = false
  LineAngle = 0
  LockPosition = false
  MeasureType = 1
  OverTolerance = 0
  References2D = -> [ProjItem004]
  Rotation = 0
  ScaleType = 0
  TheoreticalExact = false
  Type = 2
  UnderTolerance = 0
  X = -45.2561
  Y = -67.38
FEATURE [TechDraw::DrawViewDimension] Dimension004  label="Cote004"
  AngleOverride = false
  Arbitrary = false
  ArbitraryTolerances = false
  BoxCorners = (2) [(-61,-68.5,-1e-07),(61,68.5,1e-07)]
  EqualTolerance = true
  ExtensionAngle = 0
  FormatSpec = %.2w
  FormatSpecOverTolerance = %+.2w
  FormatSpecUnderTolerance = %+.2w
  Inverted = false
  LineAngle = 0
  LockPosition = false
  MeasureType = 1
  OverTolerance = 0
  References2D = -> [ProjItem004]
  Rotation = 0
  ScaleType = 0
  TheoreticalExact = false
  Type = 0
  UnderTolerance = 0
  X = -39
  Y = 56.027
FEATURE [TechDraw::DrawViewDimension] Dimension005  label="Cote005"
  AngleOverride = false
  Arbitrary = false
  ArbitraryTolerances = false
  BoxCorners = (2) [(-61,-68.5,-1e-07),(61,68.5,1e-07)]
  EqualTolerance = true
  ExtensionAngle = 0
  FormatSpec = %.2w
  FormatSpecOverTolerance = %+.2w
  FormatSpecUnderTolerance = %+.2w
  Inverted = false
  LineAngle = 0
  LockPosition = false
  MeasureType = 1
  OverTolerance = 0
  References2D = -> [ProjItem004]
  Rotation = 0
  ScaleType = 0
  TheoreticalExact = false
  Type = 0
  UnderTolerance = 0
  X = 0
  Y = 56.027
FEATURE [TechDraw::DrawViewDimension] Dimension006  label="Cote006"
  AngleOverride = false
  Arbitrary = false
  ArbitraryTolerances = false
  BoxCorners = (2) [(-61,-68.5,-1e-07),(61,68.5,1e-07)]
  EqualTolerance = true
  ExtensionAngle = 0
  FormatSpec = %.2w
  FormatSpecOverTolerance = %+.2w
  FormatSpecUnderTolerance = %+.2w
  Inverted = false
  LineAngle = 0
  LockPosition = false
  MeasureType = 1
  OverTolerance = 0
  References2D = -> [ProjItem004]
  Rotation = 0
  ScaleType = 0
  TheoreticalExact = false
  Type = 0
  UnderTolerance = 0
  X = 39
  Y = 56.027
FEATURE [TechDraw::DrawViewDimension] Dimension007  label="Cote007"
  AngleOverride = false
  Arbitrary = false
  ArbitraryTolerances = false
  BoxCorners = (2) [(-61,-68.5,-1e-07),(61,68.5,1e-07)]
  EqualTolerance = true
  ExtensionAngle = 0
  FormatSpec = %.2w
  FormatSpecOverTolerance = %+.2w
  FormatSpecUnderTolerance = %+.2w
  Inverted = false
  LineAngle = 0
  LockPosition = false
  MeasureType = 1
  OverTolerance = 0
  References2D = -> [ProjItem004]
  Rotation = 0
  ScaleType = 0
  TheoreticalExact = false
  Type = 0
  UnderTolerance = 0
  X = -41.5
  Y = 76.7582
FEATURE [TechDraw::DrawViewDimension] Dimension009  label="Cote009"
  AngleOverride = false
  Arbitrary = false
  ArbitraryTolerances = false
  BoxCorners = (2) [(-87.1671,-22.5668,-1e-07),(87.1671,22.5668,1e-07)]
  EqualTolerance = true
  ExtensionAngle = 0
  FormatSpec = %.2w
  FormatSpecOverTolerance = %+.2w
  FormatSpecUnderTolerance = %+.2w
  Inverted = false
  LineAngle = 0
  LockPosition = false
  MeasureType = 1
  OverTolerance = 0
  References2D = -> [ProjItem002]
  Rotation = 0
  ScaleType = 0
  TheoreticalExact = false
  Type = 0
  UnderTolerance = 0
  X = -107.872
  Y = 0
FEATURE [TechDraw::DrawViewDimension] Dimension010  label="Cote010"
  AngleOverride = false
  Arbitrary = false
  ArbitraryTolerances = false
  BoxCorners = (2) [(-87.1671,-22.9001,-1e-07),(87.1671,22.9001,1e-07)]
  EqualTolerance = true
  ExtensionAngle = 0
  FormatSpec = %.2w
  FormatSpecOverTolerance = %+.2w
  FormatSpecUnderTolerance = %+.2w
  Inverted = false
  LineAngle = 0
  LockPosition = false
  MeasureType = 1
  OverTolerance = 0
  References2D = -> [ProjItem002]
  Rotation = 0
  ScaleType = 0
  TheoreticalExact = false
  Type = 0
  UnderTolerance = 0
  X = -98.2304
  Y = 17.454
FEATURE [TechDraw::DrawViewDimension] Dimension011  label="Cote011"
  AngleOverride = false
  Arbitrary = false
  ArbitraryTolerances = false
  BoxCorners = (2) [(-87.1671,-22.5668,-1e-07),(87.1671,22.5668,1e-07)]
  EqualTolerance = true
  ExtensionAngle = 0
  FormatSpec = %.2w
  FormatSpecOverTolerance = %+.2w
  FormatSpecUnderTolerance = %+.2w
  Inverted = false
  LineAngle = 0
  LockPosition = false
  MeasureType = 1
  OverTolerance = 0
  References2D = -> [ProjItem002]
  Rotation = 0
  ScaleType = 0
  TheoreticalExact = false
  Type = 2
  UnderTolerance = 0
  X = -98.2304
  Y = -20.6232
FEATURE [TechDraw::DrawViewDimension] Dimension012  label="Cote012"
  AngleOverride = false
  Arbitrary = false
  ArbitraryTolerances = false
  BoxCorners = (2) [(-87.1671,-22.9001,-1e-07),(87.1671,22.9001,1e-07)]
  EqualTolerance = true
  ExtensionAngle = 0
  FormatSpec = %.0w
  FormatSpecOverTolerance = %+.2w
  FormatSpecUnderTolerance = %+.2w
  Inverted = false
  LineAngle = 0
  LockPosition = false
  MeasureType = 1
  OverTolerance = 0
  References2D = -> [ProjItem002]
  Rotation = 0
  ScaleType = 0
  TheoreticalExact = false
  Type = 0
  UnderTolerance = 0
  X = -71.044
  Y = 42.2166
FEATURE [TechDraw::DrawViewDimension] Dimension013  label="Cote013"
  AngleOverride = false
  Arbitrary = false
  ArbitraryTolerances = false
  BoxCorners = (2) [(-87.1671,-22.9001,-1e-07),(87.1671,22.9001,1e-07)]
  EqualTolerance = true
  ExtensionAngle = 0
  FormatSpec = %.0w
  FormatSpecOverTolerance = %+.2w
  FormatSpecUnderTolerance = %+.2w
  Inverted = false
  LineAngle = 0
  LockPosition = false
  MeasureType = 1
  OverTolerance = 0
  References2D = -> [ProjItem002]
  Rotation = 0
  ScaleType = 0
  TheoreticalExact = false
  Type = 0
  UnderTolerance = 0
  X = -71.3678
  Y = 32.7327
FEATURE [TechDraw::DrawViewDimension] Dimension014  label="Cote014"
  AngleOverride = false
  Arbitrary = false
  ArbitraryTolerances = false
  BoxCorners = (2) [(-87.1671,-22.9001,-1e-07),(87.1671,22.9001,1e-07)]
  EqualTolerance = true
  ExtensionAngle = 0
  FormatSpec = %.2w
  FormatSpecOverTolerance = %+.2w
  FormatSpecUnderTolerance = %+.2w
  Inverted = false
  LineAngle = 0
  LockPosition = false
  MeasureType = 1
  OverTolerance = 0
  References2D = -> [ProjItem002]
  Rotation = 0
  ScaleType = 0
  TheoreticalExact = false
  Type = 0
  UnderTolerance = 0
  X = -18.1668
  Y = 27.79
FEATURE [TechDraw::DrawViewDimension] Dimension015  label="Cote015"
  AngleOverride = false
  Arbitrary = false
  ArbitraryTolerances = false
  BoxCorners = (2) [(-87.1671,-22.9001,-1e-07),(87.1671,22.9001,1e-07)]
  EqualTolerance = true
  ExtensionAngle = 0
  FormatSpec = %.0w
  FormatSpecOverTolerance = %+.2w
  FormatSpecUnderTolerance = %+.2w
  Inverted = false
  LineAngle = 0
  LockPosition = false
  MeasureType = 1
  OverTolerance = 0
  References2D = -> [ProjItem002]
  Rotation = 0
  ScaleType = 0
  TheoreticalExact = false
  Type = 0
  UnderTolerance = 0
  X = 45.2428
  Y = 33.3687
FEATURE [TechDraw::DrawViewDimension] Dimension016  label="Cote016"
  AngleOverride = false
  Arbitrary = false
  ArbitraryTolerances = false
  BoxCorners = (2) [(-2.5,-21.5,-1e-07),(2.5,21.5,1e-07)]
  EqualTolerance = true
  ExtensionAngle = 0
  FormatSpec = ⌀%.2w
  FormatSpecOverTolerance = %+.2w
  FormatSpecUnderTolerance = %+.2w
  Inverted = false
  LineAngle = 0
  LockPosition = false
  MeasureType = 1
  OverTolerance = 0
  References2D = -> [View008]
  Rotation = 0
  ScaleType = 0
  TheoreticalExact = false
  Type = 5
  UnderTolerance = 0
  X = 11.3357
  Y = -3.66822
FEATURE [TechDraw::DrawViewDimension] Dimension017  label="Cote017"
  AngleOverride = false
  Arbitrary = false
  ArbitraryTolerances = false
  BoxCorners = (2) [(-87.1671,-22.5668,-1e-07),(87.1671,22.5668,1e-07)]
  EqualTolerance = true
  ExtensionAngle = 0
  FormatSpec = %.2w
  FormatSpecOverTolerance = %+.2w
  FormatSpecUnderTolerance = %+.2w
  Inverted = false
  LineAngle = 0
  LockPosition = false
  MeasureType = 1
  OverTolerance = 0
  References2D = -> [ProjItem002]
  Rotation = 0
  ScaleType = 0
  TheoreticalExact = false
  Type = 0
  UnderTolerance = 0
  X = 63.8298
  Y = -8.55098
FEATURE [TechDraw::DrawViewDimension] Dimension018  label="Cote018"
  AngleOverride = false
  Arbitrary = false
  ArbitraryTolerances = false
  BoxCorners = (2) [(-87.1671,-22.5668,-1e-07),(87.1671,22.5668,1e-07)]
  EqualTolerance = true
  ExtensionAngle = 0
  FormatSpec = %.2w
  FormatSpecOverTolerance = %+.2w
  FormatSpecUnderTolerance = %+.2w
  Inverted = false
  LineAngle = 0
  LockPosition = false
  MeasureType = 1
  OverTolerance = 0
  References2D = -> [ProjItem002]
  Rotation = 0
  ScaleType = 0
  TheoreticalExact = false
  Type = 0
  UnderTolerance = 0
  X = 58.1049
  Y = 2.43473
FEATURE [TechDraw::DrawViewDimension] Dimension020  label="Cote020"
  AngleOverride = false
  Arbitrary = false
  ArbitraryTolerances = false
  BoxCorners = (2) [(-87.1671,-22.5668,-1e-07),(87.1671,22.5668,1e-07)]
  EqualTolerance = true
  ExtensionAngle = 0
  FormatSpec = %.2w
  FormatSpecOverTolerance = %+.2w
  FormatSpecUnderTolerance = %+.2w
  Inverted = false
  LineAngle = 0
  LockPosition = false
  MeasureType = 1
  OverTolerance = 0
  References2D = -> [ProjItem002]
  Rotation = 0
  ScaleType = 0
  TheoreticalExact = false
  Type = 1
  UnderTolerance = 0
  X = 25.7501
  Y = -41.9707
FEATURE [TechDraw::DrawViewDimension] Dimension021  label="Cote021"
  AngleOverride = false
  Arbitrary = false
  ArbitraryTolerances = false
  BoxCorners = (2) [(-87.1671,-22.5668,-1e-07),(87.1671,22.5668,1e-07)]
  EqualTolerance = true
  ExtensionAngle = 0
  FormatSpec = %.2w
  FormatSpecOverTolerance = %+.2w
  FormatSpecUnderTolerance = %+.2w
  Inverted = false
  LineAngle = 0
  LockPosition = false
  MeasureType = 1
  OverTolerance = 0
  References2D = -> [ProjItem002]
  Rotation = 0
  ScaleType = 0
  TheoreticalExact = false
  Type = 1
  UnderTolerance = 0
  X = -52.0836
  Y = -29.1448
FEATURE [TechDraw::DrawViewDimension] Dimension022  label="Cote022"
  AngleOverride = false
  Arbitrary = false
  ArbitraryTolerances = false
  BoxCorners = (2) [(-87.1671,-22.5668,-1e-07),(87.1671,22.5668,1e-07)]
  EqualTolerance = true
  ExtensionAngle = 0
  FormatSpec = %.2w
  FormatSpecOverTolerance = %+.2w
  FormatSpecUnderTolerance = %+.2w
  Inverted = false
  LineAngle = 0
  LockPosition = false
  MeasureType = 1
  OverTolerance = 0
  References2D = -> [ProjItem002]
  Rotation = 0
  ScaleType = 0
  TheoreticalExact = false
  Type = 1
  UnderTolerance = 0
  X = 15.7501
  Y = -29.1448
FEATURE [TechDraw::DrawViewDimension] Dimension023  label="Cote023"
  AngleOverride = false
  Arbitrary = false
  ArbitraryTolerances = false
  BoxCorners = (2) [(-87.1671,-22.11,-1e-07),(87.1671,22.1097,1e-07)]
  EqualTolerance = true
  ExtensionAngle = 0
  FormatSpec = %.0w
  FormatSpecOverTolerance = %+.2w
  FormatSpecUnderTolerance = %+.2w
  Inverted = false
  LineAngle = 0
  LockPosition = false
  MeasureType = 1
  OverTolerance = 0
  References2D = -> [View007]
  Rotation = 0
  ScaleType = 0
  TheoreticalExact = false
  Type = 1
  UnderTolerance = 0
  X = 67.271
  Y = -17.3286
FEATURE [TechDraw::DrawViewDimension] Dimension024  label="Cote024"
  AngleOverride = false
  Arbitrary = false
  ArbitraryTolerances = false
  BoxCorners = (2) [(-87.1671,-22.11,-1e-07),(87.1671,22.1097,1e-07)]
  EqualTolerance = true
  ExtensionAngle = 0
  FormatSpec = %.0w
  FormatSpecOverTolerance = %+.2w
  FormatSpecUnderTolerance = %+.2w
  Inverted = false
  LineAngle = 0
  LockPosition = false
  MeasureType = 1
  OverTolerance = 0
  References2D = -> [View007]
  Rotation = 0
  ScaleType = 0
  TheoreticalExact = false
  Type = 2
  UnderTolerance = 0
  X = 80.9001
  Y = 6.41069
FEATURE [TechDraw::DrawViewDimension] Dimension025  label="Cote025"
  AngleOverride = false
  Arbitrary = false
  ArbitraryTolerances = false
  BoxCorners = (2) [(-87.1671,-22.11,-1e-07),(87.1671,22.1097,1e-07)]
  EqualTolerance = true
  ExtensionAngle = 0
  FormatSpec = %.2w
  FormatSpecOverTolerance = %+.2w
  FormatSpecUnderTolerance = %+.2w
  Inverted = false
  LineAngle = 0
  LockPosition = false
  MeasureType = 1
  OverTolerance = 0
  References2D = -> [View007]
  Rotation = 0
  ScaleType = 0
  TheoreticalExact = false
  Type = 1
  UnderTolerance = 0
  X = -18.1668
  Y = 16.9283
FEATURE [TechDraw::DrawViewDimension] Dimension026  label="Cote026"
  AngleOverride = false
  Arbitrary = false
  ArbitraryTolerances = false
  BoxCorners = (2) [(-22.9001,-22.11,-1e-07),(22.9001,22.11,1e-07)]
  EqualTolerance = true
  ExtensionAngle = 0
  FormatSpec = %.0w
  FormatSpecOverTolerance = %+.2w
  FormatSpecUnderTolerance = %+.2w
  Inverted = false
  LineAngle = 0
  LockPosition = false
  MeasureType = 1
  OverTolerance = 0
  References2D = -> [ProjItem003]
  Rotation = 0
  ScaleType = 0
  TheoreticalExact = false
  Type = 0
  UnderTolerance = 0
  X = 11.9681
  Y = -24.4062
FEATURE [TechDraw::DrawViewDimension] Dimension027  label="Cote027"
  AngleOverride = false
  Arbitrary = false
  ArbitraryTolerances = false
  BoxCorners = (2) [(-22.9001,-22.11,-1e-07),(22.9001,22.11,1e-07)]
  EqualTolerance = true
  ExtensionAngle = 0
  FormatSpec = %.0w
  FormatSpecOverTolerance = %+.2w
  FormatSpecUnderTolerance = %+.2w
  Inverted = false
  LineAngle = 0
  LockPosition = false
  MeasureType = 1
  OverTolerance = 0
  References2D = -> [ProjItem003]
  Rotation = 0
  ScaleType = 0
  TheoreticalExact = false
  Type = 0
  UnderTolerance = 0
  X = -17.54
  Y = -31.4062
FEATURE [TechDraw::DrawViewDimension] Dimension028  label="Cote028"
  AngleOverride = false
  Arbitrary = false
  ArbitraryTolerances = false
  BoxCorners = (2) [(-87.1671,-22.11,-1e-07),(87.1671,22.1097,1e-07)]
  EqualTolerance = true
  ExtensionAngle = 0
  FormatSpec = %.0w
  FormatSpecOverTolerance = %+.2w
  FormatSpecUnderTolerance = %+.2w
  Inverted = false
  LineAngle = 0
  LockPosition = false
  MeasureType = 1
  OverTolerance = 0
  References2D = -> [View007]
  Rotation = 0
  ScaleType = 0
  TheoreticalExact = false
  Type = 1
  UnderTolerance = 0
  X = 70.7694
  Y = -5.77901
FEATURE [TechDraw::DrawViewAnnotation] Annotation006
  Font = osifont
  LineSpace = 100
  LockPosition = false
  MaxWidth = -1
  Rotation = 0
  ScaleType = 0
  Text = gueule de loup : détail à l'echelle 1 | (vous pouvez imprimer et scotcher | le détail en bout de barre)
  TextSize = 4
  TextStyle = 0
  X = 250.693
  Y = 166.439
FEATURE [TechDraw::DrawLeaderLine] LeaderLine  label="Ligne de repère"
  AutoHorizontal = false
  EndSymbol = 0
  LeaderParent = -> Detail
  LockPosition = true
  RotatesWithParent = false
  Rotation = 0
  Scalable = false
  ScaleType = 0
  StartSymbol = 7
  WayPoints = (2) [(0,0,0),(-8.65063,39.088,0)]
  X = 13.4421
  Y = 40.5001
FEATURE [TechDraw::DrawViewBalloon] Balloon  label="Infobulle"
  BubbleShape = 3
  EndType = 0
  EndTypeScale = 1
  KinkLength = 5
  LockPosition = false
  OriginX = -1122.04
  OriginY = -115.259
  Rotation = 0
  ScaleType = 0
  ShapeScale = 1
  SourceView = -> View007
  Text = A13
  TextWrapLen = -1
  X = -982.08
  Y = -371.67
FEATURE [TechDraw::DrawViewBalloon] Balloon001  label="Infobulle001"
  BubbleShape = 3
  EndType = 0
  EndTypeScale = 1
  KinkLength = 5
  LockPosition = false
  OriginX = -44.6745
  OriginY = -4.25699
  Rotation = 0
  ScaleType = 0
  ShapeScale = 1
  SourceView = -> Balloon
  Text = A14
  TextWrapLen = -1
  X = -59.5465
  Y = -14.3165
FEATURE [TechDraw::DrawViewBalloon] Balloon002  label="Infobulle002"
  BubbleShape = 3
  EndType = 0
  EndTypeScale = 1
  KinkLength = 5
  LockPosition = false
  OriginX = -1293.39
  OriginY = 66.7976
  Rotation = 0
  ScaleType = 0
  ShapeScale = 1
  SourceView = -> View007
  Text = A16
  TextWrapLen = -1
  X = -1563.24
  Y = 70.2859
FEATURE [TechDraw::DrawViewBalloon] Balloon003  label="Infobulle003"
  BubbleShape = 3
  EndType = 0
  EndTypeScale = 1
  KinkLength = 5
  LockPosition = false
  OriginX = -269.591
  OriginY = -100.266
  Rotation = 0
  ScaleType = 0
  ShapeScale = 1
  SourceView = -> View007
  Text = A5
  TextWrapLen = -1
  X = 60.3933
  Y = -258.621
FEATURE [TechDraw::DrawViewBalloon] Balloon004  label="Infobulle004"
  BubbleShape = 3
  EndType = 0
  EndTypeScale = 1
  KinkLength = 5
  LockPosition = false
  OriginX = 231.599
  OriginY = 79.6486
  Rotation = 0
  ScaleType = 0
  ShapeScale = 1
  SourceView = -> View007
  Text = A1
  TextWrapLen = -1
  X = 364.534
  Y = -187.94
FEATURE [TechDraw::DrawViewBalloon] Balloon005  label="Infobulle005"
  BubbleShape = 3
  EndType = 0
  EndTypeScale = 1
  KinkLength = 5
  LockPosition = false
  OriginX = 964.108
  OriginY = 135.336
  Rotation = 0
  ScaleType = 0
  ShapeScale = 1
  SourceView = -> View007
  Text = A18
  TextWrapLen = -1
  X = 476.914
  Y = 269.945
FEATURE [TechDraw::DrawViewBalloon] Balloon006  label="Infobulle006"
  BubbleShape = 3
  EndType = 0
  EndTypeScale = 1
  KinkLength = 5
  LockPosition = false
  OriginX = 1019.8
  OriginY = 236.003
  Rotation = 0
  ScaleType = 0
  ShapeScale = 1
  SourceView = -> View007
  Text = A9
  TextWrapLen = -1
  X = 1319.36
  Y = 423.053
FEATURE [TechDraw::DrawViewBalloon] Balloon009  label="Infobulle009"
  BubbleShape = 3
  EndType = 0
  EndTypeScale = 1
  KinkLength = 5
  LockPosition = false
  OriginX = -893.134
  OriginY = 99.9702
  Rotation = 0
  ScaleType = 0
  ShapeScale = 1
  SourceView = -> ProjItem002
  Text = A7
  TextWrapLen = -1
  X = -659.964
  Y = 165.705
FEATURE [TechDraw::DrawViewBalloon] Balloon010  label="Infobulle010"
  BubbleShape = 3
  EndType = 0
  EndTypeScale = 1
  KinkLength = 5
  LockPosition = false
  OriginX = -1255
  OriginY = -0.00102179
  Rotation = 0
  ScaleType = 0
  ShapeScale = 1
  SourceView = -> ProjItem002
  Text = A2
  TextWrapLen = -1
  X = -748.878
  Y = 2.9847
FEATURE [TechDraw::DrawViewBalloon] Balloon011  label="Infobulle011"
  BubbleShape = 3
  EndType = 0
  EndTypeScale = 1
  KinkLength = 5
  LockPosition = false
  OriginX = 1148.31
  OriginY = -297.441
  Rotation = 0
  ScaleType = 0
  ShapeScale = 1
  SourceView = -> ProjItem002
  Text = A17
  TextWrapLen = -1
  X = 1265.9
  Y = -116.401
FEATURE [TechDraw::DrawViewBalloon] Balloon012  label="Infobulle012"
  BubbleShape = 3
  EndType = 0
  EndTypeScale = 1
  KinkLength = 5
  LockPosition = false
  OriginX = 1.29779
  OriginY = -63.1508
  Rotation = 0
  ScaleType = 0
  ShapeScale = 1
  SourceView = -> View008
  Text = A9
  TextWrapLen = -1
  X = -89.7705
  Y = -202.571
FEATURE [TechDraw::DrawViewBalloon] Balloon007  label="Infobulle007"
  BubbleShape = 3
  EndType = 0
  EndTypeScale = 1
  KinkLength = 5
  LockPosition = false
  OriginX = -1255
  OriginY = -131.643
  Rotation = 0
  ScaleType = 0
  ShapeScale = 1
  SourceView = -> View007
  Text = A12
  TextWrapLen = -1
  X = -1564.96
  Y = -134.325
FEATURE [TechDraw::DrawViewBalloon] Balloon013  label="Infobulle013"
  BubbleShape = 3
  EndType = 0
  EndTypeScale = 1
  KinkLength = 5
  LockPosition = false
  OriginX = 730
  OriginY = -1.3642e-12
  Rotation = 0
  ScaleType = 0
  ShapeScale = 1
  SourceView = -> ProjItem002
  Text = A8
  TextWrapLen = -1
  X = 1130.67
  Y = 73.4783
FEATURE [TechDraw::DrawViewBalloon] Balloon014  label="Infobulle014"
  BubbleShape = 3
  EndType = 0
  EndTypeScale = 1
  KinkLength = 5
  LockPosition = false
  OriginX = -742.5
  OriginY = 158.357
  Rotation = 0
  ScaleType = 0
  ShapeScale = 1
  SourceView = -> View007
  Text = A3
  TextWrapLen = -1
  X = -1580.33
  Y = 232.592
FEATURE [TechDraw::DrawViewBalloon] Balloon015  label="Infobulle015"
  BubbleShape = 3
  EndType = 0
  EndTypeScale = 1
  KinkLength = 5
  LockPosition = false
  OriginX = -286.587
  OriginY = 146.538
  Rotation = 0
  ScaleType = 0
  ShapeScale = 1
  SourceView = -> View007
  Text = A4
  TextWrapLen = -1
  X = -1578.05
  Y = 355.88
FEATURE [TechDraw::DrawViewBalloon] Balloon016  label="Infobulle016"
  BubbleShape = 3
  EndType = 0
  EndTypeScale = 1
  KinkLength = 5
  LockPosition = false
  OriginX = -0.00265948
  OriginY = 45.8566
  Rotation = 0
  ScaleType = 0
  ShapeScale = 1
  SourceView = -> ProjItem003
  Text = A2
  TextWrapLen = -1
  X = 498.096
  Y = -22.8311
FEATURE [TechDraw::DrawViewBalloon] Balloon017  label="Infobulle017"
  BubbleShape = 3
  EndType = 0
  EndTypeScale = 1
  KinkLength = 5
  LockPosition = false
  OriginX = 19.1419
  OriginY = -214.025
  Rotation = 0
  ScaleType = 0
  ShapeScale = 1
  SourceView = -> ProjItem003
  Text = A6
  TextWrapLen = -1
  X = 500.732
  Y = -301.973
FEATURE [TechDraw::DrawViewBalloon] Balloon018  label="Infobulle018"
  BubbleShape = 3
  EndType = 0
  EndTypeScale = 1
  KinkLength = 5
  LockPosition = false
  OriginX = 177.401
  OriginY = -109.166
  Rotation = 0
  ScaleType = 0
  ShapeScale = 1
  SourceView = -> ProjItem003
  Text = A15
  TextWrapLen = -1
  X = 518.671
  Y = -161.345
FEATURE [TechDraw::DrawViewBalloon] Balloon019  label="Infobulle019"
  BubbleShape = 3
  EndType = 0
  EndTypeScale = 1
  KinkLength = 0
  LockPosition = false
  OriginX = -269.467
  OriginY = -230.57
  Rotation = 0
  ScaleType = 0
  ShapeScale = 1
  SourceView = -> View007
  Text = A10
  TextWrapLen = -1
  X = -77.8741
  Y = -403.054
FEATURE [TechDraw::DrawViewBalloon] Balloon020  label="Infobulle020"
  BubbleShape = 3
  EndType = 0
  EndTypeScale = 1
  KinkLength = 0
  LockPosition = false
  OriginX = -285
  OriginY = -231.643
  Rotation = 0
  ScaleType = 0
  ShapeScale = 1
  SourceView = -> View007
  Text = A11
  TextWrapLen = -1
  X = -475.893
  Y = -281.405
FEATURE [TechDraw::DrawPage] Page002  label="Feuille002"
  KeepUpdated = true
  NextBalloonIndex = 30
  ProjectionType = 0
  Template = -> Template002
  Views = -> [ProjGroup001,View008,Detail,Dimension009,Dimension010,Dimension011,Dimension012,Dimension013,Dimension014,Dimension015,Dimension016,Dimension017,Dimension018,Dimension020,Dimension021,Dimension022,Dimension023,Dimension024,Dimension025,Dimension026,Dimension027,Dimension028,Annotation006,LeaderLine,Balloon,Balloon001,Balloon002,Balloon003,Balloon004,Balloon005,Balloon006,Balloon007,Balloon009,+11 more]
FEATURE [PartDesign::Plane] DatumPlane004
  AttachmentOffset = pos=(0,0,12.5) rot=(0,0,1;0rad)
  AttachmentSupport = -> [XY_Plane022]
  Length = 60
  MapMode = 5
  Placement = pos=(0,0,12.5) rot=(0,0,1;0rad)
  ResizeMode = 0
  Width = 60
FEATURE [Sketcher::SketchObject] Sketch034
  ArcFitTolerance = 1e-06
  AttachmentSupport = -> [DatumPlane004]
  FullyConstrained = false
  MakeInternals = false
  MapMode = 5
  Placement = pos=(0,0,12.5) rot=(0,0,1;0rad)
  expr: Constraints[0] = Pad008.Length - 10 mm
  sketch-geometry (1):
    g0: Circle CenterX=0 CenterY=-140 CenterZ=0 NormalX=0 NormalY=0 NormalZ=1 AngleXU=0 Radius=16.367
  constraints (2):
    c: DistanceY(g0,g-1) = 140
    c: PointOnObject(g0,g-2)
FEATURE [PartDesign::Hole] Hole
  BaseFeature = -> Pad008
  CustomThreadClearance = 0
  Depth = 326.607
  DepthType = 1
  Diameter = 6
  DrillForDepth = false
  DrillPoint = 1
  DrillPointAngle = 118
  HoleCutCountersinkAngle = 90
  HoleCutCustomValues = false
  HoleCutDepth = 0
  HoleCutDiameter = 6.1
  HoleCutType = 0
  ModelThread = false
  Placement = pos=(0,0,0) rot=(1,0,0;1.5708rad)
  Profile = -> Sketch034
  Suppressed = false
  Tapered = false
  TaperedAngle = 90
  ThreadClass = 0
  ThreadDepth = 326.607
  ThreadDepthType = 0
  ThreadDirection = 0
  ThreadFit = 0
  ThreadSize = 0
  ThreadType = 0
  Threaded = false
  UseCustomThreadClearance = false
FEATURE [PartDesign::Body] Body
  AllowCompound = false
  Group = -> [Sketch012,Pad008,Sketch034,DatumPlane004,Hole]
  Origin = -> Origin022
  Tip = -> Hole
FEATURE [App::Part] Part  label="A10"
  Group = -> [Body,axe]
  Nom_de_la_piece = 'A10
  Origin = -> Origin021
  Reference_AP = fer rond Ø25
  longueur = 150
FEATURE [PartDesign::CoordinateSystem] LCS_Origin001
  AttacherType = Attacher::AttachEngine3D
  AttachmentSupport = -> [X_Axis047]
  MapMode = 2
FEATURE [PartDesign::CoordinateSystem] LCS_Origin002
  AttacherType = Attacher::AttachEngine3D
  AttachmentSupport = -> [X_Axis048]
  MapMode = 2
FEATURE [Sketcher::SketchObject] Sketch035
  ArcFitTolerance = 1e-06
  AttachmentSupport = -> [YZ_Plane046]
  FullyConstrained = true
  MakeInternals = false
  MapMode = 5
  Placement = pos=(0,0,0) rot=(0.57735,0.57735,0.57735;2.0944rad)
  sketch-geometry (4):
    g0: LineSegment StartX=-1 StartY=28 StartZ=0 EndX=-1 EndY=13 EndZ=0
    g1: LineSegment StartX=-1 StartY=13 StartZ=0 EndX=1 EndY=13 EndZ=0
    g2: LineSegment StartX=1 StartY=13 StartZ=0 EndX=1 EndY=28 EndZ=0
    g3: LineSegment StartX=1 StartY=28 StartZ=0 EndX=-1 EndY=28 EndZ=0
  constraints (11):
    c: Coincident(g0,g1)
    c: Coincident(g1,g2)
    c: Coincident(g2,g3)
    c: Coincident(g3,g0)
    c: Vertical(g0)
    c: Vertical(g2)
    c: Horizontal(g3)
    c: Symmetric(g0,g1,g-2)
    c: DistanceY(g-1,g1) = 13  'rayint'
    c: DistanceY(g-1,g2) = 28  'rayext'
    c: DistanceX(g3,g3) = 2  'ep'
FEATURE [PartDesign::Revolution] Revolution001
  Angle = 360
  Angle2 = 60
  Axis = (0,1,0)
  Base = (0,0,0)
  Placement = pos=(0,0,0) rot=(1,1,1;2.0944rad)
  Profile = -> Sketch035
  ReferenceAxis = -> Sketch035 [H_Axis]
  Suppressed = false
  Type = 0
FEATURE [PartDesign::Body] rondellle
  AllowCompound = false
  Group = -> [LCS_Origin002,Sketch035,Revolution001]
  Origin = -> Origin046
  Tip = -> Revolution001
FEATURE [App::Part] rondelle_25  label="rondelle 25"
  Group = -> [LCS_Origin001,rondellle]
  Origin = -> Origin045
FEATURE [App::Link] rondelle_026  label="rondelle 026"
  AttachedBy = #LCS_Origin001
  AttachedTo = A10006#axe
  AttachmentOffset = pos=(0,12.5,136) rot=(1,0,0;1.5708rad)
  LinkPlacement = pos=(1005,329.5,-312.5) rot=(0,0,1;0rad)
  LinkedObject = -> rondelle_25
  Placement = pos=(1005,329.5,-312.5) rot=(0,0,1;0rad)
  SolverId = Asm4EE
  expr: Placement = A10006.Placement * axe.Placement * AttachmentOffset * LCS_Origin001.Placement ^ -1
FEATURE [App::Link] rondelle_027  label="rondelle 027"
  AttachedBy = #LCS_Origin001
  AttachedTo = A10#axe
  AttachmentOffset = pos=(0,12.5,136) rot=(1,0,0;1.5708rad)
  LinkPlacement = pos=(1005,-329.5,-312.5) rot=(0,0,-1;3.14159rad)
  LinkedObject = -> rondelle_25
  Placement = pos=(1005,-329.5,-312.5) rot=(0,0,-1;3.14159rad)
  SolverId = Asm4EE
  expr: Placement = A10.Placement * axe.Placement * AttachmentOffset * LCS_Origin001.Placement ^ -1
FEATURE [App::Link] rondelle_028  label="rondelle 028"
  AttachedBy = #LCS_Origin001
  AttachedTo = A10#axe
  AttachmentOffset = pos=(0,12.5,52) rot=(1,0,0;1.5708rad)
  LinkPlacement = pos=(1005,-245.5,-312.5) rot=(0,0,-1;3.14159rad)
  LinkedObject = -> rondelle_25
  Placement = pos=(1005,-245.5,-312.5) rot=(0,0,-1;3.14159rad)
  SolverId = Asm4EE
  expr: Placement = A10.Placement * axe.Placement * AttachmentOffset * LCS_Origin001.Placement ^ -1
FEATURE [App::Link] rondelle_029  label="rondelle 029"
  AttachedBy = #LCS_Origin001
  AttachedTo = A10006#axe
  AttachmentOffset = pos=(0,12.5,52) rot=(1,0,0;1.5708rad)
  LinkPlacement = pos=(1005,245.5,-312.5) rot=(0,0,1;0rad)
  LinkedObject = -> rondelle_25
  Placement = pos=(1005,245.5,-312.5) rot=(0,0,1;0rad)
  SolverId = Asm4EE
  expr: Placement = A10006.Placement * axe.Placement * AttachmentOffset * LCS_Origin001.Placement ^ -1
FEATURE [PartDesign::CoordinateSystem] LCS_Origin003
  AttacherType = Attacher::AttachEngine3D
  AttachmentSupport = -> [X_Axis049]
  MapMode = 2
FEATURE [PartDesign::CoordinateSystem] LCS_Origin004
  AttacherType = Attacher::AttachEngine3D
  AttachmentSupport = -> [X_Axis050]
  MapMode = 2
FEATURE [Sketcher::SketchObject] Sketch036
  ArcFitTolerance = 1e-06
  AttachmentSupport = -> [XZ_Plane048]
  FullyConstrained = false
  MakeInternals = false
  MapMode = 5
  Placement = pos=(0,0,0) rot=(1,0,0;1.5708rad)
  sketch-geometry (11):
    g0: Circle [constr] CenterX=0 CenterY=0 CenterZ=0 NormalX=0 NormalY=0 NormalZ=1 AngleXU=0 Radius=13.75
    g1: LineSegment [constr] StartX=0 StartY=-40 StartZ=0 EndX=0 EndY=40 EndZ=0
    g2: Circle [constr] CenterX=-10 CenterY=30 CenterZ=0 NormalX=0 NormalY=0 NormalZ=1 AngleXU=0 Radius=10
    g3: GeomPoint [constr] X=0 Y=30 Z=0
    g4: LineSegment [constr] StartX=0 StartY=40 StartZ=0 EndX=-69.1627 EndY=40 EndZ=0
    g5: LineSegment StartX=0 StartY=-40 StartZ=0 EndX=0 EndY=30 EndZ=0
    g6: ArcOfCircle CenterX=-10 CenterY=30 CenterZ=0 NormalX=0 NormalY=0 NormalZ=1 AngleXU=0 Radius=10 StartAngle=4.06135e-09 EndAngle=4.58938
    g7: ArcOfCircle CenterX=-11.8728 CenterY=14.8514 CenterZ=0 NormalX=0 NormalY=0 NormalZ=1 AngleXU=0 Radius=5.26396 StartAngle=5.38202 EndAngle=7.73097
    g8: ArcOfCircle CenterX=0 CenterY=0 CenterZ=0 NormalX=0 NormalY=0 NormalZ=1 AngleXU=0 Radius=13.75 StartAngle=2.24702 EndAngle=4.04719
    g9: ArcOfCircle CenterX=-12.0115 CenterY=-15.2346 CenterZ=0 NormalX=0 NormalY=0 NormalZ=1 AngleXU=0 Radius=5.65039 StartAngle=5.15136 EndAngle=7.18037
    g10: LineSegment StartX=-9.61003 StartY=-20.3493 StartZ=0 EndX=-12.9682 EndY=-21.926 EndZ=0
  constraints (21):
    c: Diameter(g0) = 27.5
    c: Coincident(g0,g-1)
    c: Distance(g1) = 80
    c: Vertical(g1)
    c: Diameter(g2) = 20
    c: PointOnObject(g3,g2)
    c: PointOnObject(g3,g1)
    c: Coincident(g4,g1)
    c: Horizontal(g4)
    c: Tangent(g4,g2)
    c: Symmetric(g1,g1,g0)
    c: Coincident(g5,g1)
    c: Coincident(g5,g3)
    c: Coincident(g6,g2)
    c: Coincident(g6,g3)
    c: PointOnObject(g7,g0)
    c: Coincident(g7,g6)
    c: Coincident(g8,g0)
    c: Coincident(g8,g7)
    c: Coincident(g9,g8)
    c: Tangent(g10,g9) = 1.5708
FEATURE [PartDesign::Plane] DatumPlane005
  AttachmentSupport = -> [Sketch036]
  Length = 60
  MapMode = 7
  Placement = pos=(0,-8.9e-15,-40) rot=(0,1,0;3.14159rad)
  ResizeMode = 0
  Width = 60
FEATURE [Sketcher::SketchObject] Sketch037
  ArcFitTolerance = 1e-06
  AttachmentSupport = -> [DatumPlane005]
  FullyConstrained = true
  MakeInternals = false
  MapMode = 5
  Placement = pos=(0,-8.9e-15,-40) rot=(0,1,0;3.14159rad)
  sketch-geometry (1):
    g0: Circle CenterX=0 CenterY=0 CenterZ=0 NormalX=0 NormalY=0 NormalZ=1 AngleXU=0 Radius=2.5
  constraints (2):
    c: Diameter(g0) = 5
    c: Coincident(g0,g-1)
FEATURE [PartDesign::AdditivePipe] AdditivePipe001
  AuxilleryCurvelinear = true
  AuxillerySpineTangent = false
  Binormal = (0,0,0)
  Mode = 0
  Placement = pos=(0,-8.9e-15,-40) rot=(0,1,0;3.14159rad)
  Profile = -> Sketch037
  Spine = -> Sketch036
  SpineTangent = false
  Suppressed = false
  Transformation = 0
  Transition = 0
FEATURE [PartDesign::Body] goupille
  AllowCompound = false
  Group = -> [LCS_Origin004,Sketch036,DatumPlane005,Sketch037,AdditivePipe001]
  Origin = -> Origin048
  Tip = -> AdditivePipe001
FEATURE [App::Part] goupille_elastique_5_x_80  label="goupille elastique 5 x 80"
  Group = -> [LCS_Origin003,goupille]
  Origin = -> Origin047
FEATURE [App::DocumentObjectGroup] Parts
  Group = -> [A1,A2,A3,A4,Roue_increvable___389___axe25_L_82,A5,A6,A7,A8,A8003,Part,Part001,Part002,Part003,Part004,Part005,Part006,Part008,Part009,Part007,Part010,Part011,rondelle_25,goupille_elastique_5_x_80]
FEATURE [App::Link] goupille_elastique_5_x_081  label="goupille elastique 5 x 081"
  AttachedBy = #LCS_Origin003
  AttachedTo = A10#axe
  AttachmentOffset = pos=(0,12.5,140) rot=(1,0,0;1.5708rad)
  LinkPlacement = pos=(1005,-333.5,-312.5) rot=(0,0,-1;3.14159rad)
  LinkedObject = -> goupille_elastique_5_x_80
  Placement = pos=(1005,-333.5,-312.5) rot=(0,0,-1;3.14159rad)
  SolverId = Asm4EE
  expr: Placement = A10.Placement * axe.Placement * AttachmentOffset * LCS_Origin003.Placement ^ -1
FEATURE [App::Link] goupille_elastique_5_x_082  label="goupille elastique 5 x 082"
  AttachedBy = #LCS_Origin003
  AttachedTo = A10006#axe
  AttachmentOffset = pos=(0,12.5,140) rot=(1,0,0;1.5708rad)
  LinkPlacement = pos=(1005,333.5,-312.5) rot=(0,0,1;0rad)
  LinkedObject = -> goupille_elastique_5_x_80
  Placement = pos=(1005,333.5,-312.5) rot=(0,0,1;0rad)
  SolverId = Asm4EE
  expr: Placement = A10006.Placement * axe.Placement * AttachmentOffset * LCS_Origin003.Placement ^ -1
FEATURE [App::Part] Model
  Configuration = 0
  Group = -> [LCS_Origin,Constraints,Variables,A2001,A1001,A1004,A3001,A3002,A4001,A4002,A2003,A5001,A5002,A6001,A7003,A7004,A8002,A9,A9001,Sketch014,A12,A12001,A12002,A12003,A13001,A14001,A2004,A2005,A14002,A14003,A14004,A11,A11001,A10,A10006,Roue_increvable___389___axe25_L_82001,Roue_increvable___389___axe25_L_82002,A15,A14008,A15001,A15002,A16,A16001,BB1,BB1001,BB3,BB2,BB1003,BB1004,A17,A17001,A18,A18001,+11 more]
  Origin = -> Origin
  Type = Assembly4 Model
FEATURE [TechDraw::DrawProjGroupItem] View  label="Front"
  CoarseView = false
  Direction = (0,-1,0)
  Focus = 100
  HardHidden = false
  IsoCount = 0
  IsoHidden = false
  IsoVisible = false
  LockPosition = true
  Perspective = false
  Rotation = 0
  RotationVector = (1,0,0)
  Scale = 0.05
  ScaleType = 2
  ScrubCount = 1
  SeamHidden = false
  SeamVisible = false
  SmoothHidden = false
  SmoothVisible = true
  Source = -> [Model]
  Type = 0
  X = 0
  XDirection = (1,0,0)
  Y = 0
FEATURE [TechDraw::DrawProjGroupItem] ProjItem001  label="Dessus"
  CoarseView = false
  Direction = (0,0,1)
  Focus = 100
  HardHidden = false
  IsoCount = 0
  IsoHidden = false
  IsoVisible = false
  LockPosition = true
  Perspective = false
  Rotation = 0
  RotationVector = (1,0,0)
  ScaleType = 0
  ScrubCount = 1
  SeamHidden = false
  SeamVisible = false
  SmoothHidden = false
  SmoothVisible = false
  Source = -> [Model]
  Type = 4
  X = 0
  XDirection = (1,0,0)
  Y = 70.4662
FEATURE [TechDraw::DrawProjGroupItem] ProjItem  label="Avant en haut à droite"
  CoarseView = false
  Direction = (0.57735,-0.57735,0.57735)
  Focus = 100
  HardHidden = false
  IsoCount = 0
  IsoHidden = false
  IsoVisible = false
  LockPosition = true
  Perspective = false
  Rotation = 0
  RotationVector = (1,0,0)
  ScaleType = 0
  ScrubCount = 1
  SeamHidden = false
  SeamVisible = false
  SmoothHidden = false
  SmoothVisible = true
  Source = -> [Model]
  Type = 7
  X = 147.302
  XDirection = (0.707107,0.707107,0)
  Y = 97.4798
FEATURE [TechDraw::DrawProjGroup] ProjGroup
  Anchor = -> View
  AutoDistribute = true
  LockPosition = false
  ProjectionType = 0
  Rotation = 0
  Scale = 0.05
  ScaleType = 2
  Source = -> [Model]
  Views = -> [View,ProjItem001,ProjItem]
  X = 82.3141
  Y = 56.2019
  spacingX = 15
  spacingY = 15
FEATURE [TechDraw::DrawViewDimExtent] DimExtent
  AngleOverride = false
  Arbitrary = false
  ArbitraryTolerances = false
  DirExtent = 1
  EqualTolerance = true
  ExtensionAngle = 0
  FormatSpec = %.2w
  FormatSpecOverTolerance = %+.2w
  FormatSpecUnderTolerance = %+.2w
  Inverted = false
  LineAngle = 0
  LockPosition = false
  MeasureType = 1
  OverTolerance = 0
  References2D = -> [ProjItem001]
  Rotation = 0
  ScaleType = 0
  Source = -> [ProjItem001]
  TheoreticalExact = false
  Type = 2
  UnderTolerance = 0
  X = -72.7624
  Y = 8.40417
FEATURE [TechDraw::DrawViewDimExtent] DimExtent001
  AngleOverride = false
  Arbitrary = false
  ArbitraryTolerances = false
  DirExtent = 0
  EqualTolerance = true
  ExtensionAngle = 0
  FormatSpec = %.2w
  FormatSpecOverTolerance = %+.2w
  FormatSpecUnderTolerance = %+.2w
  Inverted = false
  LineAngle = 0
  LockPosition = false
  MeasureType = 1
  OverTolerance = 0
  References2D = -> [ProjItem001]
  Rotation = 0
  ScaleType = 0
  Source = -> [ProjItem001]
  TheoreticalExact = false
  Type = 1
  UnderTolerance = 0
  X = 0
  Y = 29.8569
FEATURE [TechDraw::DrawViewDimension] Dimension  label="Cote"
  AngleOverride = false
  Arbitrary = false
  ArbitraryTolerances = false
  BoxCorners = (2) [(-65.375,-17.175,-1e-07),(65.375,17.175,1e-07)]
  EqualTolerance = true
  ExtensionAngle = 0
  FormatSpec = %.2w
  FormatSpecOverTolerance = %+.2w
  FormatSpecUnderTolerance = %+.2w
  Inverted = false
  LineAngle = 0
  LockPosition = false
  MeasureType = 1
  OverTolerance = 0
  References2D = -> [ProjItem001]
  Rotation = 0
  ScaleType = 0
  TheoreticalExact = false
  Type = 0
  UnderTolerance = 0
  X = -10.2604
  Y = -24.9269
FEATURE [TechDraw::DrawViewDimension] Dimension001  label="Cote001"
  AngleOverride = false
  Arbitrary = false
  ArbitraryTolerances = false
  BoxCorners = (2) [(-65.375,-17.175,-1e-07),(65.375,17.175,1e-07)]
  EqualTolerance = true
  ExtensionAngle = 0
  FormatSpec = %.2w
  FormatSpecOverTolerance = %+.2w
  FormatSpecUnderTolerance = %+.2w
  Inverted = false
  LineAngle = 0
  LockPosition = false
  MeasureType = 1
  OverTolerance = 0
  References2D = -> [ProjItem001]
  Rotation = 0
  ScaleType = 0
  TheoreticalExact = false
  Type = 0
  UnderTolerance = 0
  X = 73.1222
  Y = 0
FEATURE [TechDraw::DrawViewDimExtent] DimExtent002
  AngleOverride = false
  Arbitrary = false
  ArbitraryTolerances = false
  DirExtent = 1
  EqualTolerance = true
  ExtensionAngle = 0
  FormatSpec = %.2w
  FormatSpecOverTolerance = %+.2w
  FormatSpecUnderTolerance = %+.2w
  Inverted = false
  LineAngle = 0
  LockPosition = false
  MeasureType = 1
  OverTolerance = 0
  References2D = -> [View]
  Rotation = 0
  ScaleType = 0
  Source = -> [View]
  TheoreticalExact = false
  Type = 2
  UnderTolerance = 0
  X = -72.6462
  Y = 0
FEATURE [TechDraw::DrawViewDimension] Dimension002  label="Cote002"
  AngleOverride = false
  Arbitrary = false
  ArbitraryTolerances = false
  BoxCorners = (2) [(-65.375,-28.375,-1e-07),(65.375,28.375,1e-07)]
  EqualTolerance = true
  ExtensionAngle = 0
  FormatSpec = %.2w
  FormatSpecOverTolerance = %+.2w
  FormatSpecUnderTolerance = %+.2w
  Inverted = false
  LineAngle = 0
  LockPosition = false
  MeasureType = 1
  OverTolerance = 0
  References2D = -> [View]
  Rotation = 0
  ScaleType = 0
  TheoreticalExact = false
  Type = 2
  UnderTolerance = 0
  X = -51.6484
  Y = 13.125
FEATURE [TechDraw::DrawPage] Page  label="Feuille"
  KeepUpdated = true
  NextBalloonIndex = 1
  ProjectionType = 0
  Template = -> Template
  Views = -> [ProjGroup,DimExtent,DimExtent001,Dimension,Dimension001,DimExtent002,Dimension002]
FEATURE [TechDraw::DrawProjGroupItem] View010
  CoarseView = false
  Direction = (0.57735,-0.57735,0.57735)
  Focus = 100
  HardHidden = false
  IsoCount = 0
  IsoHidden = false
  IsoVisible = false
  LockPosition = false
  Perspective = false
  Rotation = 0
  RotationVector = (1,0,0)
  Scale = 0.066667
  ScaleType = 2
  ScrubCount = 1
  SeamHidden = false
  SeamVisible = false
  SmoothHidden = false
  SmoothVisible = true
  Type = 0
  X = 210.702
  XDirection = (0.707107,0.707107,0)
  XSource = -> [rondelle_026,goupille_elastique_5_x_082]
  Y = 96.9368
FEATURE [TechDraw::DrawProjGroupItem] View011
  CoarseView = false
  Direction = (0.57735,-0.57735,0.57735)
  Focus = 100
  HardHidden = false
  IsoCount = 0
  IsoHidden = false
  IsoVisible = false
  LockPosition = false
  Perspective = false
  Rotation = 0
  RotationVector = (1,0,0)
  Scale = 0.066667
  ScaleType = 2
  ScrubCount = 1
  SeamHidden = false
  SeamVisible = false
  SmoothHidden = false
  SmoothVisible = true
  Type = 0
  X = 102.137
  XDirection = (0.707107,0.707107,0)
  XSource = -> [rondelle_027,goupille_elastique_5_x_081]
  Y = 23.792
FEATURE [TechDraw::DrawPage] Page001  label="Feuille001"
  KeepUpdated = true
  NextBalloonIndex = 1
  ProjectionType = 0
  Template = -> Template001
  Views = -> [View003,View004,View005,View006,View010,View011]
FEATURE [TechDraw::DrawViewBalloon] Balloon022  label="Infobulle022"
  BubbleShape = 3
  EndType = 0
  EndTypeScale = 1
  KinkLength = 5
  LockPosition = false
  OriginX = -93.9744
  OriginY = 26.9231
  Rotation = 0
  ScaleType = 0
  ShapeScale = 1
  SourceView = -> ProjItem004
  Text = BB2
  TextWrapLen = -1
  X = 6.02564
  Y = 126.923
FEATURE [TechDraw::DrawViewBalloon] Balloon023  label="Infobulle023"
  BubbleShape = 3
  EndType = 0
  EndTypeScale = 1
  KinkLength = 5
  LockPosition = false
  OriginX = -390.128
  OriginY = -29.1667
  Rotation = 0
  ScaleType = 0
  ShapeScale = 1
  SourceView = -> ProjItem004
  Text = BB1
  TextWrapLen = -1
  X = -485.321
  Y = 102.244
FEATURE [TechDraw::DrawViewBalloon] Balloon024  label="Infobulle024"
  BubbleShape = 3
  EndType = 0
  EndTypeScale = 1
  KinkLength = 5
  LockPosition = false
  OriginX = 291.923
  OriginY = 26.9231
  Rotation = 0
  ScaleType = 0
  ShapeScale = 1
  SourceView = -> ProjItem004
  Text = BB1
  TextWrapLen = -1
  X = 181.026
  Y = 126.923
FEATURE [TechDraw::DrawPage] Page003  label="Feuille003"
  KeepUpdated = true
  NextBalloonIndex = 6
  ProjectionType = 0
  Template = -> Template003
  Views = -> [ProjGroup002,Dimension003,Dimension004,Dimension005,Dimension006,Dimension007,Balloon022,Balloon023,Balloon024]
